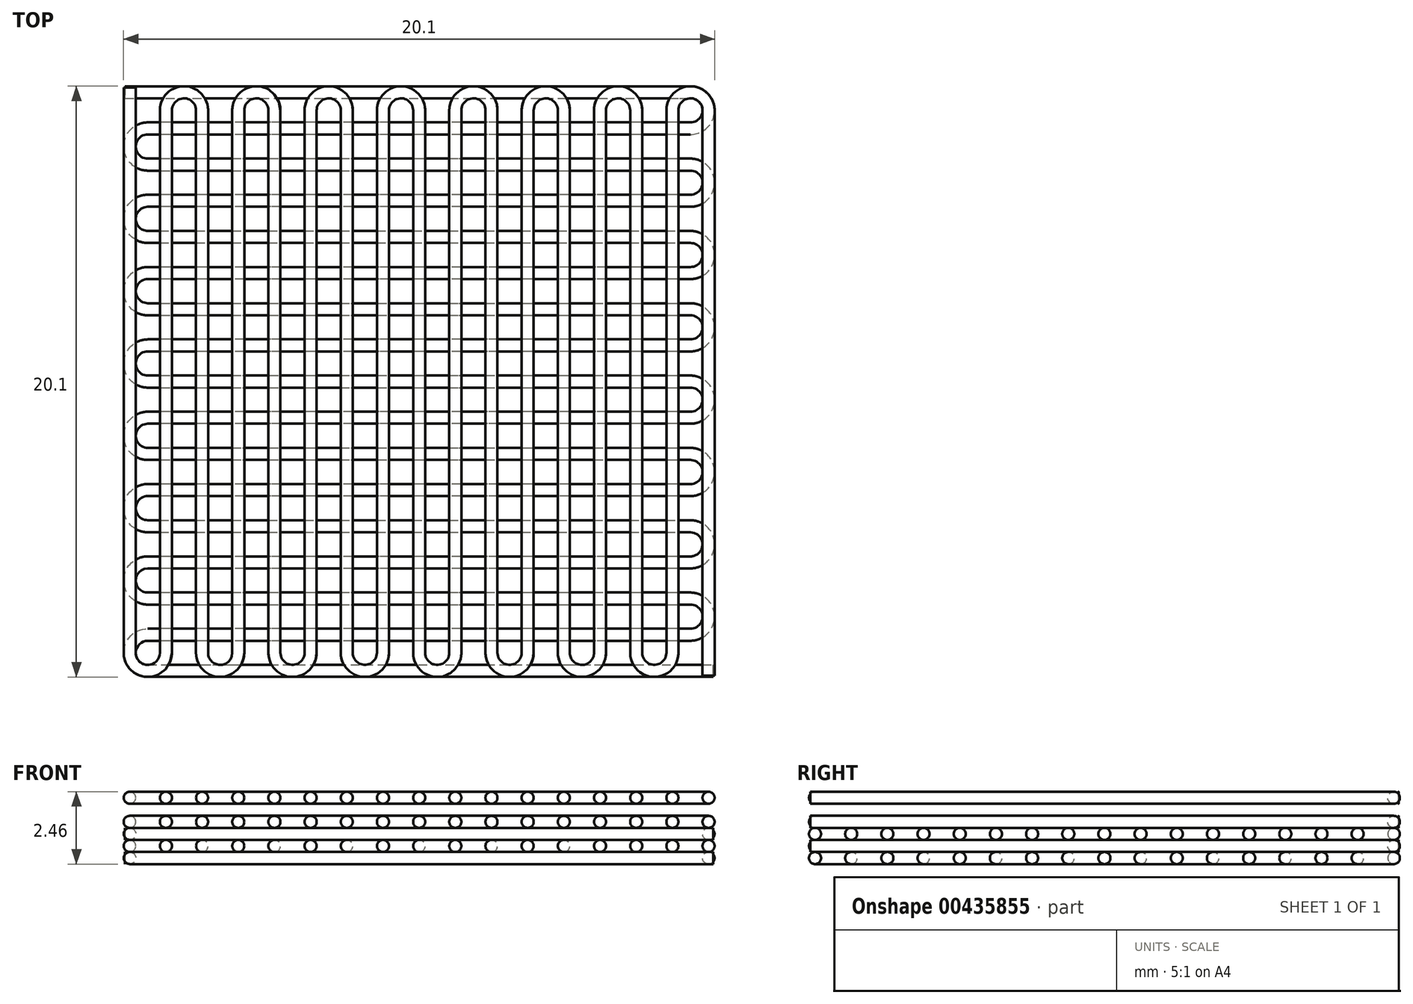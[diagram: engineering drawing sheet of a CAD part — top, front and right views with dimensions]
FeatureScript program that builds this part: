
annotation { "Feature Type Name" : "Feature", "Feature Type Description" : "" }
export const myFeature = defineFeature(function(context is Context, id is Id, definition is map)
    precondition{}
    {
        {
            assignVariable(context, id + "F0", {"name" : "d", "anyValue" : 0.4 * mm});
        }
        {
            var Q0;
            Q0=qCreatedBy(makeId("Top.planeOp"),FACE);
            cPlane(context, id + "F1", {"entities" : qUnion([Q0]), "cplaneType" : CPlaneType.OFFSET, "offset" : getVariable(context, 'd') / 2, "width" : 150 * mm, "height" : 150 * mm});
        }
        {
            var Q0;
            Q0=qCreatedBy(id+"F1.planeOp",FACE);
            var sketch = newSketch(context, id + "F2", { "sketchPlane" : qUnion([Q0])});
            skLineSegment(sketch, "E0.bottom", {"start": v(10, 10) * mm, "end": v(-10, 10) * mm});
            skLineSegment(sketch, "E0.top", {"start": v(10, -10) * mm, "end": v(-10, -10) * mm});
            skLineSegment(sketch, "E0.left", {"start": v(10, 10) * mm, "end": v(10, -10) * mm});
            skLineSegment(sketch, "E0.right", {"start": v(-10, 10) * mm, "end": v(-10, -10) * mm});
            skPoint(sketch, "E0.middle", {"position": v(0, 0) * mm});
            skLineSegment(sketch, "E1", {"start": v(-10, 10) * mm, "end": v(-9.84, 10) * mm});
            skLineSegment(sketch, "E2", {"start": v(-9.84, 10) * mm, "end": v(-8.61, 10) * mm});
            skLineSegment(sketch, "E3", {"start": v(-8.61, 10) * mm, "end": v(-7.38, 10) * mm});
            skLineSegment(sketch, "E4", {"start": v(-7.38, 10) * mm, "end": v(-6.15, 10) * mm});
            skLineSegment(sketch, "E5", {"start": v(-6.15, 10) * mm, "end": v(-4.92, 10) * mm});
            skLineSegment(sketch, "E6", {"start": v(-4.92, 10) * mm, "end": v(-3.7, 10) * mm});
            skLineSegment(sketch, "E7", {"start": v(-3.7, 10) * mm, "end": v(-2.46, 10) * mm});
            skLineSegment(sketch, "E8", {"start": v(-2.46, 10) * mm, "end": v(-1.23, 10) * mm});
            skLineSegment(sketch, "E9", {"start": v(-1.23, 10) * mm, "end": v(0, 10) * mm});
            skLineSegment(sketch, "E10", {"start": v(0, 10) * mm, "end": v(1.23, 10) * mm});
            skLineSegment(sketch, "E11", {"start": v(1.23, 10) * mm, "end": v(2.46, 10) * mm});
            skLineSegment(sketch, "E12", {"start": v(2.46, 10) * mm, "end": v(3.69, 10) * mm});
            skLineSegment(sketch, "E13", {"start": v(3.69, 10) * mm, "end": v(4.92, 10) * mm});
            skLineSegment(sketch, "E14", {"start": v(4.92, 10) * mm, "end": v(6.15, 10) * mm});
            skLineSegment(sketch, "E15", {"start": v(6.15, 10) * mm, "end": v(7.38, 10) * mm});
            skLineSegment(sketch, "E16", {"start": v(7.38, 10) * mm, "end": v(8.6, 10) * mm});
            skLineSegment(sketch, "E17", {"start": v(8.6, 10) * mm, "end": v(9.84, 10) * mm});
            skLineSegment(sketch, "E18", {"start": v(9.84, 10) * mm, "end": v(10, 10) * mm});
            skLineSegment(sketch, "E19", {"start": v(-9.84, 10) * mm, "end": v(-9.84, -10) * mm});
            skLineSegment(sketch, "E20", {"start": v(-9.84, -10) * mm, "end": v(-10, -10) * mm});
            skLineSegment(sketch, "E21", {"start": v(-8.61, 10) * mm, "end": v(-8.61, -10) * mm});
            skLineSegment(sketch, "E22", {"start": v(-8.61, -10) * mm, "end": v(-9.84, -10) * mm});
            skLineSegment(sketch, "E23", {"start": v(-7.38, 10) * mm, "end": v(-7.38, -10) * mm});
            skLineSegment(sketch, "E24", {"start": v(-7.38, -10) * mm, "end": v(-8.61, -10) * mm});
            skLineSegment(sketch, "E25", {"start": v(-6.15, 10) * mm, "end": v(-6.15, -10) * mm});
            skLineSegment(sketch, "E26", {"start": v(-6.15, -10) * mm, "end": v(-7.38, -10) * mm});
            skLineSegment(sketch, "E27", {"start": v(-4.92, 10) * mm, "end": v(-4.92, -10) * mm});
            skLineSegment(sketch, "E28", {"start": v(-4.92, -10) * mm, "end": v(-6.15, -10) * mm});
            skLineSegment(sketch, "E29", {"start": v(-3.7, 10) * mm, "end": v(-3.7, -10) * mm});
            skLineSegment(sketch, "E30", {"start": v(-3.7, -10) * mm, "end": v(-4.92, -10) * mm});
            skLineSegment(sketch, "E31", {"start": v(-2.46, 10) * mm, "end": v(-2.46, -10) * mm});
            skLineSegment(sketch, "E32", {"start": v(-2.46, -10) * mm, "end": v(-3.7, -10) * mm});
            skLineSegment(sketch, "E33", {"start": v(-1.23, 10) * mm, "end": v(-1.23, -10) * mm});
            skLineSegment(sketch, "E34", {"start": v(-1.23, -10) * mm, "end": v(-2.46, -10) * mm});
            skLineSegment(sketch, "E35", {"start": v(0, 10) * mm, "end": v(0, -10) * mm});
            skLineSegment(sketch, "E36", {"start": v(0, -10) * mm, "end": v(-1.23, -10) * mm});
            skLineSegment(sketch, "E37", {"start": v(1.23, 10) * mm, "end": v(1.23, -10) * mm});
            skLineSegment(sketch, "E38", {"start": v(1.23, -10) * mm, "end": v(0, -10) * mm});
            skLineSegment(sketch, "E39", {"start": v(2.46, 10) * mm, "end": v(2.46, -10) * mm});
            skLineSegment(sketch, "E40", {"start": v(2.46, -10) * mm, "end": v(1.23, -10) * mm});
            skLineSegment(sketch, "E41", {"start": v(3.69, 10) * mm, "end": v(3.69, -10) * mm});
            skLineSegment(sketch, "E42", {"start": v(3.69, -10) * mm, "end": v(2.46, -10) * mm});
            skLineSegment(sketch, "E43", {"start": v(4.92, 10) * mm, "end": v(4.92, -10) * mm});
            skLineSegment(sketch, "E44", {"start": v(4.92, -10) * mm, "end": v(3.69, -10) * mm});
            skLineSegment(sketch, "E45", {"start": v(6.15, 10) * mm, "end": v(6.15, -10) * mm});
            skLineSegment(sketch, "E46", {"start": v(6.15, -10) * mm, "end": v(4.92, -10) * mm});
            skLineSegment(sketch, "E47", {"start": v(7.38, 10) * mm, "end": v(7.38, -10) * mm});
            skLineSegment(sketch, "E48", {"start": v(7.38, -10) * mm, "end": v(6.15, -10) * mm});
            skLineSegment(sketch, "E49", {"start": v(8.6, 10) * mm, "end": v(8.6, -10) * mm});
            skLineSegment(sketch, "E50", {"start": v(8.6, -10) * mm, "end": v(7.38, -10) * mm});
            skLineSegment(sketch, "E51", {"start": v(9.84, 10) * mm, "end": v(9.84, -10) * mm});
            skLineSegment(sketch, "E52", {"start": v(9.84, -10) * mm, "end": v(8.6, -10) * mm});
            skLineSegment(sketch, "E53", {"start": v(10, -10) * mm, "end": v(9.84, -10) * mm});
            skLineSegment(sketch, "E54", {"start": v(-10, 9.84) * mm, "end": v(-9.84, 9.84) * mm});
            skLineSegment(sketch, "E55", {"start": v(-9.84, 9.84) * mm, "end": v(-8.61, 9.84) * mm});
            skLineSegment(sketch, "E56", {"start": v(-8.61, 9.84) * mm, "end": v(-7.38, 9.84) * mm});
            skLineSegment(sketch, "E57", {"start": v(-7.38, 9.84) * mm, "end": v(-6.15, 9.84) * mm});
            skLineSegment(sketch, "E58", {"start": v(-6.15, 9.84) * mm, "end": v(-4.92, 9.84) * mm});
            skLineSegment(sketch, "E59", {"start": v(-4.92, 9.84) * mm, "end": v(-3.7, 9.84) * mm});
            skLineSegment(sketch, "E60", {"start": v(-3.7, 9.84) * mm, "end": v(-2.46, 9.84) * mm});
            skLineSegment(sketch, "E61", {"start": v(-2.46, 9.84) * mm, "end": v(-1.23, 9.84) * mm});
            skLineSegment(sketch, "E62", {"start": v(-1.23, 9.84) * mm, "end": v(0, 9.84) * mm});
            skLineSegment(sketch, "E63", {"start": v(0, 9.84) * mm, "end": v(1.23, 9.84) * mm});
            skLineSegment(sketch, "E64", {"start": v(1.23, 9.84) * mm, "end": v(2.46, 9.84) * mm});
            skLineSegment(sketch, "E65", {"start": v(2.46, 9.84) * mm, "end": v(3.69, 9.84) * mm});
            skLineSegment(sketch, "E66", {"start": v(3.69, 9.84) * mm, "end": v(4.92, 9.84) * mm});
            skLineSegment(sketch, "E67", {"start": v(4.92, 9.84) * mm, "end": v(6.15, 9.84) * mm});
            skLineSegment(sketch, "E68", {"start": v(6.15, 9.84) * mm, "end": v(7.38, 9.84) * mm});
            skLineSegment(sketch, "E69", {"start": v(7.38, 9.84) * mm, "end": v(8.6, 9.84) * mm});
            skLineSegment(sketch, "E70", {"start": v(8.6, 9.84) * mm, "end": v(9.84, 9.84) * mm});
            skLineSegment(sketch, "E71", {"start": v(9.84, 9.84) * mm, "end": v(10, 9.84) * mm});
            skLineSegment(sketch, "E72", {"start": v(-10, -9.84) * mm, "end": v(-9.84, -9.84) * mm});
            skLineSegment(sketch, "E73", {"start": v(-9.84, -9.84) * mm, "end": v(-8.61, -9.84) * mm});
            skLineSegment(sketch, "E74", {"start": v(-8.61, -9.84) * mm, "end": v(-7.38, -9.84) * mm});
            skLineSegment(sketch, "E75", {"start": v(-7.38, -9.84) * mm, "end": v(-6.15, -9.84) * mm});
            skLineSegment(sketch, "E76", {"start": v(-6.15, -9.84) * mm, "end": v(-4.92, -9.84) * mm});
            skLineSegment(sketch, "E77", {"start": v(-4.92, -9.84) * mm, "end": v(-3.7, -9.84) * mm});
            skLineSegment(sketch, "E78", {"start": v(-3.7, -9.84) * mm, "end": v(-2.46, -9.84) * mm});
            skLineSegment(sketch, "E79", {"start": v(-2.46, -9.84) * mm, "end": v(-1.23, -9.84) * mm});
            skLineSegment(sketch, "E80", {"start": v(-1.23, -9.84) * mm, "end": v(0, -9.84) * mm});
            skLineSegment(sketch, "E81", {"start": v(0, -9.84) * mm, "end": v(1.23, -9.84) * mm});
            skLineSegment(sketch, "E82", {"start": v(1.23, -9.84) * mm, "end": v(2.46, -9.84) * mm});
            skLineSegment(sketch, "E83", {"start": v(2.46, -9.84) * mm, "end": v(3.69, -9.84) * mm});
            skLineSegment(sketch, "E84", {"start": v(3.69, -9.84) * mm, "end": v(4.92, -9.84) * mm});
            skLineSegment(sketch, "E85", {"start": v(4.92, -9.84) * mm, "end": v(6.15, -9.84) * mm});
            skLineSegment(sketch, "E86", {"start": v(6.15, -9.84) * mm, "end": v(7.38, -9.84) * mm});
            skLineSegment(sketch, "E87", {"start": v(7.38, -9.84) * mm, "end": v(8.6, -9.84) * mm});
            skLineSegment(sketch, "E88", {"start": v(8.6, -9.84) * mm, "end": v(9.84, -9.84) * mm});
            skLineSegment(sketch, "E89", {"start": v(9.84, -9.84) * mm, "end": v(10, -9.84) * mm});
            skLineSegment(sketch, "E90", {"start": v(-10, 10) * mm, "end": v(-10, 9.84) * mm});
            skLineSegment(sketch, "E91", {"start": v(-10, -9.84) * mm, "end": v(-10, -10) * mm});
            skLineSegment(sketch, "E92", {"start": v(10, -9.84) * mm, "end": v(10, -10) * mm});
            skLineSegment(sketch, "E93", {"start": v(10, 9.84) * mm, "end": v(10, 10) * mm});
            skLineSegment(sketch, "E94", {"start": v(-10, 9.84) * mm, "end": v(-10, 9.22) * mm});
            skLineSegment(sketch, "E95", {"start": v(-10, 9.22) * mm, "end": v(-9.84, 9.22) * mm});
            skLineSegment(sketch, "E96", {"start": v(-9.84, 9.22) * mm, "end": v(-8.61, 9.22) * mm});
            skLineSegment(sketch, "E97", {"start": v(-8.61, 9.22) * mm, "end": v(-7.38, 9.22) * mm});
            skLineSegment(sketch, "E98", {"start": v(-7.38, 9.22) * mm, "end": v(-6.15, 9.22) * mm});
            skLineSegment(sketch, "E99", {"start": v(-6.15, 9.22) * mm, "end": v(-4.92, 9.22) * mm});
            skLineSegment(sketch, "E100", {"start": v(-4.92, 9.22) * mm, "end": v(-3.7, 9.22) * mm});
            skLineSegment(sketch, "E101", {"start": v(-3.7, 9.22) * mm, "end": v(-2.46, 9.22) * mm});
            skLineSegment(sketch, "E102", {"start": v(-2.46, 9.22) * mm, "end": v(-1.23, 9.22) * mm});
            skLineSegment(sketch, "E103", {"start": v(-1.23, 9.22) * mm, "end": v(0, 9.22) * mm});
            skLineSegment(sketch, "E104", {"start": v(0, 9.22) * mm, "end": v(1.23, 9.22) * mm});
            skLineSegment(sketch, "E105", {"start": v(1.23, 9.22) * mm, "end": v(2.46, 9.22) * mm});
            skLineSegment(sketch, "E106", {"start": v(2.46, 9.22) * mm, "end": v(3.69, 9.22) * mm});
            skLineSegment(sketch, "E107", {"start": v(3.69, 9.22) * mm, "end": v(4.92, 9.22) * mm});
            skLineSegment(sketch, "E108", {"start": v(4.92, 9.22) * mm, "end": v(6.15, 9.22) * mm});
            skLineSegment(sketch, "E109", {"start": v(6.15, 9.22) * mm, "end": v(7.38, 9.22) * mm});
            skLineSegment(sketch, "E110", {"start": v(7.38, 9.22) * mm, "end": v(8.6, 9.22) * mm});
            skLineSegment(sketch, "E111", {"start": v(8.6, 9.22) * mm, "end": v(9.84, 9.22) * mm});
            skLineSegment(sketch, "E112", {"start": v(9.84, 9.22) * mm, "end": v(10, 9.22) * mm});
            skLineSegment(sketch, "E113", {"start": v(10, 9.22) * mm, "end": v(10, 9.84) * mm});
            skLineSegment(sketch, "E114", {"start": v(-10, -9.84) * mm, "end": v(-10, -9.22) * mm});
            skLineSegment(sketch, "E115", {"start": v(-10, -9.22) * mm, "end": v(-9.84, -9.22) * mm});
            skLineSegment(sketch, "E116", {"start": v(-9.84, -9.22) * mm, "end": v(-8.61, -9.22) * mm});
            skLineSegment(sketch, "E117", {"start": v(-8.61, -9.22) * mm, "end": v(-7.38, -9.22) * mm});
            skLineSegment(sketch, "E118", {"start": v(-7.38, -9.22) * mm, "end": v(-6.15, -9.22) * mm});
            skLineSegment(sketch, "E119", {"start": v(-6.15, -9.22) * mm, "end": v(-4.92, -9.22) * mm});
            skLineSegment(sketch, "E120", {"start": v(-4.92, -9.22) * mm, "end": v(-3.7, -9.22) * mm});
            skLineSegment(sketch, "E121", {"start": v(-3.7, -9.22) * mm, "end": v(-2.46, -9.22) * mm});
            skLineSegment(sketch, "E122", {"start": v(-2.46, -9.22) * mm, "end": v(-1.23, -9.22) * mm});
            skLineSegment(sketch, "E123", {"start": v(-1.23, -9.22) * mm, "end": v(0, -9.22) * mm});
            skLineSegment(sketch, "E124", {"start": v(0, -9.22) * mm, "end": v(1.23, -9.22) * mm});
            skLineSegment(sketch, "E125", {"start": v(1.23, -9.22) * mm, "end": v(2.46, -9.22) * mm});
            skLineSegment(sketch, "E126", {"start": v(2.46, -9.22) * mm, "end": v(3.69, -9.22) * mm});
            skLineSegment(sketch, "E127", {"start": v(3.69, -9.22) * mm, "end": v(4.92, -9.22) * mm});
            skLineSegment(sketch, "E128", {"start": v(4.92, -9.22) * mm, "end": v(6.15, -9.22) * mm});
            skLineSegment(sketch, "E129", {"start": v(6.15, -9.22) * mm, "end": v(7.38, -9.22) * mm});
            skLineSegment(sketch, "E130", {"start": v(7.38, -9.22) * mm, "end": v(8.6, -9.22) * mm});
            skLineSegment(sketch, "E131", {"start": v(8.6, -9.22) * mm, "end": v(9.84, -9.22) * mm});
            skLineSegment(sketch, "E132", {"start": v(9.84, -9.22) * mm, "end": v(10, -9.22) * mm});
            skLineSegment(sketch, "E133", {"start": v(9.84, -10) * mm, "end": v(9.84, 9.22) * mm});
            skLineSegment(sketch, "E134", {"start": v(10, -9.22) * mm, "end": v(10, -9.84) * mm});
            skLineSegment(sketch, "E135", {"start": v(8.6, 9.22) * mm, "end": v(8.6, -9.22) * mm});
            skLineSegment(sketch, "E136", {"start": v(7.38, -9.22) * mm, "end": v(7.38, 9.22) * mm});
            skLineSegment(sketch, "E137", {"start": v(6.15, 9.22) * mm, "end": v(6.15, -9.22) * mm});
            skLineSegment(sketch, "E138", {"start": v(4.92, -9.22) * mm, "end": v(4.92, 9.22) * mm});
            skLineSegment(sketch, "E139", {"start": v(3.69, 9.22) * mm, "end": v(3.69, -9.22) * mm});
            skLineSegment(sketch, "E140", {"start": v(2.46, -9.22) * mm, "end": v(2.46, 9.22) * mm});
            skLineSegment(sketch, "E141", {"start": v(1.23, 9.22) * mm, "end": v(1.23, -9.22) * mm});
            skLineSegment(sketch, "E142", {"start": v(0, -9.22) * mm, "end": v(0, 9.22) * mm});
            skLineSegment(sketch, "E143", {"start": v(-1.23, 9.22) * mm, "end": v(-1.23, -9.22) * mm});
            skLineSegment(sketch, "E144", {"start": v(-2.46, -9.22) * mm, "end": v(-2.46, 9.22) * mm});
            skLineSegment(sketch, "E145", {"start": v(-3.7, 9.22) * mm, "end": v(-3.7, -9.22) * mm});
            skLineSegment(sketch, "E146", {"start": v(-4.92, -9.22) * mm, "end": v(-4.92, 9.22) * mm});
            skLineSegment(sketch, "E147", {"start": v(-6.15, 9.22) * mm, "end": v(-6.15, -9.22) * mm});
            skLineSegment(sketch, "E148", {"start": v(-7.38, -9.22) * mm, "end": v(-7.38, 9.22) * mm});
            skLineSegment(sketch, "E149", {"start": v(-8.61, 9.22) * mm, "end": v(-8.61, -9.22) * mm});
            skArc(sketch, "E150", {"start": v(9.84, 9.22) * mm, "mid": v(9.22, 9.84) * mm, "end": v(8.6, 9.22) * mm});
            skArc(sketch, "E151", {"start": v(7.38, -9.22) * mm, "mid": v(8, -9.84) * mm, "end": v(8.6, -9.22) * mm});
            skArc(sketch, "E152", {"start": v(7.38, 9.22) * mm, "mid": v(6.76, 9.84) * mm, "end": v(6.15, 9.22) * mm});
            skArc(sketch, "E153", {"start": v(4.92, -9.22) * mm, "mid": v(5.53, -9.84) * mm, "end": v(6.15, -9.22) * mm});
            skArc(sketch, "E154", {"start": v(4.92, 9.22) * mm, "mid": v(4.3, 9.84) * mm, "end": v(3.69, 9.22) * mm});
            skArc(sketch, "E155", {"start": v(2.46, 9.22) * mm, "mid": v(1.84, 9.84) * mm, "end": v(1.23, 9.22) * mm});
            skArc(sketch, "E156", {"start": v(2.46, -9.22) * mm, "mid": v(3.07, -9.84) * mm, "end": v(3.69, -9.22) * mm});
            skArc(sketch, "E157", {"start": v(0, 9.22) * mm, "mid": v(-0.62, 9.84) * mm, "end": v(-1.23, 9.22) * mm});
            skArc(sketch, "E158", {"start": v(-2.46, 9.22) * mm, "mid": v(-3.08, 9.84) * mm, "end": v(-3.7, 9.22) * mm});
            skArc(sketch, "E159", {"start": v(-4.92, 9.22) * mm, "mid": v(-5.54, 9.84) * mm, "end": v(-6.15, 9.22) * mm});
            skArc(sketch, "E160", {"start": v(-2.46, -9.22) * mm, "mid": v(-1.85, -9.84) * mm, "end": v(-1.23, -9.22) * mm});
            skArc(sketch, "E161", {"start": v(-4.92, -9.22) * mm, "mid": v(-4.3, -9.84) * mm, "end": v(-3.7, -9.22) * mm});
            skArc(sketch, "E162", {"start": v(-9.84, -9.22) * mm, "mid": v(-9.23, -9.84) * mm, "end": v(-8.61, -9.22) * mm});
            skArc(sketch, "E163", {"start": v(0, -9.22) * mm, "mid": v(0.62, -9.84) * mm, "end": v(1.23, -9.22) * mm});
            skArc(sketch, "E164", {"start": v(-7.38, -9.22) * mm, "mid": v(-6.77, -9.84) * mm, "end": v(-6.15, -9.22) * mm});
            skLineSegment(sketch, "E165", {"start": v(-9.84, -9.22) * mm, "end": v(-9.84, 10) * mm});
            skArc(sketch, "E166", {"start": v(-7.38, 9.22) * mm, "mid": v(-8, 9.84) * mm, "end": v(-8.61, 9.22) * mm});
            skSolve(sketch);
        }
        {
            var Q0;
            Q0=sQuery(id+"F2.wireOp",VERTEX,"E53.end");
            var Q1;
            Q1=sQuery(id+"F2.wireOp",EDGE,"E133");
            cPlane(context, id + "F3", {"entities" : qUnion([Q0, Q1]), "cplaneType" : CPlaneType.LINE_POINT, "offset" : 25 * mm, "width" : 150 * mm, "height" : 150 * mm});
        }
        {
            var Q0;
            Q0=qCreatedBy(id+"F3.planeOp",FACE);
            var sketch = newSketch(context, id + "F4", { "sketchPlane" : qUnion([Q0])});
            skCircle(sketch, "E167", {"center": v(-9.84, 0.2) * mm, "radius": 0.2 * mm});
            skSolve(sketch);
        }
        {
            var Q0;
            Q0=qCreatedBy(id+"F1.planeOp",FACE);
            cPlane(context, id + "F5", {"entities" : qUnion([Q0]), "cplaneType" : CPlaneType.OFFSET, "offset" : getVariable(context, 'd'), "width" : 150 * mm, "height" : 150 * mm});
        }
        {
            var Q0;
            Q0=qCreatedBy(id+"F5.planeOp",FACE);
            var sketch = newSketch(context, id + "F6", { "sketchPlane" : qUnion([Q0])});
            skLineSegment(sketch, "E168.bottom", {"start": v(10, 10) * mm, "end": v(10, 30) * mm});
            skLineSegment(sketch, "E168.top", {"start": v(-10, 10) * mm, "end": v(-10, 30) * mm});
            skLineSegment(sketch, "E168.left", {"start": v(10, 10) * mm, "end": v(-10, 10) * mm});
            skLineSegment(sketch, "E168.right", {"start": v(10, 30) * mm, "end": v(-10, 30) * mm});
            skPoint(sketch, "E168.middle", {"position": v(0, 20) * mm});
            skLineSegment(sketch, "E169", {"start": v(10, 30) * mm, "end": v(10, 29.84) * mm});
            skLineSegment(sketch, "E170", {"start": v(10, 29.84) * mm, "end": v(10, 28.6) * mm});
            skLineSegment(sketch, "E171", {"start": v(10, 28.6) * mm, "end": v(10, 27.38) * mm});
            skLineSegment(sketch, "E172", {"start": v(10, 27.38) * mm, "end": v(10, 26.15) * mm});
            skLineSegment(sketch, "E173", {"start": v(10, 26.15) * mm, "end": v(10, 24.92) * mm});
            skLineSegment(sketch, "E174", {"start": v(10, 24.92) * mm, "end": v(10, 23.69) * mm});
            skLineSegment(sketch, "E175", {"start": v(10, 23.69) * mm, "end": v(10, 22.46) * mm});
            skLineSegment(sketch, "E176", {"start": v(10, 22.46) * mm, "end": v(10, 21.23) * mm});
            skLineSegment(sketch, "E177", {"start": v(10, 21.23) * mm, "end": v(10, 20) * mm});
            skLineSegment(sketch, "E178", {"start": v(10, 20) * mm, "end": v(10, 18.77) * mm});
            skLineSegment(sketch, "E179", {"start": v(10, 18.77) * mm, "end": v(10, 17.54) * mm});
            skLineSegment(sketch, "E180", {"start": v(10, 17.54) * mm, "end": v(10, 16.31) * mm});
            skLineSegment(sketch, "E181", {"start": v(10, 16.31) * mm, "end": v(10, 15.08) * mm});
            skLineSegment(sketch, "E182", {"start": v(10, 15.08) * mm, "end": v(10, 13.85) * mm});
            skLineSegment(sketch, "E183", {"start": v(10, 13.85) * mm, "end": v(10, 12.62) * mm});
            skLineSegment(sketch, "E184", {"start": v(10, 12.62) * mm, "end": v(10, 11.4) * mm});
            skLineSegment(sketch, "E185", {"start": v(10, 11.4) * mm, "end": v(10, 10.16) * mm});
            skLineSegment(sketch, "E186", {"start": v(10, 10.16) * mm, "end": v(10, 10) * mm});
            skLineSegment(sketch, "E187", {"start": v(10, 29.84) * mm, "end": v(-10, 29.84) * mm});
            skLineSegment(sketch, "E188", {"start": v(-10, 29.84) * mm, "end": v(-10, 30) * mm});
            skLineSegment(sketch, "E189", {"start": v(10, 28.6) * mm, "end": v(-10, 28.6) * mm});
            skLineSegment(sketch, "E190", {"start": v(-10, 28.6) * mm, "end": v(-10, 29.84) * mm});
            skLineSegment(sketch, "E191", {"start": v(10, 27.38) * mm, "end": v(-10, 27.38) * mm});
            skLineSegment(sketch, "E192", {"start": v(-10, 27.38) * mm, "end": v(-10, 28.6) * mm});
            skLineSegment(sketch, "E193", {"start": v(10, 26.15) * mm, "end": v(-10, 26.15) * mm});
            skLineSegment(sketch, "E194", {"start": v(-10, 26.15) * mm, "end": v(-10, 27.38) * mm});
            skLineSegment(sketch, "E195", {"start": v(10, 24.92) * mm, "end": v(-10, 24.92) * mm});
            skLineSegment(sketch, "E196", {"start": v(-10, 24.92) * mm, "end": v(-10, 26.15) * mm});
            skLineSegment(sketch, "E197", {"start": v(10, 23.69) * mm, "end": v(-10, 23.69) * mm});
            skLineSegment(sketch, "E198", {"start": v(-10, 23.69) * mm, "end": v(-10, 24.92) * mm});
            skLineSegment(sketch, "E199", {"start": v(10, 22.46) * mm, "end": v(-10, 22.46) * mm});
            skLineSegment(sketch, "E200", {"start": v(-10, 22.46) * mm, "end": v(-10, 23.69) * mm});
            skLineSegment(sketch, "E201", {"start": v(10, 21.23) * mm, "end": v(-10, 21.23) * mm});
            skLineSegment(sketch, "E202", {"start": v(-10, 21.23) * mm, "end": v(-10, 22.46) * mm});
            skLineSegment(sketch, "E203", {"start": v(10, 20) * mm, "end": v(-10, 20) * mm});
            skLineSegment(sketch, "E204", {"start": v(-10, 20) * mm, "end": v(-10, 21.23) * mm});
            skLineSegment(sketch, "E205", {"start": v(10, 18.77) * mm, "end": v(-10, 18.77) * mm});
            skLineSegment(sketch, "E206", {"start": v(-10, 18.77) * mm, "end": v(-10, 20) * mm});
            skLineSegment(sketch, "E207", {"start": v(10, 17.54) * mm, "end": v(-10, 17.54) * mm});
            skLineSegment(sketch, "E208", {"start": v(-10, 17.54) * mm, "end": v(-10, 18.77) * mm});
            skLineSegment(sketch, "E209", {"start": v(10, 16.31) * mm, "end": v(-10, 16.31) * mm});
            skLineSegment(sketch, "E210", {"start": v(-10, 16.31) * mm, "end": v(-10, 17.54) * mm});
            skLineSegment(sketch, "E211", {"start": v(10, 15.08) * mm, "end": v(-10, 15.08) * mm});
            skLineSegment(sketch, "E212", {"start": v(-10, 15.08) * mm, "end": v(-10, 16.31) * mm});
            skLineSegment(sketch, "E213", {"start": v(10, 13.85) * mm, "end": v(-10, 13.85) * mm});
            skLineSegment(sketch, "E214", {"start": v(-10, 13.85) * mm, "end": v(-10, 15.08) * mm});
            skLineSegment(sketch, "E215", {"start": v(10, 12.62) * mm, "end": v(-10, 12.62) * mm});
            skLineSegment(sketch, "E216", {"start": v(-10, 12.62) * mm, "end": v(-10, 13.85) * mm});
            skLineSegment(sketch, "E217", {"start": v(10, 11.39) * mm, "end": v(-10, 11.39) * mm});
            skLineSegment(sketch, "E218", {"start": v(-10, 11.39) * mm, "end": v(-10, 12.62) * mm});
            skLineSegment(sketch, "E219", {"start": v(10, 10.16) * mm, "end": v(-10, 10.16) * mm});
            skLineSegment(sketch, "E220", {"start": v(-10, 10.16) * mm, "end": v(-10, 11.39) * mm});
            skLineSegment(sketch, "E221", {"start": v(-10, 10) * mm, "end": v(-10, 10.16) * mm});
            skLineSegment(sketch, "E222", {"start": v(9.84, 30) * mm, "end": v(9.84, 29.84) * mm});
            skLineSegment(sketch, "E223", {"start": v(9.84, 29.84) * mm, "end": v(9.84, 28.6) * mm});
            skLineSegment(sketch, "E224", {"start": v(9.84, 28.6) * mm, "end": v(9.84, 27.38) * mm});
            skLineSegment(sketch, "E225", {"start": v(9.84, 27.38) * mm, "end": v(9.84, 26.15) * mm});
            skLineSegment(sketch, "E226", {"start": v(9.84, 26.15) * mm, "end": v(9.84, 24.92) * mm});
            skLineSegment(sketch, "E227", {"start": v(9.84, 24.92) * mm, "end": v(9.84, 23.69) * mm});
            skLineSegment(sketch, "E228", {"start": v(9.84, 23.69) * mm, "end": v(9.84, 22.46) * mm});
            skLineSegment(sketch, "E229", {"start": v(9.84, 22.46) * mm, "end": v(9.84, 21.23) * mm});
            skLineSegment(sketch, "E230", {"start": v(9.84, 21.23) * mm, "end": v(9.84, 20) * mm});
            skLineSegment(sketch, "E231", {"start": v(9.84, 20) * mm, "end": v(9.84, 18.77) * mm});
            skLineSegment(sketch, "E232", {"start": v(9.84, 18.77) * mm, "end": v(9.84, 17.54) * mm});
            skLineSegment(sketch, "E233", {"start": v(9.84, 17.54) * mm, "end": v(9.84, 16.31) * mm});
            skLineSegment(sketch, "E234", {"start": v(9.84, 16.31) * mm, "end": v(9.84, 15.08) * mm});
            skLineSegment(sketch, "E235", {"start": v(9.84, 15.08) * mm, "end": v(9.84, 13.85) * mm});
            skLineSegment(sketch, "E236", {"start": v(9.84, 13.85) * mm, "end": v(9.84, 12.62) * mm});
            skLineSegment(sketch, "E237", {"start": v(9.84, 12.62) * mm, "end": v(9.84, 11.39) * mm});
            skLineSegment(sketch, "E238", {"start": v(9.84, 11.39) * mm, "end": v(9.84, 10.16) * mm});
            skLineSegment(sketch, "E239", {"start": v(9.84, 10.16) * mm, "end": v(9.84, 10) * mm});
            skLineSegment(sketch, "E240", {"start": v(-9.84, 30) * mm, "end": v(-9.84, 29.84) * mm});
            skLineSegment(sketch, "E241", {"start": v(-9.84, 29.84) * mm, "end": v(-9.84, 28.6) * mm});
            skLineSegment(sketch, "E242", {"start": v(-9.84, 28.6) * mm, "end": v(-9.84, 27.38) * mm});
            skLineSegment(sketch, "E243", {"start": v(-9.84, 27.38) * mm, "end": v(-9.84, 26.15) * mm});
            skLineSegment(sketch, "E244", {"start": v(-9.84, 26.15) * mm, "end": v(-9.84, 24.92) * mm});
            skLineSegment(sketch, "E245", {"start": v(-9.84, 24.92) * mm, "end": v(-9.84, 23.69) * mm});
            skLineSegment(sketch, "E246", {"start": v(-9.84, 23.69) * mm, "end": v(-9.84, 22.46) * mm});
            skLineSegment(sketch, "E247", {"start": v(-9.84, 22.46) * mm, "end": v(-9.84, 21.23) * mm});
            skLineSegment(sketch, "E248", {"start": v(-9.84, 21.23) * mm, "end": v(-9.84, 20) * mm});
            skLineSegment(sketch, "E249", {"start": v(-9.84, 20) * mm, "end": v(-9.84, 18.77) * mm});
            skLineSegment(sketch, "E250", {"start": v(-9.84, 18.77) * mm, "end": v(-9.84, 17.54) * mm});
            skLineSegment(sketch, "E251", {"start": v(-9.84, 17.54) * mm, "end": v(-9.84, 16.31) * mm});
            skLineSegment(sketch, "E252", {"start": v(-9.84, 16.31) * mm, "end": v(-9.84, 15.08) * mm});
            skLineSegment(sketch, "E253", {"start": v(-9.84, 15.08) * mm, "end": v(-9.84, 13.85) * mm});
            skLineSegment(sketch, "E254", {"start": v(-9.84, 13.85) * mm, "end": v(-9.84, 12.62) * mm});
            skLineSegment(sketch, "E255", {"start": v(-9.84, 12.62) * mm, "end": v(-9.84, 11.39) * mm});
            skLineSegment(sketch, "E256", {"start": v(-9.84, 11.39) * mm, "end": v(-9.84, 10.16) * mm});
            skLineSegment(sketch, "E257", {"start": v(-9.84, 10.16) * mm, "end": v(-9.84, 10) * mm});
            skLineSegment(sketch, "E258", {"start": v(10, 30) * mm, "end": v(9.84, 30) * mm});
            skLineSegment(sketch, "E259", {"start": v(-9.84, 30) * mm, "end": v(-10, 30) * mm});
            skLineSegment(sketch, "E260", {"start": v(-9.84, 10) * mm, "end": v(-10, 10) * mm});
            skLineSegment(sketch, "E261", {"start": v(9.84, 10) * mm, "end": v(10, 10) * mm});
            skLineSegment(sketch, "E262", {"start": v(9.84, 30) * mm, "end": v(9.23, 30) * mm});
            skLineSegment(sketch, "E263", {"start": v(9.23, 30) * mm, "end": v(9.23, 29.84) * mm});
            skLineSegment(sketch, "E264", {"start": v(9.23, 29.84) * mm, "end": v(9.23, 28.6) * mm});
            skLineSegment(sketch, "E265", {"start": v(9.23, 28.6) * mm, "end": v(9.23, 27.38) * mm});
            skLineSegment(sketch, "E266", {"start": v(9.23, 27.38) * mm, "end": v(9.23, 26.15) * mm});
            skLineSegment(sketch, "E267", {"start": v(9.23, 26.15) * mm, "end": v(9.23, 24.92) * mm});
            skLineSegment(sketch, "E268", {"start": v(9.23, 24.92) * mm, "end": v(9.23, 23.69) * mm});
            skLineSegment(sketch, "E269", {"start": v(9.23, 23.69) * mm, "end": v(9.23, 22.46) * mm});
            skLineSegment(sketch, "E270", {"start": v(9.23, 22.46) * mm, "end": v(9.23, 21.23) * mm});
            skLineSegment(sketch, "E271", {"start": v(9.23, 21.23) * mm, "end": v(9.23, 20) * mm});
            skLineSegment(sketch, "E272", {"start": v(9.23, 20) * mm, "end": v(9.23, 18.77) * mm});
            skLineSegment(sketch, "E273", {"start": v(9.23, 18.77) * mm, "end": v(9.23, 17.54) * mm});
            skLineSegment(sketch, "E274", {"start": v(9.23, 17.54) * mm, "end": v(9.23, 16.31) * mm});
            skLineSegment(sketch, "E275", {"start": v(9.23, 16.31) * mm, "end": v(9.23, 15.08) * mm});
            skLineSegment(sketch, "E276", {"start": v(9.23, 15.08) * mm, "end": v(9.23, 13.85) * mm});
            skLineSegment(sketch, "E277", {"start": v(9.23, 13.85) * mm, "end": v(9.23, 12.62) * mm});
            skLineSegment(sketch, "E278", {"start": v(9.23, 12.62) * mm, "end": v(9.23, 11.39) * mm});
            skLineSegment(sketch, "E279", {"start": v(9.23, 11.39) * mm, "end": v(9.23, 10.16) * mm});
            skLineSegment(sketch, "E280", {"start": v(9.23, 10.16) * mm, "end": v(9.23, 10) * mm});
            skLineSegment(sketch, "E281", {"start": v(9.23, 10) * mm, "end": v(9.84, 10) * mm});
            skLineSegment(sketch, "E282", {"start": v(-9.84, 30) * mm, "end": v(-9.23, 30) * mm});
            skLineSegment(sketch, "E283", {"start": v(-9.23, 30) * mm, "end": v(-9.23, 29.84) * mm});
            skLineSegment(sketch, "E284", {"start": v(-9.23, 29.84) * mm, "end": v(-9.23, 28.6) * mm});
            skLineSegment(sketch, "E285", {"start": v(-9.23, 28.6) * mm, "end": v(-9.23, 27.38) * mm});
            skLineSegment(sketch, "E286", {"start": v(-9.23, 27.38) * mm, "end": v(-9.23, 26.15) * mm});
            skLineSegment(sketch, "E287", {"start": v(-9.23, 26.15) * mm, "end": v(-9.23, 24.92) * mm});
            skLineSegment(sketch, "E288", {"start": v(-9.23, 24.92) * mm, "end": v(-9.23, 23.69) * mm});
            skLineSegment(sketch, "E289", {"start": v(-9.22, 23.69) * mm, "end": v(-9.22, 22.46) * mm});
            skLineSegment(sketch, "E290", {"start": v(-9.22, 22.46) * mm, "end": v(-9.22, 21.23) * mm});
            skLineSegment(sketch, "E291", {"start": v(-9.22, 21.23) * mm, "end": v(-9.22, 20) * mm});
            skLineSegment(sketch, "E292", {"start": v(-9.22, 20) * mm, "end": v(-9.22, 18.77) * mm});
            skLineSegment(sketch, "E293", {"start": v(-9.22, 18.77) * mm, "end": v(-9.22, 17.54) * mm});
            skLineSegment(sketch, "E294", {"start": v(-9.22, 17.54) * mm, "end": v(-9.22, 16.31) * mm});
            skLineSegment(sketch, "E295", {"start": v(-9.22, 16.31) * mm, "end": v(-9.22, 15.08) * mm});
            skLineSegment(sketch, "E296", {"start": v(-9.22, 15.08) * mm, "end": v(-9.22, 13.85) * mm});
            skLineSegment(sketch, "E297", {"start": v(-9.22, 13.85) * mm, "end": v(-9.22, 12.62) * mm});
            skLineSegment(sketch, "E298", {"start": v(-9.22, 12.62) * mm, "end": v(-9.22, 11.39) * mm});
            skLineSegment(sketch, "E299", {"start": v(-9.22, 11.39) * mm, "end": v(-9.22, 10.16) * mm});
            skLineSegment(sketch, "E300", {"start": v(-9.22, 10.16) * mm, "end": v(-9.22, 10) * mm});
            skLineSegment(sketch, "E301", {"start": v(-10, 10.16) * mm, "end": v(9.23, 10.16) * mm});
            skLineSegment(sketch, "E302", {"start": v(-9.23, 10) * mm, "end": v(-9.84, 10) * mm});
            skLineSegment(sketch, "E303", {"start": v(9.23, 11.39) * mm, "end": v(-9.22, 11.39) * mm});
            skLineSegment(sketch, "E304", {"start": v(-9.23, 12.62) * mm, "end": v(9.23, 12.62) * mm});
            skLineSegment(sketch, "E305", {"start": v(9.23, 13.85) * mm, "end": v(-9.22, 13.85) * mm});
            skLineSegment(sketch, "E306", {"start": v(-9.22, 15.08) * mm, "end": v(9.23, 15.08) * mm});
            skLineSegment(sketch, "E307", {"start": v(9.23, 16.31) * mm, "end": v(-9.22, 16.31) * mm});
            skLineSegment(sketch, "E308", {"start": v(-9.22, 17.54) * mm, "end": v(9.23, 17.54) * mm});
            skLineSegment(sketch, "E309", {"start": v(9.23, 18.77) * mm, "end": v(-9.22, 18.77) * mm});
            skLineSegment(sketch, "E310", {"start": v(-9.22, 20) * mm, "end": v(9.23, 20) * mm});
            skLineSegment(sketch, "E311", {"start": v(9.23, 21.23) * mm, "end": v(-9.22, 21.23) * mm});
            skLineSegment(sketch, "E312", {"start": v(-9.23, 22.46) * mm, "end": v(9.23, 22.46) * mm});
            skLineSegment(sketch, "E313", {"start": v(9.23, 23.69) * mm, "end": v(-9.22, 23.69) * mm});
            skLineSegment(sketch, "E314", {"start": v(-9.22, 24.92) * mm, "end": v(9.23, 24.92) * mm});
            skLineSegment(sketch, "E315", {"start": v(9.23, 26.15) * mm, "end": v(-9.22, 26.15) * mm});
            skLineSegment(sketch, "E316", {"start": v(-9.23, 27.38) * mm, "end": v(9.23, 27.38) * mm});
            skLineSegment(sketch, "E317", {"start": v(9.23, 28.6) * mm, "end": v(-9.22, 28.6) * mm});
            skArc(sketch, "E318", {"start": v(9.23, 10.16) * mm, "mid": v(9.84, 10.77) * mm, "end": v(9.23, 11.39) * mm});
            skArc(sketch, "E319", {"start": v(-9.23, 12.62) * mm, "mid": v(-9.84, 12) * mm, "end": v(-9.22, 11.39) * mm});
            skArc(sketch, "E320", {"start": v(9.23, 12.62) * mm, "mid": v(9.84, 13.24) * mm, "end": v(9.23, 13.85) * mm});
            skArc(sketch, "E321", {"start": v(-9.22, 15.08) * mm, "mid": v(-9.84, 14.46) * mm, "end": v(-9.22, 13.85) * mm});
            skArc(sketch, "E322", {"start": v(9.23, 15.08) * mm, "mid": v(9.84, 15.7) * mm, "end": v(9.23, 16.31) * mm});
            skArc(sketch, "E323", {"start": v(9.23, 17.54) * mm, "mid": v(9.84, 18.16) * mm, "end": v(9.23, 18.77) * mm});
            skArc(sketch, "E324", {"start": v(-9.22, 17.54) * mm, "mid": v(-9.84, 16.93) * mm, "end": v(-9.22, 16.3) * mm});
            skArc(sketch, "E325", {"start": v(9.23, 20) * mm, "mid": v(9.84, 20.61) * mm, "end": v(9.23, 21.23) * mm});
            skArc(sketch, "E326", {"start": v(9.23, 22.46) * mm, "mid": v(9.84, 23.07) * mm, "end": v(9.23, 23.69) * mm});
            skArc(sketch, "E327", {"start": v(9.23, 24.92) * mm, "mid": v(9.84, 25.53) * mm, "end": v(9.23, 26.15) * mm});
            skArc(sketch, "E328", {"start": v(-9.22, 22.46) * mm, "mid": v(-9.84, 21.84) * mm, "end": v(-9.22, 21.23) * mm});
            skArc(sketch, "E329", {"start": v(-9.22, 24.92) * mm, "mid": v(-9.84, 24.3) * mm, "end": v(-9.22, 23.69) * mm});
            skArc(sketch, "E330", {"start": v(-9.22, 29.84) * mm, "mid": v(-9.84, 29.22) * mm, "end": v(-9.22, 28.6) * mm});
            skArc(sketch, "E331", {"start": v(-9.22, 20) * mm, "mid": v(-9.84, 19.38) * mm, "end": v(-9.22, 18.77) * mm});
            skArc(sketch, "E332", {"start": v(-9.23, 27.38) * mm, "mid": v(-9.84, 26.76) * mm, "end": v(-9.22, 26.15) * mm});
            skLineSegment(sketch, "E333", {"start": v(-9.22, 29.84) * mm, "end": v(10, 29.84) * mm});
            skArc(sketch, "E334", {"start": v(9.23, 27.38) * mm, "mid": v(9.84, 28) * mm, "end": v(9.23, 28.6) * mm});
            skLineSegment(sketch, "E335.MirrorCS", {"start": v(10, 9.84) * mm, "end": v(10, 10) * mm});
            skLineSegment(sketch, "E336.MirrorCS", {"start": v(-10, 10) * mm, "end": v(-10, 9.84) * mm});
            skLineSegment(sketch, "E337.MirrorCS", {"start": v(9.84, 9.84) * mm, "end": v(9.84, 10) * mm});
            skLineSegment(sketch, "E338.MirrorCS", {"start": v(-9.84, 9.84) * mm, "end": v(-9.84, 10) * mm});
            skLineSegment(sketch, "E339.MirrorCS", {"start": v(-9.84, -10) * mm, "end": v(-9.23, -10) * mm});
            skLineSegment(sketch, "E340.MirrorCS", {"start": v(-10, -9.84) * mm, "end": v(-10, -10) * mm});
            skLineSegment(sketch, "E341.MirrorCS", {"start": v(9.84, -10) * mm, "end": v(9.84, -9.84) * mm});
            skLineSegment(sketch, "E342.MirrorCS", {"start": v(-9.84, -10) * mm, "end": v(-9.84, -9.84) * mm});
            skLineSegment(sketch, "E343.MirrorCS", {"start": v(10, -10) * mm, "end": v(9.84, -10) * mm});
            skLineSegment(sketch, "E344.MirrorCS", {"start": v(-9.84, -10) * mm, "end": v(-10, -10) * mm});
            skLineSegment(sketch, "E345.MirrorCS", {"start": v(10, -10) * mm, "end": v(10, -9.84) * mm});
            skLineSegment(sketch, "E346.MirrorCS", {"start": v(-9.23, -10) * mm, "end": v(-9.23, -9.84) * mm});
            skLineSegment(sketch, "E347.MirrorCS", {"start": v(9.23, 9.84) * mm, "end": v(9.23, 10) * mm});
            skLineSegment(sketch, "E348.MirrorCS", {"start": v(9.84, -10) * mm, "end": v(9.23, -10) * mm});
            skLineSegment(sketch, "E349.MirrorCS", {"start": v(-9.22, 9.84) * mm, "end": v(-9.22, 10) * mm});
            skLineSegment(sketch, "E350.MirrorCS", {"start": v(9.23, -10) * mm, "end": v(9.23, -9.84) * mm});
            skLineSegment(sketch, "E351.MirrorCS", {"start": v(9.84, 3.69) * mm, "end": v(9.84, 4.92) * mm});
            skLineSegment(sketch, "E352.MirrorCS", {"start": v(-10, 8.61) * mm, "end": v(-10, 7.38) * mm});
            skLineSegment(sketch, "E353.MirrorCS", {"start": v(-10, -1.23) * mm, "end": v(-10, -2.46) * mm});
            skLineSegment(sketch, "E354.MirrorCS", {"start": v(-9.22, -4.92) * mm, "end": v(9.23, -4.92) * mm});
            skLineSegment(sketch, "E355.MirrorCS", {"start": v(-9.22, 7.38) * mm, "end": v(-9.22, 8.61) * mm});
            skLineSegment(sketch, "E356.MirrorCS", {"start": v(10, -9.84) * mm, "end": v(-10, -9.84) * mm});
            skLineSegment(sketch, "E357.MirrorCS", {"start": v(-9.84, 2.46) * mm, "end": v(-9.84, 3.69) * mm});
            skLineSegment(sketch, "E358.MirrorCS", {"start": v(10, 9.84) * mm, "end": v(-10, 9.84) * mm});
            skLineSegment(sketch, "E359.MirrorCS", {"start": v(10, 0) * mm, "end": v(-10, 0) * mm});
            skLineSegment(sketch, "E360.MirrorCS", {"start": v(9.23, -6.15) * mm, "end": v(-9.22, -6.15) * mm});
            skLineSegment(sketch, "E361.MirrorCS", {"start": v(9.23, -6.15) * mm, "end": v(9.23, -4.92) * mm});
            skLineSegment(sketch, "E362.MirrorCS", {"start": v(-10, 9.84) * mm, "end": v(-10, 8.61) * mm});
            skLineSegment(sketch, "E363.MirrorCS", {"start": v(-10, 0) * mm, "end": v(-10, -1.23) * mm});
            skLineSegment(sketch, "E364.MirrorCS", {"start": v(-9.23, -9.84) * mm, "end": v(-9.23, -8.6) * mm});
            skLineSegment(sketch, "E365.MirrorCS", {"start": v(9.84, 6.15) * mm, "end": v(9.84, 7.38) * mm});
            skLineSegment(sketch, "E366.MirrorCS", {"start": v(-9.23, -7.38) * mm, "end": v(9.23, -7.38) * mm});
            skLineSegment(sketch, "E367.MirrorCS", {"start": v(10, 1.23) * mm, "end": v(-10, 1.23) * mm});
            skLineSegment(sketch, "E368.MirrorCS", {"start": v(10, -8.6) * mm, "end": v(-10, -8.6) * mm});
            skLineSegment(sketch, "E369.MirrorCS", {"start": v(9.23, -3.69) * mm, "end": v(9.23, -2.46) * mm});
            skLineSegment(sketch, "E370.MirrorCS", {"start": v(-9.84, 4.92) * mm, "end": v(-9.84, 6.15) * mm});
            skLineSegment(sketch, "E371.MirrorCS", {"start": v(-10, 1.23) * mm, "end": v(-10, 0) * mm});
            skLineSegment(sketch, "E372.MirrorCS", {"start": v(-10, -8.6) * mm, "end": v(-10, -9.84) * mm});
            skLineSegment(sketch, "E373.MirrorCS", {"start": v(-9.23, -7.38) * mm, "end": v(-9.23, -6.15) * mm});
            skLineSegment(sketch, "E374.MirrorCS", {"start": v(9.84, 8.61) * mm, "end": v(9.84, 9.84) * mm});
            skLineSegment(sketch, "E375.MirrorCS", {"start": v(10, 2.46) * mm, "end": v(-10, 2.46) * mm});
            skLineSegment(sketch, "E376.MirrorCS", {"start": v(9.23, -1.23) * mm, "end": v(9.23, 0) * mm});
            skLineSegment(sketch, "E377.MirrorCS", {"start": v(-9.84, 7.38) * mm, "end": v(-9.84, 8.61) * mm});
            skLineSegment(sketch, "E378.MirrorCS", {"start": v(9.23, 8.61) * mm, "end": v(-9.22, 8.61) * mm});
            skLineSegment(sketch, "E379.MirrorCS", {"start": v(9.84, -8.6) * mm, "end": v(9.84, -7.38) * mm});
            skLineSegment(sketch, "E380.MirrorCS", {"start": v(-10, 2.46) * mm, "end": v(-10, 1.23) * mm});
            skLineSegment(sketch, "E381.MirrorCS", {"start": v(-10, -7.38) * mm, "end": v(-10, -8.6) * mm});
            skLineSegment(sketch, "E382.MirrorCS", {"start": v(-9.23, -4.92) * mm, "end": v(-9.23, -3.69) * mm});
            skLineSegment(sketch, "E383.MirrorCS", {"start": v(-9.23, 7.38) * mm, "end": v(9.23, 7.38) * mm});
            skLineSegment(sketch, "E384.MirrorCS", {"start": v(9.84, -6.15) * mm, "end": v(9.84, -4.92) * mm});
            skLineSegment(sketch, "E385.MirrorCS", {"start": v(-10, 3.69) * mm, "end": v(-10, 2.46) * mm});
            skLineSegment(sketch, "E386.MirrorCS", {"start": v(-10, -6.15) * mm, "end": v(-10, -7.38) * mm});
            skLineSegment(sketch, "E387.MirrorCS", {"start": v(-9.22, 4.92) * mm, "end": v(9.23, 4.92) * mm});
            skLineSegment(sketch, "E388.MirrorCS", {"start": v(-9.22, -2.46) * mm, "end": v(-9.22, -1.23) * mm});
            skLineSegment(sketch, "E389.MirrorCS", {"start": v(10, 3.69) * mm, "end": v(-10, 3.69) * mm});
            skLineSegment(sketch, "E390.MirrorCS", {"start": v(9.23, 1.23) * mm, "end": v(9.23, 2.46) * mm});
            skLineSegment(sketch, "E391.MirrorCS", {"start": v(-9.84, -9.84) * mm, "end": v(-9.84, -8.6) * mm});
            skLineSegment(sketch, "E392.MirrorCS", {"start": v(9.23, 6.15) * mm, "end": v(-9.22, 6.15) * mm});
            skLineSegment(sketch, "E393.MirrorCS", {"start": v(-9.84, -7.38) * mm, "end": v(-9.84, -6.15) * mm});
            skLineSegment(sketch, "E394.MirrorCS", {"start": v(9.23, 3.69) * mm, "end": v(9.23, 4.92) * mm});
            skLineSegment(sketch, "E395.MirrorCS", {"start": v(9.84, -3.69) * mm, "end": v(9.84, -2.46) * mm});
            skLineSegment(sketch, "E396.MirrorCS", {"start": v(-10, 4.92) * mm, "end": v(-10, 3.69) * mm});
            skLineSegment(sketch, "E397.MirrorCS", {"start": v(-10, -4.92) * mm, "end": v(-10, -6.15) * mm});
            skLineSegment(sketch, "E398.MirrorCS", {"start": v(-9.22, 0) * mm, "end": v(-9.22, 1.23) * mm});
            skLineSegment(sketch, "E399.MirrorCS", {"start": v(-9.84, -4.92) * mm, "end": v(-9.84, -3.69) * mm});
            skLineSegment(sketch, "E400.MirrorCS", {"start": v(10, -3.69) * mm, "end": v(-10, -3.69) * mm});
            skLineSegment(sketch, "E401.MirrorCS", {"start": v(9.23, 6.15) * mm, "end": v(9.23, 7.38) * mm});
            skLineSegment(sketch, "E402.MirrorCS", {"start": v(10, 3.69) * mm, "end": v(10, 4.92) * mm});
            skLineSegment(sketch, "E403.MirrorCS", {"start": v(-9.22, 2.46) * mm, "end": v(-9.22, 3.69) * mm});
            skLineSegment(sketch, "E404.MirrorCS", {"start": v(9.84, -1.23) * mm, "end": v(9.84, 0) * mm});
            skLineSegment(sketch, "E405.MirrorCS", {"start": v(9.23, 8.61) * mm, "end": v(9.23, 9.84) * mm});
            skLineSegment(sketch, "E406.MirrorCS", {"start": v(-9.84, -2.46) * mm, "end": v(-9.84, -1.23) * mm});
            skLineSegment(sketch, "E407.MirrorCS", {"start": v(10, 6.15) * mm, "end": v(10, 7.38) * mm});
            skLineSegment(sketch, "E408.MirrorCS", {"start": v(10, 0) * mm, "end": v(10, 1.23) * mm});
            skLineSegment(sketch, "E409.MirrorCS", {"start": v(-10, 6.15) * mm, "end": v(-10, 4.92) * mm});
            skLineSegment(sketch, "E410.MirrorCS", {"start": v(10, 1.23) * mm, "end": v(10, 2.46) * mm});
            skLineSegment(sketch, "E411.MirrorCS", {"start": v(10, -2.46) * mm, "end": v(-10, -2.46) * mm});
            skLineSegment(sketch, "E412.MirrorCS", {"start": v(10, 4.92) * mm, "end": v(10, 6.15) * mm});
            skLineSegment(sketch, "E413.MirrorCS", {"start": v(-10, -3.69) * mm, "end": v(-10, -4.92) * mm});
            skLineSegment(sketch, "E414.MirrorCS", {"start": v(9.23, -1.23) * mm, "end": v(-9.22, -1.23) * mm});
            skLineSegment(sketch, "E415.MirrorCS", {"start": v(-9.84, 0) * mm, "end": v(-9.84, 1.23) * mm});
            skLineSegment(sketch, "E416.MirrorCS", {"start": v(10, 2.46) * mm, "end": v(10, 3.69) * mm});
            skLineSegment(sketch, "E417.MirrorCS", {"start": v(-9.22, 4.92) * mm, "end": v(-9.22, 6.15) * mm});
            skLineSegment(sketch, "E418.MirrorCS", {"start": v(9.23, -8.6) * mm, "end": v(9.23, -7.38) * mm});
            skLineSegment(sketch, "E419.MirrorCS", {"start": v(-9.84, 1.23) * mm, "end": v(-9.84, 2.46) * mm});
            skLineSegment(sketch, "E420.MirrorCS", {"start": v(9.23, -7.38) * mm, "end": v(9.23, -6.15) * mm});
            skArc(sketch, "E421.MirrorCS", {"start": v(-9.22, -9.84) * mm, "mid": v(-9.84, -9.22) * mm, "end": v(-9.22, -8.6) * mm});
            skLineSegment(sketch, "E422.MirrorCS", {"start": v(9.84, 4.92) * mm, "end": v(9.84, 6.15) * mm});
            skLineSegment(sketch, "E423.MirrorCS", {"start": v(-9.22, 8.61) * mm, "end": v(-9.22, 9.84) * mm});
            skArc(sketch, "E424.MirrorCS", {"start": v(-9.22, 0) * mm, "mid": v(-9.84, 0.62) * mm, "end": v(-9.22, 1.23) * mm});
            skLineSegment(sketch, "E425.MirrorCS", {"start": v(9.23, -4.92) * mm, "end": v(9.23, -3.69) * mm});
            skLineSegment(sketch, "E426.MirrorCS", {"start": v(-9.84, 3.69) * mm, "end": v(-9.84, 4.92) * mm});
            skArc(sketch, "E427.MirrorCS", {"start": v(-9.23, -7.38) * mm, "mid": v(-9.84, -6.76) * mm, "end": v(-9.22, -6.15) * mm});
            skLineSegment(sketch, "E428.MirrorCS", {"start": v(-9.23, -8.6) * mm, "end": v(-9.23, -7.38) * mm});
            skLineSegment(sketch, "E429.MirrorCS", {"start": v(9.84, 7.38) * mm, "end": v(9.84, 8.61) * mm});
            skLineSegment(sketch, "E430.MirrorCS", {"start": v(-9.22, -9.84) * mm, "end": v(10, -9.84) * mm});
            skLineSegment(sketch, "E431.MirrorCS", {"start": v(9.23, -8.6) * mm, "end": v(-9.22, -8.6) * mm});
            skLineSegment(sketch, "E432.MirrorCS", {"start": v(-10, 9.84) * mm, "end": v(9.23, 9.84) * mm});
            skLineSegment(sketch, "E433.MirrorCS", {"start": v(9.23, -2.46) * mm, "end": v(9.23, -1.23) * mm});
            skLineSegment(sketch, "E434.MirrorCS", {"start": v(-9.84, 6.15) * mm, "end": v(-9.84, 7.38) * mm});
            skArc(sketch, "E435.MirrorCS", {"start": v(9.23, -7.38) * mm, "mid": v(9.84, -8) * mm, "end": v(9.23, -8.6) * mm});
            skArc(sketch, "E436.MirrorCS", {"start": v(9.23, 9.84) * mm, "mid": v(9.84, 9.23) * mm, "end": v(9.23, 8.61) * mm});
            skLineSegment(sketch, "E437.MirrorCS", {"start": v(9.84, -9.84) * mm, "end": v(9.84, -8.6) * mm});
            skLineSegment(sketch, "E438.MirrorCS", {"start": v(10, -7.38) * mm, "end": v(-10, -7.38) * mm});
            skLineSegment(sketch, "E439.MirrorCS", {"start": v(-9.23, -6.15) * mm, "end": v(-9.23, -4.92) * mm});
            skArc(sketch, "E440.MirrorCS", {"start": v(-9.23, 7.38) * mm, "mid": v(-9.84, 8) * mm, "end": v(-9.22, 8.61) * mm});
            skLineSegment(sketch, "E441.MirrorCS", {"start": v(9.23, 0) * mm, "end": v(9.23, 1.23) * mm});
            skLineSegment(sketch, "E442.MirrorCS", {"start": v(-9.84, 8.61) * mm, "end": v(-9.84, 9.84) * mm});
            skArc(sketch, "E443.MirrorCS", {"start": v(9.23, 7.38) * mm, "mid": v(9.84, 6.76) * mm, "end": v(9.23, 6.15) * mm});
            skLineSegment(sketch, "E444.MirrorCS", {"start": v(-9.84, -8.6) * mm, "end": v(-9.84, -7.38) * mm});
            skLineSegment(sketch, "E445.MirrorCS", {"start": v(9.23, 2.46) * mm, "end": v(9.23, 3.69) * mm});
            skArc(sketch, "E446.MirrorCS", {"start": v(9.23, 4.92) * mm, "mid": v(9.84, 4.3) * mm, "end": v(9.23, 3.69) * mm});
            skLineSegment(sketch, "E447.MirrorCS", {"start": v(9.84, -7.38) * mm, "end": v(9.84, -6.15) * mm});
            skLineSegment(sketch, "E448.MirrorCS", {"start": v(10, -6.15) * mm, "end": v(-10, -6.15) * mm});
            skLineSegment(sketch, "E449.MirrorCS", {"start": v(-9.22, -3.69) * mm, "end": v(-9.22, -2.46) * mm});
            skArc(sketch, "E450.MirrorCS", {"start": v(-9.22, 4.92) * mm, "mid": v(-9.84, 5.54) * mm, "end": v(-9.22, 6.15) * mm});
            skLineSegment(sketch, "E451.MirrorCS", {"start": v(9.84, -4.92) * mm, "end": v(9.84, -3.69) * mm});
            skLineSegment(sketch, "E452.MirrorCS", {"start": v(10, 4.92) * mm, "end": v(-10, 4.92) * mm});
            skLineSegment(sketch, "E453.MirrorCS", {"start": v(10, -4.92) * mm, "end": v(-10, -4.92) * mm});
            skLineSegment(sketch, "E454.MirrorCS", {"start": v(9.23, 3.69) * mm, "end": v(-9.22, 3.69) * mm});
            skLineSegment(sketch, "E455.MirrorCS", {"start": v(-9.22, -1.23) * mm, "end": v(-9.22, 0) * mm});
            skArc(sketch, "E456.MirrorCS", {"start": v(9.23, 2.46) * mm, "mid": v(9.84, 1.84) * mm, "end": v(9.23, 1.23) * mm});
            skLineSegment(sketch, "E457.MirrorCS", {"start": v(-9.84, -6.15) * mm, "end": v(-9.84, -4.92) * mm});
            skLineSegment(sketch, "E458.MirrorCS", {"start": v(-9.22, 2.46) * mm, "end": v(9.23, 2.46) * mm});
            skLineSegment(sketch, "E459.MirrorCS", {"start": v(9.23, 4.92) * mm, "end": v(9.23, 6.15) * mm});
            skArc(sketch, "E460.MirrorCS", {"start": v(-9.22, 2.46) * mm, "mid": v(-9.84, 3.08) * mm, "end": v(-9.22, 3.7) * mm});
            skLineSegment(sketch, "E461.MirrorCS", {"start": v(9.84, -2.46) * mm, "end": v(9.84, -1.23) * mm});
            skLineSegment(sketch, "E462.MirrorCS", {"start": v(10, 6.15) * mm, "end": v(-10, 6.15) * mm});
            skLineSegment(sketch, "E463.MirrorCS", {"start": v(9.23, 1.23) * mm, "end": v(-9.22, 1.23) * mm});
            skLineSegment(sketch, "E464.MirrorCS", {"start": v(-9.22, 1.23) * mm, "end": v(-9.22, 2.46) * mm});
            skArc(sketch, "E465.MirrorCS", {"start": v(9.23, 0) * mm, "mid": v(9.84, -0.61) * mm, "end": v(9.23, -1.23) * mm});
            skLineSegment(sketch, "E466.MirrorCS", {"start": v(-9.22, 0) * mm, "end": v(9.23, 0) * mm});
            skLineSegment(sketch, "E467.MirrorCS", {"start": v(9.23, 7.38) * mm, "end": v(9.23, 8.61) * mm});
            skArc(sketch, "E468.MirrorCS", {"start": v(9.23, -2.46) * mm, "mid": v(9.84, -3.07) * mm, "end": v(9.23, -3.69) * mm});
            skLineSegment(sketch, "E469.MirrorCS", {"start": v(-9.84, -1.23) * mm, "end": v(-9.84, 0) * mm});
            skLineSegment(sketch, "E470.MirrorCS", {"start": v(10, 7.38) * mm, "end": v(10, 8.6) * mm});
            skLineSegment(sketch, "E471.MirrorCS", {"start": v(10, 8.6) * mm, "end": v(10, 9.84) * mm});
            skLineSegment(sketch, "E472.MirrorCS", {"start": v(-9.23, -2.46) * mm, "end": v(9.23, -2.46) * mm});
            skLineSegment(sketch, "E473.MirrorCS", {"start": v(10, -2.46) * mm, "end": v(10, -1.23) * mm});
            skLineSegment(sketch, "E474.MirrorCS", {"start": v(-10, -2.46) * mm, "end": v(-10, -3.69) * mm});
            skLineSegment(sketch, "E475.MirrorCS", {"start": v(10, 8.61) * mm, "end": v(-10, 8.61) * mm});
            skLineSegment(sketch, "E476.MirrorCS", {"start": v(-9.22, 6.15) * mm, "end": v(-9.22, 7.38) * mm});
            skLineSegment(sketch, "E477.MirrorCS", {"start": v(10, -4.92) * mm, "end": v(10, -3.69) * mm});
            skLineSegment(sketch, "E478.MirrorCS", {"start": v(10, -3.69) * mm, "end": v(10, -2.46) * mm});
            skLineSegment(sketch, "E479.MirrorCS", {"start": v(10, -6.15) * mm, "end": v(10, -4.92) * mm});
            skLineSegment(sketch, "E480.MirrorCS", {"start": v(10, 10) * mm, "end": v(10, -10) * mm});
            skLineSegment(sketch, "E481.MirrorCS", {"start": v(10, -7.38) * mm, "end": v(10, -6.15) * mm});
            skArc(sketch, "E482.MirrorCS", {"start": v(-9.22, -2.46) * mm, "mid": v(-9.84, -1.84) * mm, "end": v(-9.22, -1.23) * mm});
            skLineSegment(sketch, "E483.MirrorCS", {"start": v(-9.22, 3.69) * mm, "end": v(-9.22, 4.92) * mm});
            skLineSegment(sketch, "E484.MirrorCS", {"start": v(10, -8.6) * mm, "end": v(10, -7.38) * mm});
            skLineSegment(sketch, "E485.MirrorCS", {"start": v(10, -9.84) * mm, "end": v(10, -8.6) * mm});
            skLineSegment(sketch, "E486.MirrorCS", {"start": v(-10, 10) * mm, "end": v(-10, -10) * mm});
            skPoint(sketch, "E487.MirrorP", {"position": v(0, 0) * mm});
            skLineSegment(sketch, "E488.MirrorCS", {"start": v(9.84, 2.46) * mm, "end": v(9.84, 3.69) * mm});
            skLineSegment(sketch, "E489.MirrorCS", {"start": v(10, -1.23) * mm, "end": v(10, 0) * mm});
            skArc(sketch, "E490.MirrorCS", {"start": v(9.23, -4.92) * mm, "mid": v(9.84, -5.53) * mm, "end": v(9.23, -6.15) * mm});
            skLineSegment(sketch, "E491.MirrorCS", {"start": v(10, 7.38) * mm, "end": v(-10, 7.38) * mm});
            skLineSegment(sketch, "E492.MirrorCS", {"start": v(-9.84, -3.69) * mm, "end": v(-9.84, -2.46) * mm});
            skLineSegment(sketch, "E493.MirrorCS", {"start": v(10, -1.23) * mm, "end": v(-10, -1.23) * mm});
            skLineSegment(sketch, "E494.MirrorCS", {"start": v(9.84, 0) * mm, "end": v(9.84, 1.23) * mm});
            skLineSegment(sketch, "E495.MirrorCS", {"start": v(10, -10) * mm, "end": v(-10, -10) * mm});
            skLineSegment(sketch, "E496.MirrorCS", {"start": v(-10, 7.38) * mm, "end": v(-10, 6.15) * mm});
            skArc(sketch, "E497.MirrorCS", {"start": v(-9.22, -4.92) * mm, "mid": v(-9.84, -4.3) * mm, "end": v(-9.22, -3.69) * mm});
            skLineSegment(sketch, "E498.MirrorCS", {"start": v(9.23, -9.84) * mm, "end": v(9.23, -8.6) * mm});
            skLineSegment(sketch, "E499.MirrorCS", {"start": v(9.84, 1.23) * mm, "end": v(9.84, 2.46) * mm});
            skLineSegment(sketch, "E500.MirrorCS", {"start": v(9.23, -3.69) * mm, "end": v(-9.22, -3.69) * mm});
            skSolve(sketch);
        }
        {
            var Q0;
            Q0=sQuery(id+"F6.wireOp",VERTEX,"E358.MirrorCS.end");
            var Q1;
            Q1=sQuery(id+"F6.wireOp",EDGE,"E358.MirrorCS");
            cPlane(context, id + "F7", {"entities" : qUnion([Q0, Q1]), "cplaneType" : CPlaneType.LINE_POINT, "offset" : 25 * mm, "width" : 150 * mm, "height" : 150 * mm});
        }
        {
            var Q0;
            Q0=qCreatedBy(id+"F7.planeOp",FACE);
            var sketch = newSketch(context, id + "F8", { "sketchPlane" : qUnion([Q0])});
            skCircle(sketch, "E501", {"center": v(-9.84, 0.62) * mm, "radius": 0.2 * mm});
            skSolve(sketch);
        }
        {
            var Q0;
            Q0=makeQuery(id+"F8.imprint","IMPRINT",FACE,{"disambiguationData":[TD([[makeQuery(id+"F8.imprint","IMPRINT",EDGE,{"derivedFrom":sQuery(id+"F8.wireOp",EDGE,"E501")}),1.0]])]});
            var Q1;
            Q1=sQuery(id+"F6.wireOp",EDGE,"E432.MirrorCS");
            var Q2;
            Q2=sQuery(id+"F6.wireOp",EDGE,"E436.MirrorCS");
            var Q3;
            Q3=sQuery(id+"F6.wireOp",EDGE,"E378.MirrorCS");
            var Q4;
            Q4=sQuery(id+"F6.wireOp",EDGE,"E440.MirrorCS");
            var Q5;
            Q5=sQuery(id+"F6.wireOp",EDGE,"E383.MirrorCS");
            var Q6;
            Q6=sQuery(id+"F6.wireOp",EDGE,"E443.MirrorCS");
            var Q7;
            Q7=sQuery(id+"F6.wireOp",EDGE,"E392.MirrorCS");
            var Q8;
            Q8=sQuery(id+"F6.wireOp",EDGE,"E450.MirrorCS");
            var Q9;
            Q9=sQuery(id+"F6.wireOp",EDGE,"E387.MirrorCS");
            var Q10;
            Q10=sQuery(id+"F6.wireOp",EDGE,"E446.MirrorCS");
            var Q11;
            Q11=sQuery(id+"F6.wireOp",EDGE,"E454.MirrorCS");
            var Q12;
            Q12=sQuery(id+"F6.wireOp",EDGE,"E460.MirrorCS");
            var Q13;
            Q13=sQuery(id+"F6.wireOp",EDGE,"E458.MirrorCS");
            var Q14;
            Q14=sQuery(id+"F6.wireOp",EDGE,"E456.MirrorCS");
            var Q15;
            Q15=sQuery(id+"F6.wireOp",EDGE,"E463.MirrorCS");
            var Q16;
            Q16=sQuery(id+"F6.wireOp",EDGE,"E424.MirrorCS");
            var Q17;
            Q17=sQuery(id+"F6.wireOp",EDGE,"E466.MirrorCS");
            var Q18;
            Q18=sQuery(id+"F6.wireOp",EDGE,"E465.MirrorCS");
            var Q19;
            Q19=sQuery(id+"F6.wireOp",EDGE,"E414.MirrorCS");
            var Q20;
            Q20=sQuery(id+"F6.wireOp",EDGE,"E482.MirrorCS");
            var Q21;
            Q21=sQuery(id+"F6.wireOp",EDGE,"E472.MirrorCS");
            var Q22;
            Q22=sQuery(id+"F6.wireOp",EDGE,"E468.MirrorCS");
            var Q23;
            Q23=sQuery(id+"F6.wireOp",EDGE,"E500.MirrorCS");
            var Q24;
            Q24=sQuery(id+"F6.wireOp",EDGE,"E497.MirrorCS");
            var Q25;
            Q25=sQuery(id+"F6.wireOp",EDGE,"E354.MirrorCS");
            var Q26;
            Q26=sQuery(id+"F6.wireOp",EDGE,"E490.MirrorCS");
            var Q27;
            Q27=sQuery(id+"F6.wireOp",EDGE,"E360.MirrorCS");
            var Q28;
            Q28=sQuery(id+"F6.wireOp",EDGE,"E427.MirrorCS");
            var Q29;
            Q29=sQuery(id+"F6.wireOp",EDGE,"E366.MirrorCS");
            var Q30;
            Q30=sQuery(id+"F6.wireOp",EDGE,"E435.MirrorCS");
            var Q31;
            Q31=sQuery(id+"F6.wireOp",EDGE,"E431.MirrorCS");
            var Q32;
            Q32=sQuery(id+"F6.wireOp",EDGE,"E421.MirrorCS");
            var Q33;
            Q33=sQuery(id+"F6.wireOp",EDGE,"E430.MirrorCS");
            sweep(context, id + "F9", {"profiles" : qUnion([Q0]), "path" : qUnion([Q1, Q2, Q3, Q4, Q5, Q6, Q7, Q8, Q9, Q10, Q11, Q12, Q13, Q14, Q15, Q16, Q17, Q18, Q19, Q20, Q21, Q22, Q23, Q24, Q25, Q26, Q27, Q28, Q29, Q30, Q31, Q32, Q33])});
        }
        {
            var Q0;
            Q0=qCreatedBy(id+"F5.planeOp",FACE);
            cPlane(context, id + "F10", {"entities" : qUnion([Q0]), "cplaneType" : CPlaneType.OFFSET, "offset" : getVariable(context, 'd'), "width" : 150 * mm, "height" : 150 * mm});
        }
        {
            var Q0;
            Q0=qCreatedBy(id+"F10.planeOp",FACE);
            var sketch = newSketch(context, id + "F11", { "sketchPlane" : qUnion([Q0])});
            skLineSegment(sketch, "E502.bottom", {"start": v(10, 10) * mm, "end": v(-10, 10) * mm});
            skLineSegment(sketch, "E502.top", {"start": v(10, -10) * mm, "end": v(-10, -10) * mm});
            skLineSegment(sketch, "E502.left", {"start": v(10, 10) * mm, "end": v(10, -10) * mm});
            skLineSegment(sketch, "E502.right", {"start": v(-10, 10) * mm, "end": v(-10, -10) * mm});
            skPoint(sketch, "E502.middle", {"position": v(0, 0) * mm});
            skLineSegment(sketch, "E503", {"start": v(-10, 10) * mm, "end": v(-9.84, 10) * mm});
            skLineSegment(sketch, "E504", {"start": v(-9.84, 10) * mm, "end": v(-8.61, 10) * mm});
            skLineSegment(sketch, "E505", {"start": v(-8.61, 10) * mm, "end": v(-7.38, 10) * mm});
            skLineSegment(sketch, "E506", {"start": v(-7.38, 10) * mm, "end": v(-6.15, 10) * mm});
            skLineSegment(sketch, "E507", {"start": v(-6.15, 10) * mm, "end": v(-4.92, 10) * mm});
            skLineSegment(sketch, "E508", {"start": v(-4.92, 10) * mm, "end": v(-3.7, 10) * mm});
            skLineSegment(sketch, "E509", {"start": v(-3.7, 10) * mm, "end": v(-2.46, 10) * mm});
            skLineSegment(sketch, "E510", {"start": v(-2.46, 10) * mm, "end": v(-1.23, 10) * mm});
            skLineSegment(sketch, "E511", {"start": v(-1.23, 10) * mm, "end": v(0, 10) * mm});
            skLineSegment(sketch, "E512", {"start": v(0, 10) * mm, "end": v(1.23, 10) * mm});
            skLineSegment(sketch, "E513", {"start": v(1.23, 10) * mm, "end": v(2.46, 10) * mm});
            skLineSegment(sketch, "E514", {"start": v(2.46, 10) * mm, "end": v(3.69, 10) * mm});
            skLineSegment(sketch, "E515", {"start": v(3.69, 10) * mm, "end": v(4.92, 10) * mm});
            skLineSegment(sketch, "E516", {"start": v(4.92, 10) * mm, "end": v(6.15, 10) * mm});
            skLineSegment(sketch, "E517", {"start": v(6.15, 10) * mm, "end": v(7.38, 10) * mm});
            skLineSegment(sketch, "E518", {"start": v(7.38, 10) * mm, "end": v(8.6, 10) * mm});
            skLineSegment(sketch, "E519", {"start": v(8.6, 10) * mm, "end": v(9.84, 10) * mm});
            skLineSegment(sketch, "E520", {"start": v(9.84, 10) * mm, "end": v(10, 10) * mm});
            skLineSegment(sketch, "E521", {"start": v(-9.84, 10) * mm, "end": v(-9.84, -10) * mm});
            skLineSegment(sketch, "E522", {"start": v(-9.84, -10) * mm, "end": v(-10, -10) * mm});
            skLineSegment(sketch, "E523", {"start": v(-8.61, 10) * mm, "end": v(-8.61, -10) * mm});
            skLineSegment(sketch, "E524", {"start": v(-8.61, -10) * mm, "end": v(-9.84, -10) * mm});
            skLineSegment(sketch, "E525", {"start": v(-7.38, 10) * mm, "end": v(-7.38, -10) * mm});
            skLineSegment(sketch, "E526", {"start": v(-7.38, -10) * mm, "end": v(-8.61, -10) * mm});
            skLineSegment(sketch, "E527", {"start": v(-6.15, 10) * mm, "end": v(-6.15, -10) * mm});
            skLineSegment(sketch, "E528", {"start": v(-6.15, -10) * mm, "end": v(-7.38, -10) * mm});
            skLineSegment(sketch, "E529", {"start": v(-4.92, 10) * mm, "end": v(-4.92, -10) * mm});
            skLineSegment(sketch, "E530", {"start": v(-4.92, -10) * mm, "end": v(-6.15, -10) * mm});
            skLineSegment(sketch, "E531", {"start": v(-3.7, 10) * mm, "end": v(-3.7, -10) * mm});
            skLineSegment(sketch, "E532", {"start": v(-3.7, -10) * mm, "end": v(-4.92, -10) * mm});
            skLineSegment(sketch, "E533", {"start": v(-2.46, 10) * mm, "end": v(-2.46, -10) * mm});
            skLineSegment(sketch, "E534", {"start": v(-2.46, -10) * mm, "end": v(-3.7, -10) * mm});
            skLineSegment(sketch, "E535", {"start": v(-1.23, 10) * mm, "end": v(-1.23, -10) * mm});
            skLineSegment(sketch, "E536", {"start": v(-1.23, -10) * mm, "end": v(-2.46, -10) * mm});
            skLineSegment(sketch, "E537", {"start": v(0, 10) * mm, "end": v(0, -10) * mm});
            skLineSegment(sketch, "E538", {"start": v(0, -10) * mm, "end": v(-1.23, -10) * mm});
            skLineSegment(sketch, "E539", {"start": v(1.23, 10) * mm, "end": v(1.23, -10) * mm});
            skLineSegment(sketch, "E540", {"start": v(1.23, -10) * mm, "end": v(0, -10) * mm});
            skLineSegment(sketch, "E541", {"start": v(2.46, 10) * mm, "end": v(2.46, -10) * mm});
            skLineSegment(sketch, "E542", {"start": v(2.46, -10) * mm, "end": v(1.23, -10) * mm});
            skLineSegment(sketch, "E543", {"start": v(3.69, 10) * mm, "end": v(3.69, -10) * mm});
            skLineSegment(sketch, "E544", {"start": v(3.69, -10) * mm, "end": v(2.46, -10) * mm});
            skLineSegment(sketch, "E545", {"start": v(4.92, 10) * mm, "end": v(4.92, -10) * mm});
            skLineSegment(sketch, "E546", {"start": v(4.92, -10) * mm, "end": v(3.69, -10) * mm});
            skLineSegment(sketch, "E547", {"start": v(6.15, 10) * mm, "end": v(6.15, -10) * mm});
            skLineSegment(sketch, "E548", {"start": v(6.15, -10) * mm, "end": v(4.92, -10) * mm});
            skLineSegment(sketch, "E549", {"start": v(7.38, 10) * mm, "end": v(7.38, -10) * mm});
            skLineSegment(sketch, "E550", {"start": v(7.38, -10) * mm, "end": v(6.15, -10) * mm});
            skLineSegment(sketch, "E551", {"start": v(8.6, 10) * mm, "end": v(8.6, -10) * mm});
            skLineSegment(sketch, "E552", {"start": v(8.6, -10) * mm, "end": v(7.38, -10) * mm});
            skLineSegment(sketch, "E553", {"start": v(9.84, 10) * mm, "end": v(9.84, -10) * mm});
            skLineSegment(sketch, "E554", {"start": v(9.84, -10) * mm, "end": v(8.6, -10) * mm});
            skLineSegment(sketch, "E555", {"start": v(10, -10) * mm, "end": v(9.84, -10) * mm});
            skLineSegment(sketch, "E556", {"start": v(-10, 9.84) * mm, "end": v(-9.84, 9.84) * mm});
            skLineSegment(sketch, "E557", {"start": v(-9.84, 9.84) * mm, "end": v(-8.61, 9.84) * mm});
            skLineSegment(sketch, "E558", {"start": v(-8.61, 9.84) * mm, "end": v(-7.38, 9.84) * mm});
            skLineSegment(sketch, "E559", {"start": v(-7.38, 9.84) * mm, "end": v(-6.15, 9.84) * mm});
            skLineSegment(sketch, "E560", {"start": v(-6.15, 9.84) * mm, "end": v(-4.92, 9.84) * mm});
            skLineSegment(sketch, "E561", {"start": v(-4.92, 9.84) * mm, "end": v(-3.7, 9.84) * mm});
            skLineSegment(sketch, "E562", {"start": v(-3.7, 9.84) * mm, "end": v(-2.46, 9.84) * mm});
            skLineSegment(sketch, "E563", {"start": v(-2.46, 9.84) * mm, "end": v(-1.23, 9.84) * mm});
            skLineSegment(sketch, "E564", {"start": v(-1.23, 9.84) * mm, "end": v(0, 9.84) * mm});
            skLineSegment(sketch, "E565", {"start": v(0, 9.84) * mm, "end": v(1.23, 9.84) * mm});
            skLineSegment(sketch, "E566", {"start": v(1.23, 9.84) * mm, "end": v(2.46, 9.84) * mm});
            skLineSegment(sketch, "E567", {"start": v(2.46, 9.84) * mm, "end": v(3.69, 9.84) * mm});
            skLineSegment(sketch, "E568", {"start": v(3.69, 9.84) * mm, "end": v(4.92, 9.84) * mm});
            skLineSegment(sketch, "E569", {"start": v(4.92, 9.84) * mm, "end": v(6.15, 9.84) * mm});
            skLineSegment(sketch, "E570", {"start": v(6.15, 9.84) * mm, "end": v(7.38, 9.84) * mm});
            skLineSegment(sketch, "E571", {"start": v(7.38, 9.84) * mm, "end": v(8.6, 9.84) * mm});
            skLineSegment(sketch, "E572", {"start": v(8.6, 9.84) * mm, "end": v(9.84, 9.84) * mm});
            skLineSegment(sketch, "E573", {"start": v(9.84, 9.84) * mm, "end": v(10, 9.84) * mm});
            skLineSegment(sketch, "E574", {"start": v(-10, -9.84) * mm, "end": v(-9.84, -9.84) * mm});
            skLineSegment(sketch, "E575", {"start": v(-9.84, -9.84) * mm, "end": v(-8.61, -9.84) * mm});
            skLineSegment(sketch, "E576", {"start": v(-8.61, -9.84) * mm, "end": v(-7.38, -9.84) * mm});
            skLineSegment(sketch, "E577", {"start": v(-7.38, -9.84) * mm, "end": v(-6.15, -9.84) * mm});
            skLineSegment(sketch, "E578", {"start": v(-6.15, -9.84) * mm, "end": v(-4.92, -9.84) * mm});
            skLineSegment(sketch, "E579", {"start": v(-4.92, -9.84) * mm, "end": v(-3.7, -9.84) * mm});
            skLineSegment(sketch, "E580", {"start": v(-3.7, -9.84) * mm, "end": v(-2.46, -9.84) * mm});
            skLineSegment(sketch, "E581", {"start": v(-2.46, -9.84) * mm, "end": v(-1.23, -9.84) * mm});
            skLineSegment(sketch, "E582", {"start": v(-1.23, -9.84) * mm, "end": v(0, -9.84) * mm});
            skLineSegment(sketch, "E583", {"start": v(0, -9.84) * mm, "end": v(1.23, -9.84) * mm});
            skLineSegment(sketch, "E584", {"start": v(1.23, -9.84) * mm, "end": v(2.46, -9.84) * mm});
            skLineSegment(sketch, "E585", {"start": v(2.46, -9.84) * mm, "end": v(3.69, -9.84) * mm});
            skLineSegment(sketch, "E586", {"start": v(3.69, -9.84) * mm, "end": v(4.92, -9.84) * mm});
            skLineSegment(sketch, "E587", {"start": v(4.92, -9.84) * mm, "end": v(6.15, -9.84) * mm});
            skLineSegment(sketch, "E588", {"start": v(6.15, -9.84) * mm, "end": v(7.38, -9.84) * mm});
            skLineSegment(sketch, "E589", {"start": v(7.38, -9.84) * mm, "end": v(8.6, -9.84) * mm});
            skLineSegment(sketch, "E590", {"start": v(8.6, -9.84) * mm, "end": v(9.84, -9.84) * mm});
            skLineSegment(sketch, "E591", {"start": v(9.84, -9.84) * mm, "end": v(10, -9.84) * mm});
            skLineSegment(sketch, "E592", {"start": v(-10, 10) * mm, "end": v(-10, 9.84) * mm});
            skLineSegment(sketch, "E593", {"start": v(-10, -9.84) * mm, "end": v(-10, -10) * mm});
            skLineSegment(sketch, "E594", {"start": v(10, -9.84) * mm, "end": v(10, -10) * mm});
            skLineSegment(sketch, "E595", {"start": v(10, 9.84) * mm, "end": v(10, 10) * mm});
            skLineSegment(sketch, "E596", {"start": v(-10, 9.84) * mm, "end": v(-10, 9.23) * mm});
            skLineSegment(sketch, "E597", {"start": v(-10, 9.23) * mm, "end": v(-9.84, 9.23) * mm});
            skLineSegment(sketch, "E598", {"start": v(-9.84, 9.23) * mm, "end": v(-8.61, 9.23) * mm});
            skLineSegment(sketch, "E599", {"start": v(-8.61, 9.23) * mm, "end": v(-7.38, 9.23) * mm});
            skLineSegment(sketch, "E600", {"start": v(-7.38, 9.23) * mm, "end": v(-6.15, 9.23) * mm});
            skLineSegment(sketch, "E601", {"start": v(-6.15, 9.23) * mm, "end": v(-4.92, 9.23) * mm});
            skLineSegment(sketch, "E602", {"start": v(-4.92, 9.23) * mm, "end": v(-3.7, 9.23) * mm});
            skLineSegment(sketch, "E603", {"start": v(-3.7, 9.23) * mm, "end": v(-2.46, 9.23) * mm});
            skLineSegment(sketch, "E604", {"start": v(-2.46, 9.23) * mm, "end": v(-1.23, 9.23) * mm});
            skLineSegment(sketch, "E605", {"start": v(-1.23, 9.23) * mm, "end": v(0, 9.23) * mm});
            skLineSegment(sketch, "E606", {"start": v(0, 9.23) * mm, "end": v(1.23, 9.23) * mm});
            skLineSegment(sketch, "E607", {"start": v(1.23, 9.23) * mm, "end": v(2.46, 9.23) * mm});
            skLineSegment(sketch, "E608", {"start": v(2.46, 9.23) * mm, "end": v(3.69, 9.23) * mm});
            skLineSegment(sketch, "E609", {"start": v(3.69, 9.23) * mm, "end": v(4.92, 9.23) * mm});
            skLineSegment(sketch, "E610", {"start": v(4.92, 9.23) * mm, "end": v(6.15, 9.23) * mm});
            skLineSegment(sketch, "E611", {"start": v(6.15, 9.23) * mm, "end": v(7.38, 9.23) * mm});
            skLineSegment(sketch, "E612", {"start": v(7.38, 9.23) * mm, "end": v(8.6, 9.23) * mm});
            skLineSegment(sketch, "E613", {"start": v(8.6, 9.23) * mm, "end": v(9.84, 9.23) * mm});
            skLineSegment(sketch, "E614", {"start": v(9.84, 9.23) * mm, "end": v(10, 9.23) * mm});
            skLineSegment(sketch, "E615", {"start": v(10, 9.23) * mm, "end": v(10, 9.84) * mm});
            skLineSegment(sketch, "E616", {"start": v(-10, -9.84) * mm, "end": v(-10, -9.23) * mm});
            skLineSegment(sketch, "E617", {"start": v(-10, -9.23) * mm, "end": v(-9.84, -9.23) * mm});
            skLineSegment(sketch, "E618", {"start": v(-9.84, -9.23) * mm, "end": v(-8.61, -9.23) * mm});
            skLineSegment(sketch, "E619", {"start": v(-8.61, -9.23) * mm, "end": v(-7.38, -9.23) * mm});
            skLineSegment(sketch, "E620", {"start": v(-7.38, -9.23) * mm, "end": v(-6.15, -9.23) * mm});
            skLineSegment(sketch, "E621", {"start": v(-6.15, -9.23) * mm, "end": v(-4.92, -9.23) * mm});
            skLineSegment(sketch, "E622", {"start": v(-4.92, -9.23) * mm, "end": v(-3.7, -9.23) * mm});
            skLineSegment(sketch, "E623", {"start": v(-3.7, -9.23) * mm, "end": v(-2.46, -9.23) * mm});
            skLineSegment(sketch, "E624", {"start": v(-2.46, -9.23) * mm, "end": v(-1.23, -9.23) * mm});
            skLineSegment(sketch, "E625", {"start": v(-1.23, -9.23) * mm, "end": v(0, -9.23) * mm});
            skLineSegment(sketch, "E626", {"start": v(0, -9.23) * mm, "end": v(1.23, -9.23) * mm});
            skLineSegment(sketch, "E627", {"start": v(1.23, -9.23) * mm, "end": v(2.46, -9.23) * mm});
            skLineSegment(sketch, "E628", {"start": v(2.46, -9.23) * mm, "end": v(3.69, -9.23) * mm});
            skLineSegment(sketch, "E629", {"start": v(3.69, -9.23) * mm, "end": v(4.92, -9.23) * mm});
            skLineSegment(sketch, "E630", {"start": v(4.92, -9.23) * mm, "end": v(6.15, -9.23) * mm});
            skLineSegment(sketch, "E631", {"start": v(6.15, -9.23) * mm, "end": v(7.38, -9.23) * mm});
            skLineSegment(sketch, "E632", {"start": v(7.38, -9.23) * mm, "end": v(8.6, -9.23) * mm});
            skLineSegment(sketch, "E633", {"start": v(8.6, -9.23) * mm, "end": v(9.84, -9.23) * mm});
            skLineSegment(sketch, "E634", {"start": v(9.84, -9.23) * mm, "end": v(10, -9.23) * mm});
            skLineSegment(sketch, "E635", {"start": v(9.84, -10) * mm, "end": v(9.84, 9.23) * mm});
            skLineSegment(sketch, "E636", {"start": v(10, -9.22) * mm, "end": v(10, -9.84) * mm});
            skLineSegment(sketch, "E637", {"start": v(8.6, 9.23) * mm, "end": v(8.6, -9.23) * mm});
            skLineSegment(sketch, "E638", {"start": v(7.38, -9.22) * mm, "end": v(7.38, 9.23) * mm});
            skLineSegment(sketch, "E639", {"start": v(6.15, 9.23) * mm, "end": v(6.15, -9.23) * mm});
            skLineSegment(sketch, "E640", {"start": v(4.92, -9.23) * mm, "end": v(4.92, 9.23) * mm});
            skLineSegment(sketch, "E641", {"start": v(3.69, 9.23) * mm, "end": v(3.69, -9.23) * mm});
            skLineSegment(sketch, "E642", {"start": v(2.46, -9.23) * mm, "end": v(2.46, 9.23) * mm});
            skLineSegment(sketch, "E643", {"start": v(1.23, 9.23) * mm, "end": v(1.23, -9.23) * mm});
            skLineSegment(sketch, "E644", {"start": v(0, -9.23) * mm, "end": v(0, 9.23) * mm});
            skLineSegment(sketch, "E645", {"start": v(-1.23, 9.23) * mm, "end": v(-1.23, -9.23) * mm});
            skLineSegment(sketch, "E646", {"start": v(-2.46, -9.23) * mm, "end": v(-2.46, 9.23) * mm});
            skLineSegment(sketch, "E647", {"start": v(-3.7, 9.23) * mm, "end": v(-3.7, -9.23) * mm});
            skLineSegment(sketch, "E648", {"start": v(-4.92, -9.23) * mm, "end": v(-4.92, 9.23) * mm});
            skLineSegment(sketch, "E649", {"start": v(-6.15, 9.23) * mm, "end": v(-6.15, -9.23) * mm});
            skLineSegment(sketch, "E650", {"start": v(-7.38, -9.23) * mm, "end": v(-7.38, 9.23) * mm});
            skLineSegment(sketch, "E651", {"start": v(-8.61, 9.23) * mm, "end": v(-8.61, -9.23) * mm});
            skArc(sketch, "E652", {"start": v(9.84, 9.23) * mm, "mid": v(9.22, 9.84) * mm, "end": v(8.6, 9.23) * mm});
            skArc(sketch, "E653", {"start": v(7.38, -9.22) * mm, "mid": v(8, -9.84) * mm, "end": v(8.61, -9.23) * mm});
            skArc(sketch, "E654", {"start": v(7.38, 9.23) * mm, "mid": v(6.77, 9.84) * mm, "end": v(6.15, 9.23) * mm});
            skArc(sketch, "E655", {"start": v(4.92, -9.23) * mm, "mid": v(5.53, -9.84) * mm, "end": v(6.15, -9.23) * mm});
            skArc(sketch, "E656", {"start": v(4.92, 9.23) * mm, "mid": v(4.3, 9.84) * mm, "end": v(3.69, 9.23) * mm});
            skArc(sketch, "E657", {"start": v(2.46, 9.23) * mm, "mid": v(1.84, 9.84) * mm, "end": v(1.23, 9.23) * mm});
            skArc(sketch, "E658", {"start": v(2.46, -9.23) * mm, "mid": v(3.07, -9.84) * mm, "end": v(3.69, -9.23) * mm});
            skArc(sketch, "E659", {"start": v(0, 9.23) * mm, "mid": v(-0.62, 9.84) * mm, "end": v(-1.23, 9.23) * mm});
            skArc(sketch, "E660", {"start": v(-2.46, 9.23) * mm, "mid": v(-3.08, 9.84) * mm, "end": v(-3.7, 9.23) * mm});
            skArc(sketch, "E661", {"start": v(-4.92, 9.23) * mm, "mid": v(-5.54, 9.84) * mm, "end": v(-6.15, 9.23) * mm});
            skArc(sketch, "E662", {"start": v(-2.46, -9.23) * mm, "mid": v(-1.85, -9.84) * mm, "end": v(-1.23, -9.23) * mm});
            skArc(sketch, "E663", {"start": v(-4.92, -9.23) * mm, "mid": v(-4.3, -9.84) * mm, "end": v(-3.7, -9.23) * mm});
            skArc(sketch, "E664", {"start": v(-9.84, -9.23) * mm, "mid": v(-9.23, -9.84) * mm, "end": v(-8.61, -9.23) * mm});
            skArc(sketch, "E665", {"start": v(0, -9.23) * mm, "mid": v(0.61, -9.84) * mm, "end": v(1.23, -9.23) * mm});
            skArc(sketch, "E666", {"start": v(-7.38, -9.23) * mm, "mid": v(-6.77, -9.84) * mm, "end": v(-6.15, -9.23) * mm});
            skLineSegment(sketch, "E667", {"start": v(-9.84, -9.23) * mm, "end": v(-9.84, 10) * mm});
            skArc(sketch, "E668", {"start": v(-7.38, 9.23) * mm, "mid": v(-8, 9.84) * mm, "end": v(-8.61, 9.23) * mm});
            skSolve(sketch);
        }
        {
            var Q0;
            Q0=qCreatedBy(id+"F3.planeOp",FACE);
            var sketch = newSketch(context, id + "F12", { "sketchPlane" : qUnion([Q0])});
            skCircle(sketch, "E669", {"center": v(-9.84, 1.03) * mm, "radius": 0.2 * mm});
            skSolve(sketch);
        }
        {
            var Q0;
            Q0=makeQuery(id+"F12.imprint","IMPRINT",FACE,{"disambiguationData":[TD([[makeQuery(id+"F12.imprint","IMPRINT",EDGE,{"derivedFrom":sQuery(id+"F12.wireOp",EDGE,"E669")}),1.0]])]});
            var Q1;
            Q1=sQuery(id+"F11.wireOp",EDGE,"E635");
            var Q2;
            Q2=sQuery(id+"F11.wireOp",EDGE,"E652");
            var Q3;
            Q3=sQuery(id+"F11.wireOp",EDGE,"E637");
            var Q4;
            Q4=sQuery(id+"F11.wireOp",EDGE,"E653");
            var Q5;
            Q5=sQuery(id+"F11.wireOp",EDGE,"E638");
            var Q6;
            Q6=sQuery(id+"F11.wireOp",EDGE,"E654");
            var Q7;
            Q7=sQuery(id+"F11.wireOp",EDGE,"E639");
            var Q8;
            Q8=sQuery(id+"F11.wireOp",EDGE,"E655");
            var Q9;
            Q9=sQuery(id+"F11.wireOp",EDGE,"E640");
            var Q10;
            Q10=sQuery(id+"F11.wireOp",EDGE,"E656");
            var Q11;
            Q11=sQuery(id+"F11.wireOp",EDGE,"E641");
            var Q12;
            Q12=sQuery(id+"F11.wireOp",EDGE,"E658");
            var Q13;
            Q13=sQuery(id+"F11.wireOp",EDGE,"E642");
            var Q14;
            Q14=sQuery(id+"F11.wireOp",EDGE,"E657");
            var Q15;
            Q15=sQuery(id+"F11.wireOp",EDGE,"E643");
            var Q16;
            Q16=sQuery(id+"F11.wireOp",EDGE,"E665");
            var Q17;
            Q17=sQuery(id+"F11.wireOp",EDGE,"E644");
            var Q18;
            Q18=sQuery(id+"F11.wireOp",EDGE,"E659");
            var Q19;
            Q19=sQuery(id+"F11.wireOp",EDGE,"E645");
            var Q20;
            Q20=sQuery(id+"F11.wireOp",EDGE,"E662");
            var Q21;
            Q21=sQuery(id+"F11.wireOp",EDGE,"E646");
            var Q22;
            Q22=sQuery(id+"F11.wireOp",EDGE,"E660");
            var Q23;
            Q23=sQuery(id+"F11.wireOp",EDGE,"E647");
            var Q24;
            Q24=sQuery(id+"F11.wireOp",EDGE,"E663");
            var Q25;
            Q25=sQuery(id+"F11.wireOp",EDGE,"E648");
            var Q26;
            Q26=sQuery(id+"F11.wireOp",EDGE,"E661");
            var Q27;
            Q27=sQuery(id+"F11.wireOp",EDGE,"E649");
            var Q28;
            Q28=sQuery(id+"F11.wireOp",EDGE,"E666");
            var Q29;
            Q29=sQuery(id+"F11.wireOp",EDGE,"E650");
            var Q30;
            Q30=sQuery(id+"F11.wireOp",EDGE,"E668");
            var Q31;
            Q31=sQuery(id+"F11.wireOp",EDGE,"E651");
            var Q32;
            Q32=sQuery(id+"F11.wireOp",EDGE,"E664");
            var Q33;
            Q33=sQuery(id+"F11.wireOp",EDGE,"E667");
            sweep(context, id + "F13", {"operationType" : NewBodyOperationType.ADD, "profiles" : qUnion([Q0]), "path" : qUnion([Q1, Q2, Q3, Q4, Q5, Q6, Q7, Q8, Q9, Q10, Q11, Q12, Q13, Q14, Q15, Q16, Q17, Q18, Q19, Q20, Q21, Q22, Q23, Q24, Q25, Q26, Q27, Q28, Q29, Q30, Q31, Q32, Q33])});
        }
        {
            var Q0;
            Q0=qCreatedBy(id+"F10.planeOp",FACE);
            cPlane(context, id + "F14", {"entities" : qUnion([Q0]), "cplaneType" : CPlaneType.OFFSET, "offset" : getVariable(context, 'd'), "width" : 150 * mm, "height" : 150 * mm});
        }
        {
            var Q0;
            Q0=qCreatedBy(id+"F14.planeOp",FACE);
            var sketch = newSketch(context, id + "F15", { "sketchPlane" : qUnion([Q0])});
            skLineSegment(sketch, "E670.bottom", {"start": v(10, 10) * mm, "end": v(10, 30) * mm});
            skLineSegment(sketch, "E670.top", {"start": v(-10, 10) * mm, "end": v(-10, 30) * mm});
            skLineSegment(sketch, "E670.left", {"start": v(10, 10) * mm, "end": v(-10, 10) * mm});
            skLineSegment(sketch, "E670.right", {"start": v(10, 30) * mm, "end": v(-10, 30) * mm});
            skPoint(sketch, "E670.middle", {"position": v(0, 20) * mm});
            skLineSegment(sketch, "E671", {"start": v(10, 30) * mm, "end": v(10, 29.84) * mm});
            skLineSegment(sketch, "E672", {"start": v(10, 29.84) * mm, "end": v(10, 28.6) * mm});
            skLineSegment(sketch, "E673", {"start": v(10, 28.6) * mm, "end": v(10, 27.38) * mm});
            skLineSegment(sketch, "E674", {"start": v(10, 27.38) * mm, "end": v(10, 26.15) * mm});
            skLineSegment(sketch, "E675", {"start": v(10, 26.15) * mm, "end": v(10, 24.92) * mm});
            skLineSegment(sketch, "E676", {"start": v(10, 24.92) * mm, "end": v(10, 23.69) * mm});
            skLineSegment(sketch, "E677", {"start": v(10, 23.69) * mm, "end": v(10, 22.46) * mm});
            skLineSegment(sketch, "E678", {"start": v(10, 22.46) * mm, "end": v(10, 21.23) * mm});
            skLineSegment(sketch, "E679", {"start": v(10, 21.23) * mm, "end": v(10, 20) * mm});
            skLineSegment(sketch, "E680", {"start": v(10, 20) * mm, "end": v(10, 18.77) * mm});
            skLineSegment(sketch, "E681", {"start": v(10, 18.77) * mm, "end": v(10, 17.54) * mm});
            skLineSegment(sketch, "E682", {"start": v(10, 17.54) * mm, "end": v(10, 16.31) * mm});
            skLineSegment(sketch, "E683", {"start": v(10, 16.31) * mm, "end": v(10, 15.08) * mm});
            skLineSegment(sketch, "E684", {"start": v(10, 15.08) * mm, "end": v(10, 13.85) * mm});
            skLineSegment(sketch, "E685", {"start": v(10, 13.85) * mm, "end": v(10, 12.62) * mm});
            skLineSegment(sketch, "E686", {"start": v(10, 12.62) * mm, "end": v(10, 11.4) * mm});
            skLineSegment(sketch, "E687", {"start": v(10, 11.4) * mm, "end": v(10, 10.16) * mm});
            skLineSegment(sketch, "E688", {"start": v(10, 10.16) * mm, "end": v(10, 10) * mm});
            skLineSegment(sketch, "E689", {"start": v(10, 29.84) * mm, "end": v(-10, 29.84) * mm});
            skLineSegment(sketch, "E690", {"start": v(-10, 29.84) * mm, "end": v(-10, 30) * mm});
            skLineSegment(sketch, "E691", {"start": v(10, 28.6) * mm, "end": v(-10, 28.6) * mm});
            skLineSegment(sketch, "E692", {"start": v(-10, 28.61) * mm, "end": v(-10, 29.84) * mm});
            skLineSegment(sketch, "E693", {"start": v(10, 27.38) * mm, "end": v(-10, 27.38) * mm});
            skLineSegment(sketch, "E694", {"start": v(-10, 27.38) * mm, "end": v(-10, 28.61) * mm});
            skLineSegment(sketch, "E695", {"start": v(10, 26.15) * mm, "end": v(-10, 26.15) * mm});
            skLineSegment(sketch, "E696", {"start": v(-10, 26.15) * mm, "end": v(-10, 27.38) * mm});
            skLineSegment(sketch, "E697", {"start": v(10, 24.92) * mm, "end": v(-10, 24.92) * mm});
            skLineSegment(sketch, "E698", {"start": v(-10, 24.92) * mm, "end": v(-10, 26.15) * mm});
            skLineSegment(sketch, "E699", {"start": v(10, 23.69) * mm, "end": v(-10, 23.69) * mm});
            skLineSegment(sketch, "E700", {"start": v(-10, 23.69) * mm, "end": v(-10, 24.92) * mm});
            skLineSegment(sketch, "E701", {"start": v(10, 22.46) * mm, "end": v(-10, 22.46) * mm});
            skLineSegment(sketch, "E702", {"start": v(-10, 22.46) * mm, "end": v(-10, 23.69) * mm});
            skLineSegment(sketch, "E703", {"start": v(10, 21.23) * mm, "end": v(-10, 21.23) * mm});
            skLineSegment(sketch, "E704", {"start": v(-10, 21.23) * mm, "end": v(-10, 22.46) * mm});
            skLineSegment(sketch, "E705", {"start": v(10, 20) * mm, "end": v(-10, 20) * mm});
            skLineSegment(sketch, "E706", {"start": v(-10, 20) * mm, "end": v(-10, 21.23) * mm});
            skLineSegment(sketch, "E707", {"start": v(10, 18.77) * mm, "end": v(-10, 18.77) * mm});
            skLineSegment(sketch, "E708", {"start": v(-10, 18.77) * mm, "end": v(-10, 20) * mm});
            skLineSegment(sketch, "E709", {"start": v(10, 17.54) * mm, "end": v(-10, 17.54) * mm});
            skLineSegment(sketch, "E710", {"start": v(-10, 17.54) * mm, "end": v(-10, 18.77) * mm});
            skLineSegment(sketch, "E711", {"start": v(10, 16.31) * mm, "end": v(-10, 16.31) * mm});
            skLineSegment(sketch, "E712", {"start": v(-10, 16.31) * mm, "end": v(-10, 17.54) * mm});
            skLineSegment(sketch, "E713", {"start": v(10, 15.08) * mm, "end": v(-10, 15.08) * mm});
            skLineSegment(sketch, "E714", {"start": v(-10, 15.08) * mm, "end": v(-10, 16.31) * mm});
            skLineSegment(sketch, "E715", {"start": v(10, 13.85) * mm, "end": v(-10, 13.85) * mm});
            skLineSegment(sketch, "E716", {"start": v(-10, 13.85) * mm, "end": v(-10, 15.08) * mm});
            skLineSegment(sketch, "E717", {"start": v(10, 12.62) * mm, "end": v(-10, 12.62) * mm});
            skLineSegment(sketch, "E718", {"start": v(-10, 12.62) * mm, "end": v(-10, 13.85) * mm});
            skLineSegment(sketch, "E719", {"start": v(10, 11.4) * mm, "end": v(-10, 11.39) * mm});
            skLineSegment(sketch, "E720", {"start": v(-10, 11.39) * mm, "end": v(-10, 12.62) * mm});
            skLineSegment(sketch, "E721", {"start": v(10, 10.16) * mm, "end": v(-10, 10.16) * mm});
            skLineSegment(sketch, "E722", {"start": v(-10, 10.16) * mm, "end": v(-10, 11.39) * mm});
            skLineSegment(sketch, "E723", {"start": v(-10, 10) * mm, "end": v(-10, 10.16) * mm});
            skLineSegment(sketch, "E724", {"start": v(9.84, 30) * mm, "end": v(9.84, 29.84) * mm});
            skLineSegment(sketch, "E725", {"start": v(9.84, 29.84) * mm, "end": v(9.84, 28.6) * mm});
            skLineSegment(sketch, "E726", {"start": v(9.84, 28.6) * mm, "end": v(9.84, 27.38) * mm});
            skLineSegment(sketch, "E727", {"start": v(9.84, 27.38) * mm, "end": v(9.84, 26.15) * mm});
            skLineSegment(sketch, "E728", {"start": v(9.84, 26.15) * mm, "end": v(9.84, 24.92) * mm});
            skLineSegment(sketch, "E729", {"start": v(9.84, 24.92) * mm, "end": v(9.84, 23.69) * mm});
            skLineSegment(sketch, "E730", {"start": v(9.84, 23.69) * mm, "end": v(9.84, 22.46) * mm});
            skLineSegment(sketch, "E731", {"start": v(9.84, 22.46) * mm, "end": v(9.84, 21.23) * mm});
            skLineSegment(sketch, "E732", {"start": v(9.84, 21.23) * mm, "end": v(9.84, 10.5) * mm});
            skLineSegment(sketch, "E733", {"start": v(9.84, 18.77) * mm, "end": v(9.84, 10.5) * mm});
            skLineSegment(sketch, "E734", {"start": v(9.84, 18.77) * mm, "end": v(9.84, 17.54) * mm});
            skLineSegment(sketch, "E735", {"start": v(9.84, 17.54) * mm, "end": v(9.84, 16.31) * mm});
            skLineSegment(sketch, "E736", {"start": v(9.84, 16.31) * mm, "end": v(9.84, 15.08) * mm});
            skLineSegment(sketch, "E737", {"start": v(9.84, 15.08) * mm, "end": v(9.84, 13.85) * mm});
            skLineSegment(sketch, "E738", {"start": v(9.84, 13.85) * mm, "end": v(9.84, 12.62) * mm});
            skLineSegment(sketch, "E739", {"start": v(9.84, 12.62) * mm, "end": v(9.84, 11.4) * mm});
            skLineSegment(sketch, "E740", {"start": v(9.84, 11.4) * mm, "end": v(9.84, 10.16) * mm});
            skLineSegment(sketch, "E741", {"start": v(9.84, 10.16) * mm, "end": v(9.84, 10) * mm});
            skLineSegment(sketch, "E742", {"start": v(-9.84, 30) * mm, "end": v(-9.84, 29.84) * mm});
            skLineSegment(sketch, "E743", {"start": v(-9.84, 29.84) * mm, "end": v(-9.84, 28.61) * mm});
            skLineSegment(sketch, "E744", {"start": v(-9.84, 28.61) * mm, "end": v(-9.84, 27.38) * mm});
            skLineSegment(sketch, "E745", {"start": v(-9.84, 27.38) * mm, "end": v(-9.84, 26.15) * mm});
            skLineSegment(sketch, "E746", {"start": v(-9.84, 26.15) * mm, "end": v(-9.84, 24.92) * mm});
            skLineSegment(sketch, "E747", {"start": v(-9.84, 24.92) * mm, "end": v(-9.84, 23.69) * mm});
            skLineSegment(sketch, "E748", {"start": v(-9.84, 23.69) * mm, "end": v(-9.84, 22.46) * mm});
            skLineSegment(sketch, "E749", {"start": v(-9.84, 22.46) * mm, "end": v(-9.84, 21.23) * mm});
            skLineSegment(sketch, "E750", {"start": v(-9.84, 29.5) * mm, "end": v(-9.84, 21.23) * mm});
            skLineSegment(sketch, "E751", {"start": v(-9.84, 29.5) * mm, "end": v(-9.84, 18.77) * mm});
            skLineSegment(sketch, "E752", {"start": v(-9.84, 18.77) * mm, "end": v(-9.84, 17.54) * mm});
            skLineSegment(sketch, "E753", {"start": v(-9.84, 17.54) * mm, "end": v(-9.84, 16.31) * mm});
            skLineSegment(sketch, "E754", {"start": v(-9.84, 16.31) * mm, "end": v(-9.84, 15.08) * mm});
            skLineSegment(sketch, "E755", {"start": v(-9.84, 15.08) * mm, "end": v(-9.84, 13.85) * mm});
            skLineSegment(sketch, "E756", {"start": v(-9.84, 13.85) * mm, "end": v(-9.84, 12.62) * mm});
            skLineSegment(sketch, "E757", {"start": v(-9.84, 12.62) * mm, "end": v(-9.84, 11.39) * mm});
            skLineSegment(sketch, "E758", {"start": v(-9.84, 11.39) * mm, "end": v(-9.84, 10.16) * mm});
            skLineSegment(sketch, "E759", {"start": v(-9.84, 10.16) * mm, "end": v(-9.84, 10) * mm});
            skLineSegment(sketch, "E760", {"start": v(10, 30) * mm, "end": v(9.84, 30) * mm});
            skLineSegment(sketch, "E761", {"start": v(-9.84, 30) * mm, "end": v(-10, 30) * mm});
            skLineSegment(sketch, "E762", {"start": v(-9.84, 10) * mm, "end": v(-10, 10) * mm});
            skLineSegment(sketch, "E763", {"start": v(9.84, 10) * mm, "end": v(10, 10) * mm});
            skLineSegment(sketch, "E764", {"start": v(9.84, 30) * mm, "end": v(9.22, 30) * mm});
            skLineSegment(sketch, "E765", {"start": v(9.22, 30) * mm, "end": v(9.22, 29.84) * mm});
            skLineSegment(sketch, "E766", {"start": v(9.22, 29.84) * mm, "end": v(9.22, 28.61) * mm});
            skLineSegment(sketch, "E767", {"start": v(9.22, 28.61) * mm, "end": v(9.22, 27.38) * mm});
            skLineSegment(sketch, "E768", {"start": v(9.22, 27.38) * mm, "end": v(9.22, 26.15) * mm});
            skLineSegment(sketch, "E769", {"start": v(9.22, 26.15) * mm, "end": v(9.22, 24.92) * mm});
            skLineSegment(sketch, "E770", {"start": v(9.22, 24.92) * mm, "end": v(9.22, 23.69) * mm});
            skLineSegment(sketch, "E771", {"start": v(9.22, 23.69) * mm, "end": v(9.22, 22.46) * mm});
            skLineSegment(sketch, "E772", {"start": v(9.22, 22.46) * mm, "end": v(9.22, 21.23) * mm});
            skLineSegment(sketch, "E773", {"start": v(9.22, 21.23) * mm, "end": v(9.22, 20) * mm});
            skLineSegment(sketch, "E774", {"start": v(9.22, 20) * mm, "end": v(9.22, 18.77) * mm});
            skLineSegment(sketch, "E775", {"start": v(9.22, 18.77) * mm, "end": v(9.22, 17.54) * mm});
            skLineSegment(sketch, "E776", {"start": v(9.22, 17.54) * mm, "end": v(9.22, 16.31) * mm});
            skLineSegment(sketch, "E777", {"start": v(9.22, 16.31) * mm, "end": v(9.22, 15.08) * mm});
            skLineSegment(sketch, "E778", {"start": v(9.22, 15.08) * mm, "end": v(9.22, 13.85) * mm});
            skLineSegment(sketch, "E779", {"start": v(9.22, 13.85) * mm, "end": v(9.22, 12.62) * mm});
            skLineSegment(sketch, "E780", {"start": v(9.22, 12.62) * mm, "end": v(9.22, 11.4) * mm});
            skLineSegment(sketch, "E781", {"start": v(9.22, 11.4) * mm, "end": v(9.22, 10.16) * mm});
            skLineSegment(sketch, "E782", {"start": v(9.22, 10.16) * mm, "end": v(9.22, 10) * mm});
            skLineSegment(sketch, "E783", {"start": v(9.22, 10) * mm, "end": v(9.84, 10) * mm});
            skLineSegment(sketch, "E784", {"start": v(-9.84, 30) * mm, "end": v(-9.23, 30) * mm});
            skLineSegment(sketch, "E785", {"start": v(-9.23, 30) * mm, "end": v(-9.23, 29.84) * mm});
            skLineSegment(sketch, "E786", {"start": v(-9.23, 29.84) * mm, "end": v(-9.23, 28.61) * mm});
            skLineSegment(sketch, "E787", {"start": v(-9.23, 28.61) * mm, "end": v(-9.23, 27.38) * mm});
            skLineSegment(sketch, "E788", {"start": v(-9.23, 27.38) * mm, "end": v(-9.23, 26.15) * mm});
            skLineSegment(sketch, "E789", {"start": v(-9.23, 26.15) * mm, "end": v(-9.23, 24.92) * mm});
            skLineSegment(sketch, "E790", {"start": v(-9.23, 24.92) * mm, "end": v(-9.23, 23.69) * mm});
            skLineSegment(sketch, "E791", {"start": v(-9.23, 23.69) * mm, "end": v(-9.23, 22.46) * mm});
            skLineSegment(sketch, "E792", {"start": v(-9.23, 22.46) * mm, "end": v(-9.23, 21.23) * mm});
            skLineSegment(sketch, "E793", {"start": v(-9.23, 21.23) * mm, "end": v(-9.23, 20) * mm});
            skLineSegment(sketch, "E794", {"start": v(-9.23, 20) * mm, "end": v(-9.23, 18.77) * mm});
            skLineSegment(sketch, "E795", {"start": v(-9.23, 18.77) * mm, "end": v(-9.23, 17.54) * mm});
            skLineSegment(sketch, "E796", {"start": v(-9.23, 17.54) * mm, "end": v(-9.23, 16.31) * mm});
            skLineSegment(sketch, "E797", {"start": v(-9.23, 16.31) * mm, "end": v(-9.23, 15.08) * mm});
            skLineSegment(sketch, "E798", {"start": v(-9.23, 15.08) * mm, "end": v(-9.23, 13.85) * mm});
            skLineSegment(sketch, "E799", {"start": v(-9.23, 13.85) * mm, "end": v(-9.23, 12.62) * mm});
            skLineSegment(sketch, "E800", {"start": v(-9.23, 12.62) * mm, "end": v(-9.23, 11.39) * mm});
            skLineSegment(sketch, "E801", {"start": v(-9.23, 11.39) * mm, "end": v(-9.23, 10.16) * mm});
            skLineSegment(sketch, "E802", {"start": v(-9.23, 10.16) * mm, "end": v(-9.23, 10) * mm});
            skLineSegment(sketch, "E803", {"start": v(-10, 10.16) * mm, "end": v(9.22, 10.16) * mm});
            skLineSegment(sketch, "E804", {"start": v(-9.23, 10) * mm, "end": v(-9.84, 10) * mm});
            skLineSegment(sketch, "E805", {"start": v(9.22, 11.4) * mm, "end": v(-9.23, 11.4) * mm});
            skLineSegment(sketch, "E806", {"start": v(-9.23, 12.62) * mm, "end": v(9.22, 12.62) * mm});
            skLineSegment(sketch, "E807", {"start": v(9.22, 13.85) * mm, "end": v(-9.23, 13.85) * mm});
            skLineSegment(sketch, "E808", {"start": v(-9.23, 15.08) * mm, "end": v(9.22, 15.08) * mm});
            skLineSegment(sketch, "E809", {"start": v(9.22, 16.31) * mm, "end": v(-9.23, 16.31) * mm});
            skLineSegment(sketch, "E810", {"start": v(-9.23, 17.54) * mm, "end": v(9.22, 17.54) * mm});
            skLineSegment(sketch, "E811", {"start": v(9.22, 18.77) * mm, "end": v(-9.23, 18.77) * mm});
            skLineSegment(sketch, "E812", {"start": v(-9.23, 20) * mm, "end": v(9.22, 20) * mm});
            skLineSegment(sketch, "E813", {"start": v(9.22, 21.23) * mm, "end": v(-9.23, 21.23) * mm});
            skLineSegment(sketch, "E814", {"start": v(-9.23, 22.46) * mm, "end": v(9.22, 22.46) * mm});
            skLineSegment(sketch, "E815", {"start": v(9.22, 23.69) * mm, "end": v(-9.23, 23.69) * mm});
            skLineSegment(sketch, "E816", {"start": v(-9.23, 24.92) * mm, "end": v(9.22, 24.92) * mm});
            skLineSegment(sketch, "E817", {"start": v(9.22, 26.15) * mm, "end": v(-9.23, 26.15) * mm});
            skLineSegment(sketch, "E818", {"start": v(-9.23, 27.38) * mm, "end": v(9.22, 27.38) * mm});
            skLineSegment(sketch, "E819", {"start": v(9.22, 28.6) * mm, "end": v(-9.23, 28.6) * mm});
            skArc(sketch, "E820", {"start": v(9.22, 10.16) * mm, "mid": v(9.84, 10.78) * mm, "end": v(9.22, 11.4) * mm});
            skArc(sketch, "E821", {"start": v(-9.23, 12.62) * mm, "mid": v(-9.84, 12) * mm, "end": v(-9.23, 11.4) * mm});
            skArc(sketch, "E822", {"start": v(9.22, 12.62) * mm, "mid": v(9.84, 13.24) * mm, "end": v(9.22, 13.85) * mm});
            skArc(sketch, "E823", {"start": v(-9.23, 15.08) * mm, "mid": v(-9.84, 14.47) * mm, "end": v(-9.23, 13.85) * mm});
            skArc(sketch, "E824", {"start": v(9.22, 15.08) * mm, "mid": v(9.84, 15.7) * mm, "end": v(9.22, 16.31) * mm});
            skArc(sketch, "E825", {"start": v(9.22, 17.54) * mm, "mid": v(9.84, 18.16) * mm, "end": v(9.22, 18.77) * mm});
            skArc(sketch, "E826", {"start": v(-9.23, 17.54) * mm, "mid": v(-9.84, 16.93) * mm, "end": v(-9.23, 16.31) * mm});
            skArc(sketch, "E827", {"start": v(9.22, 20) * mm, "mid": v(9.84, 20.61) * mm, "end": v(9.22, 21.23) * mm});
            skArc(sketch, "E828", {"start": v(9.22, 22.46) * mm, "mid": v(9.84, 23.07) * mm, "end": v(9.22, 23.69) * mm});
            skArc(sketch, "E829", {"start": v(9.22, 24.92) * mm, "mid": v(9.84, 25.54) * mm, "end": v(9.22, 26.15) * mm});
            skArc(sketch, "E830", {"start": v(-9.23, 22.46) * mm, "mid": v(-9.84, 21.84) * mm, "end": v(-9.23, 21.23) * mm});
            skArc(sketch, "E831", {"start": v(-9.23, 24.92) * mm, "mid": v(-9.84, 24.3) * mm, "end": v(-9.23, 23.69) * mm});
            skArc(sketch, "E832", {"start": v(-9.23, 29.84) * mm, "mid": v(-9.84, 29.23) * mm, "end": v(-9.23, 28.6) * mm});
            skArc(sketch, "E833", {"start": v(-9.23, 20) * mm, "mid": v(-9.84, 19.39) * mm, "end": v(-9.23, 18.77) * mm});
            skArc(sketch, "E834", {"start": v(-9.23, 27.38) * mm, "mid": v(-9.84, 26.76) * mm, "end": v(-9.23, 26.15) * mm});
            skLineSegment(sketch, "E835", {"start": v(-9.23, 29.84) * mm, "end": v(10, 29.84) * mm});
            skArc(sketch, "E836", {"start": v(9.22, 27.38) * mm, "mid": v(9.84, 28) * mm, "end": v(9.22, 28.6) * mm});
            skLineSegment(sketch, "E837.MirrorCS", {"start": v(10, 9.84) * mm, "end": v(10, 10) * mm});
            skLineSegment(sketch, "E838.MirrorCS", {"start": v(-10, 10) * mm, "end": v(-10, 9.84) * mm});
            skLineSegment(sketch, "E839.MirrorCS", {"start": v(9.84, 9.84) * mm, "end": v(9.84, 10) * mm});
            skLineSegment(sketch, "E840.MirrorCS", {"start": v(-9.84, 9.84) * mm, "end": v(-9.84, 10) * mm});
            skLineSegment(sketch, "E841.MirrorCS", {"start": v(-9.84, -10) * mm, "end": v(-9.23, -10) * mm});
            skLineSegment(sketch, "E842.MirrorCS", {"start": v(-10, -9.84) * mm, "end": v(-10, -10) * mm});
            skLineSegment(sketch, "E843.MirrorCS", {"start": v(9.84, -10) * mm, "end": v(9.84, -9.84) * mm});
            skLineSegment(sketch, "E844.MirrorCS", {"start": v(-9.84, -10) * mm, "end": v(-9.84, -9.84) * mm});
            skLineSegment(sketch, "E845.MirrorCS", {"start": v(10, -10) * mm, "end": v(9.84, -10) * mm});
            skLineSegment(sketch, "E846.MirrorCS", {"start": v(-9.84, -10) * mm, "end": v(-10, -10) * mm});
            skLineSegment(sketch, "E847.MirrorCS", {"start": v(10, -10) * mm, "end": v(10, -9.84) * mm});
            skLineSegment(sketch, "E848.MirrorCS", {"start": v(-9.23, -10) * mm, "end": v(-9.23, -9.84) * mm});
            skLineSegment(sketch, "E849.MirrorCS", {"start": v(9.22, 9.84) * mm, "end": v(9.22, 10) * mm});
            skLineSegment(sketch, "E850.MirrorCS", {"start": v(9.84, -10) * mm, "end": v(9.22, -10) * mm});
            skLineSegment(sketch, "E851.MirrorCS", {"start": v(-9.23, 9.84) * mm, "end": v(-9.23, 10) * mm});
            skLineSegment(sketch, "E852.MirrorCS", {"start": v(9.22, -10) * mm, "end": v(9.22, -9.84) * mm});
            skLineSegment(sketch, "E853.MirrorCS", {"start": v(9.84, 3.7) * mm, "end": v(9.84, 4.92) * mm});
            skLineSegment(sketch, "E854.MirrorCS", {"start": v(-10, 8.61) * mm, "end": v(-10, 7.38) * mm});
            skLineSegment(sketch, "E855.MirrorCS", {"start": v(-10, -1.23) * mm, "end": v(-10, -2.46) * mm});
            skLineSegment(sketch, "E856.MirrorCS", {"start": v(-9.23, -4.92) * mm, "end": v(9.22, -4.92) * mm});
            skLineSegment(sketch, "E857.MirrorCS", {"start": v(-9.23, 7.38) * mm, "end": v(-9.23, 8.61) * mm});
            skLineSegment(sketch, "E858.MirrorCS", {"start": v(10, -9.84) * mm, "end": v(-10, -9.84) * mm});
            skLineSegment(sketch, "E859.MirrorCS", {"start": v(-9.84, 2.46) * mm, "end": v(-9.84, 3.69) * mm});
            skLineSegment(sketch, "E860.MirrorCS", {"start": v(10, 9.84) * mm, "end": v(-10, 9.84) * mm});
            skLineSegment(sketch, "E861.MirrorCS", {"start": v(10, 0) * mm, "end": v(-10, 0) * mm});
            skLineSegment(sketch, "E862.MirrorCS", {"start": v(9.22, -6.15) * mm, "end": v(-9.23, -6.15) * mm});
            skLineSegment(sketch, "E863.MirrorCS", {"start": v(9.22, -6.15) * mm, "end": v(9.22, -4.92) * mm});
            skLineSegment(sketch, "E864.MirrorCS", {"start": v(-10, 9.84) * mm, "end": v(-10, 8.61) * mm});
            skLineSegment(sketch, "E865.MirrorCS", {"start": v(-10, 0) * mm, "end": v(-10, -1.23) * mm});
            skLineSegment(sketch, "E866.MirrorCS", {"start": v(-9.23, -9.84) * mm, "end": v(-9.23, -8.6) * mm});
            skLineSegment(sketch, "E867.MirrorCS", {"start": v(9.84, 6.15) * mm, "end": v(9.84, 7.38) * mm});
            skLineSegment(sketch, "E868.MirrorCS", {"start": v(-9.23, -7.38) * mm, "end": v(9.22, -7.38) * mm});
            skLineSegment(sketch, "E869.MirrorCS", {"start": v(10, 1.23) * mm, "end": v(-10, 1.23) * mm});
            skLineSegment(sketch, "E870.MirrorCS", {"start": v(10, -8.6) * mm, "end": v(-10, -8.6) * mm});
            skLineSegment(sketch, "E871.MirrorCS", {"start": v(9.22, -3.69) * mm, "end": v(9.22, -2.46) * mm});
            skLineSegment(sketch, "E872.MirrorCS", {"start": v(-9.84, 4.92) * mm, "end": v(-9.84, 6.15) * mm});
            skLineSegment(sketch, "E873.MirrorCS", {"start": v(-10, 1.23) * mm, "end": v(-10, 0) * mm});
            skLineSegment(sketch, "E874.MirrorCS", {"start": v(-10, -8.6) * mm, "end": v(-10, -9.84) * mm});
            skLineSegment(sketch, "E875.MirrorCS", {"start": v(-9.23, -7.38) * mm, "end": v(-9.23, -6.15) * mm});
            skLineSegment(sketch, "E876.MirrorCS", {"start": v(9.84, 8.61) * mm, "end": v(9.84, 9.84) * mm});
            skLineSegment(sketch, "E877.MirrorCS", {"start": v(10, 2.46) * mm, "end": v(-10, 2.46) * mm});
            skLineSegment(sketch, "E878.MirrorCS", {"start": v(9.22, -1.23) * mm, "end": v(9.22, 0) * mm});
            skLineSegment(sketch, "E879.MirrorCS", {"start": v(-9.84, 7.38) * mm, "end": v(-9.84, 8.61) * mm});
            skLineSegment(sketch, "E880.MirrorCS", {"start": v(9.22, 8.61) * mm, "end": v(-9.23, 8.61) * mm});
            skLineSegment(sketch, "E881.MirrorCS", {"start": v(9.84, -8.6) * mm, "end": v(9.84, -7.38) * mm});
            skLineSegment(sketch, "E882.MirrorCS", {"start": v(-10, 2.46) * mm, "end": v(-10, 1.23) * mm});
            skLineSegment(sketch, "E883.MirrorCS", {"start": v(-10, -7.38) * mm, "end": v(-10, -8.6) * mm});
            skLineSegment(sketch, "E884.MirrorCS", {"start": v(-9.23, -4.92) * mm, "end": v(-9.23, -3.69) * mm});
            skLineSegment(sketch, "E885.MirrorCS", {"start": v(-9.23, 7.38) * mm, "end": v(9.22, 7.38) * mm});
            skLineSegment(sketch, "E886.MirrorCS", {"start": v(9.84, -6.15) * mm, "end": v(9.84, -4.92) * mm});
            skLineSegment(sketch, "E887.MirrorCS", {"start": v(-10, 3.69) * mm, "end": v(-10, 2.46) * mm});
            skLineSegment(sketch, "E888.MirrorCS", {"start": v(-10, -6.15) * mm, "end": v(-10, -7.38) * mm});
            skLineSegment(sketch, "E889.MirrorCS", {"start": v(-9.23, 4.92) * mm, "end": v(9.22, 4.92) * mm});
            skLineSegment(sketch, "E890.MirrorCS", {"start": v(-9.23, -2.46) * mm, "end": v(-9.23, -1.23) * mm});
            skLineSegment(sketch, "E891.MirrorCS", {"start": v(10, 3.69) * mm, "end": v(-10, 3.69) * mm});
            skLineSegment(sketch, "E892.MirrorCS", {"start": v(9.22, 1.23) * mm, "end": v(9.22, 2.46) * mm});
            skLineSegment(sketch, "E893.MirrorCS", {"start": v(-9.84, -9.84) * mm, "end": v(-9.84, -8.6) * mm});
            skLineSegment(sketch, "E894.MirrorCS", {"start": v(9.22, 6.15) * mm, "end": v(-9.23, 6.15) * mm});
            skLineSegment(sketch, "E895.MirrorCS", {"start": v(-9.84, -7.38) * mm, "end": v(-9.84, -6.15) * mm});
            skLineSegment(sketch, "E896.MirrorCS", {"start": v(9.22, 3.7) * mm, "end": v(9.22, 4.92) * mm});
            skLineSegment(sketch, "E897.MirrorCS", {"start": v(9.84, -3.69) * mm, "end": v(9.84, -2.46) * mm});
            skLineSegment(sketch, "E898.MirrorCS", {"start": v(-10, 4.92) * mm, "end": v(-10, 3.69) * mm});
            skLineSegment(sketch, "E899.MirrorCS", {"start": v(-10, -4.92) * mm, "end": v(-10, -6.15) * mm});
            skLineSegment(sketch, "E900.MirrorCS", {"start": v(-9.23, 0) * mm, "end": v(-9.23, 1.23) * mm});
            skLineSegment(sketch, "E901.MirrorCS", {"start": v(-9.84, -4.92) * mm, "end": v(-9.84, -3.69) * mm});
            skLineSegment(sketch, "E902.MirrorCS", {"start": v(10, -3.69) * mm, "end": v(-10, -3.69) * mm});
            skLineSegment(sketch, "E903.MirrorCS", {"start": v(9.22, 6.15) * mm, "end": v(9.22, 7.38) * mm});
            skLineSegment(sketch, "E904.MirrorCS", {"start": v(10, 3.7) * mm, "end": v(10, 4.92) * mm});
            skLineSegment(sketch, "E905.MirrorCS", {"start": v(-9.23, 2.46) * mm, "end": v(-9.23, 3.7) * mm});
            skLineSegment(sketch, "E906.MirrorCS", {"start": v(9.84, -1.23) * mm, "end": v(9.84, 9.5) * mm});
            skLineSegment(sketch, "E907.MirrorCS", {"start": v(9.22, 8.61) * mm, "end": v(9.22, 9.84) * mm});
            skLineSegment(sketch, "E908.MirrorCS", {"start": v(-9.84, -2.46) * mm, "end": v(-9.84, -1.23) * mm});
            skLineSegment(sketch, "E909.MirrorCS", {"start": v(10, 6.15) * mm, "end": v(10, 7.38) * mm});
            skLineSegment(sketch, "E910.MirrorCS", {"start": v(10, 0) * mm, "end": v(10, 1.23) * mm});
            skLineSegment(sketch, "E911.MirrorCS", {"start": v(-10, 6.15) * mm, "end": v(-10, 4.92) * mm});
            skLineSegment(sketch, "E912.MirrorCS", {"start": v(10, 1.23) * mm, "end": v(10, 2.46) * mm});
            skLineSegment(sketch, "E913.MirrorCS", {"start": v(10, -2.46) * mm, "end": v(-10, -2.46) * mm});
            skLineSegment(sketch, "E914.MirrorCS", {"start": v(10, 4.92) * mm, "end": v(10, 6.15) * mm});
            skLineSegment(sketch, "E915.MirrorCS", {"start": v(-10, -3.69) * mm, "end": v(-10, -4.92) * mm});
            skLineSegment(sketch, "E916.MirrorCS", {"start": v(9.22, -1.23) * mm, "end": v(-9.23, -1.23) * mm});
            skLineSegment(sketch, "E917.MirrorCS", {"start": v(-9.84, -9.5) * mm, "end": v(-9.84, 1.23) * mm});
            skLineSegment(sketch, "E918.MirrorCS", {"start": v(10, 2.46) * mm, "end": v(10, 3.7) * mm});
            skLineSegment(sketch, "E919.MirrorCS", {"start": v(-9.23, 4.92) * mm, "end": v(-9.23, 6.15) * mm});
            skLineSegment(sketch, "E920.MirrorCS", {"start": v(9.22, -8.6) * mm, "end": v(9.22, -7.38) * mm});
            skLineSegment(sketch, "E921.MirrorCS", {"start": v(-9.84, 1.23) * mm, "end": v(-9.84, 2.46) * mm});
            skLineSegment(sketch, "E922.MirrorCS", {"start": v(9.22, -7.38) * mm, "end": v(9.22, -6.15) * mm});
            skArc(sketch, "E923.MirrorCS", {"start": v(-9.23, -9.84) * mm, "mid": v(-9.84, -9.22) * mm, "end": v(-9.23, -8.6) * mm});
            skLineSegment(sketch, "E924.MirrorCS", {"start": v(9.84, 4.92) * mm, "end": v(9.84, 6.15) * mm});
            skLineSegment(sketch, "E925.MirrorCS", {"start": v(-9.23, 8.61) * mm, "end": v(-9.23, 9.84) * mm});
            skArc(sketch, "E926.MirrorCS", {"start": v(-9.23, 0) * mm, "mid": v(-9.84, 0.62) * mm, "end": v(-9.23, 1.23) * mm});
            skLineSegment(sketch, "E927.MirrorCS", {"start": v(9.22, -4.92) * mm, "end": v(9.22, -3.69) * mm});
            skLineSegment(sketch, "E928.MirrorCS", {"start": v(-9.84, 3.69) * mm, "end": v(-9.84, 4.92) * mm});
            skArc(sketch, "E929.MirrorCS", {"start": v(-9.23, -7.38) * mm, "mid": v(-9.84, -6.76) * mm, "end": v(-9.23, -6.15) * mm});
            skLineSegment(sketch, "E930.MirrorCS", {"start": v(-9.23, -8.6) * mm, "end": v(-9.23, -7.38) * mm});
            skLineSegment(sketch, "E931.MirrorCS", {"start": v(9.84, 7.38) * mm, "end": v(9.84, 8.61) * mm});
            skLineSegment(sketch, "E932.MirrorCS", {"start": v(-9.23, -9.84) * mm, "end": v(10, -9.84) * mm});
            skLineSegment(sketch, "E933.MirrorCS", {"start": v(9.22, -8.6) * mm, "end": v(-9.23, -8.6) * mm});
            skLineSegment(sketch, "E934.MirrorCS", {"start": v(-10, 9.84) * mm, "end": v(9.22, 9.84) * mm});
            skLineSegment(sketch, "E935.MirrorCS", {"start": v(9.22, -2.46) * mm, "end": v(9.22, -1.23) * mm});
            skLineSegment(sketch, "E936.MirrorCS", {"start": v(-9.84, 6.15) * mm, "end": v(-9.84, 7.38) * mm});
            skArc(sketch, "E937.MirrorCS", {"start": v(9.22, -7.38) * mm, "mid": v(9.84, -8) * mm, "end": v(9.22, -8.6) * mm});
            skArc(sketch, "E938.MirrorCS", {"start": v(9.22, 9.84) * mm, "mid": v(9.84, 9.23) * mm, "end": v(9.22, 8.61) * mm});
            skLineSegment(sketch, "E939.MirrorCS", {"start": v(9.84, -9.84) * mm, "end": v(9.84, -8.6) * mm});
            skLineSegment(sketch, "E940.MirrorCS", {"start": v(10, -7.38) * mm, "end": v(-10, -7.38) * mm});
            skLineSegment(sketch, "E941.MirrorCS", {"start": v(-9.23, -6.15) * mm, "end": v(-9.23, -4.92) * mm});
            skArc(sketch, "E942.MirrorCS", {"start": v(-9.23, 7.38) * mm, "mid": v(-9.84, 8) * mm, "end": v(-9.23, 8.61) * mm});
            skLineSegment(sketch, "E943.MirrorCS", {"start": v(9.22, 0) * mm, "end": v(9.22, 1.23) * mm});
            skLineSegment(sketch, "E944.MirrorCS", {"start": v(-9.84, 8.61) * mm, "end": v(-9.84, 9.84) * mm});
            skArc(sketch, "E945.MirrorCS", {"start": v(9.22, 7.38) * mm, "mid": v(9.84, 6.77) * mm, "end": v(9.22, 6.15) * mm});
            skLineSegment(sketch, "E946.MirrorCS", {"start": v(-9.84, -8.6) * mm, "end": v(-9.84, -7.38) * mm});
            skLineSegment(sketch, "E947.MirrorCS", {"start": v(9.22, 2.46) * mm, "end": v(9.22, 3.7) * mm});
            skArc(sketch, "E948.MirrorCS", {"start": v(9.22, 4.92) * mm, "mid": v(9.84, 4.3) * mm, "end": v(9.22, 3.7) * mm});
            skLineSegment(sketch, "E949.MirrorCS", {"start": v(9.84, -7.38) * mm, "end": v(9.84, -6.15) * mm});
            skLineSegment(sketch, "E950.MirrorCS", {"start": v(10, -6.15) * mm, "end": v(-10, -6.15) * mm});
            skLineSegment(sketch, "E951.MirrorCS", {"start": v(-9.23, -3.69) * mm, "end": v(-9.23, -2.46) * mm});
            skArc(sketch, "E952.MirrorCS", {"start": v(-9.23, 4.92) * mm, "mid": v(-9.84, 5.54) * mm, "end": v(-9.23, 6.15) * mm});
            skLineSegment(sketch, "E953.MirrorCS", {"start": v(9.84, -4.92) * mm, "end": v(9.84, -3.69) * mm});
            skLineSegment(sketch, "E954.MirrorCS", {"start": v(10, 4.92) * mm, "end": v(-10, 4.92) * mm});
            skLineSegment(sketch, "E955.MirrorCS", {"start": v(10, -4.92) * mm, "end": v(-10, -4.92) * mm});
            skLineSegment(sketch, "E956.MirrorCS", {"start": v(9.22, 3.69) * mm, "end": v(-9.23, 3.69) * mm});
            skLineSegment(sketch, "E957.MirrorCS", {"start": v(-9.23, -1.23) * mm, "end": v(-9.23, 0) * mm});
            skArc(sketch, "E958.MirrorCS", {"start": v(9.22, 2.46) * mm, "mid": v(9.84, 1.85) * mm, "end": v(9.22, 1.23) * mm});
            skLineSegment(sketch, "E959.MirrorCS", {"start": v(-9.84, -6.15) * mm, "end": v(-9.84, -4.92) * mm});
            skLineSegment(sketch, "E960.MirrorCS", {"start": v(-9.23, 2.46) * mm, "end": v(9.22, 2.46) * mm});
            skLineSegment(sketch, "E961.MirrorCS", {"start": v(9.22, 4.92) * mm, "end": v(9.22, 6.15) * mm});
            skArc(sketch, "E962.MirrorCS", {"start": v(-9.23, 2.46) * mm, "mid": v(-9.84, 3.08) * mm, "end": v(-9.23, 3.7) * mm});
            skLineSegment(sketch, "E963.MirrorCS", {"start": v(9.84, -2.46) * mm, "end": v(9.84, -1.23) * mm});
            skLineSegment(sketch, "E964.MirrorCS", {"start": v(10, 6.15) * mm, "end": v(-10, 6.15) * mm});
            skLineSegment(sketch, "E965.MirrorCS", {"start": v(9.22, 1.23) * mm, "end": v(-9.23, 1.23) * mm});
            skLineSegment(sketch, "E966.MirrorCS", {"start": v(-9.23, 1.23) * mm, "end": v(-9.23, 2.46) * mm});
            skArc(sketch, "E967.MirrorCS", {"start": v(9.22, 0) * mm, "mid": v(9.84, -0.61) * mm, "end": v(9.22, -1.23) * mm});
            skLineSegment(sketch, "E968.MirrorCS", {"start": v(-9.23, 0) * mm, "end": v(9.22, 0) * mm});
            skLineSegment(sketch, "E969.MirrorCS", {"start": v(9.22, 7.38) * mm, "end": v(9.22, 8.61) * mm});
            skArc(sketch, "E970.MirrorCS", {"start": v(9.22, -2.46) * mm, "mid": v(9.84, -3.07) * mm, "end": v(9.22, -3.69) * mm});
            skLineSegment(sketch, "E971.MirrorCS", {"start": v(-9.84, -9.5) * mm, "end": v(-9.84, -1.23) * mm});
            skLineSegment(sketch, "E972.MirrorCS", {"start": v(10, 7.38) * mm, "end": v(10, 8.61) * mm});
            skLineSegment(sketch, "E973.MirrorCS", {"start": v(10, 8.61) * mm, "end": v(10, 9.84) * mm});
            skLineSegment(sketch, "E974.MirrorCS", {"start": v(-9.23, -2.46) * mm, "end": v(9.22, -2.46) * mm});
            skLineSegment(sketch, "E975.MirrorCS", {"start": v(10, -2.46) * mm, "end": v(10, -1.23) * mm});
            skLineSegment(sketch, "E976.MirrorCS", {"start": v(-10, -2.46) * mm, "end": v(-10, -3.69) * mm});
            skLineSegment(sketch, "E977.MirrorCS", {"start": v(10, 8.61) * mm, "end": v(-10, 8.61) * mm});
            skLineSegment(sketch, "E978.MirrorCS", {"start": v(-9.23, 6.15) * mm, "end": v(-9.23, 7.38) * mm});
            skLineSegment(sketch, "E979.MirrorCS", {"start": v(10, -4.92) * mm, "end": v(10, -3.69) * mm});
            skLineSegment(sketch, "E980.MirrorCS", {"start": v(10, -3.69) * mm, "end": v(10, -2.46) * mm});
            skLineSegment(sketch, "E981.MirrorCS", {"start": v(10, -6.15) * mm, "end": v(10, -4.92) * mm});
            skLineSegment(sketch, "E982.MirrorCS", {"start": v(10, 10) * mm, "end": v(10, -10) * mm});
            skLineSegment(sketch, "E983.MirrorCS", {"start": v(10, -7.38) * mm, "end": v(10, -6.15) * mm});
            skArc(sketch, "E984.MirrorCS", {"start": v(-9.23, -2.46) * mm, "mid": v(-9.84, -1.84) * mm, "end": v(-9.23, -1.23) * mm});
            skLineSegment(sketch, "E985.MirrorCS", {"start": v(-9.23, 3.7) * mm, "end": v(-9.23, 4.92) * mm});
            skLineSegment(sketch, "E986.MirrorCS", {"start": v(10, -8.6) * mm, "end": v(10, -7.38) * mm});
            skLineSegment(sketch, "E987.MirrorCS", {"start": v(10, -9.84) * mm, "end": v(10, -8.6) * mm});
            skLineSegment(sketch, "E988.MirrorCS", {"start": v(-10, 10) * mm, "end": v(-10, -10) * mm});
            skPoint(sketch, "E989.MirrorP", {"position": v(0, 0) * mm});
            skLineSegment(sketch, "E990.MirrorCS", {"start": v(9.84, 2.46) * mm, "end": v(9.84, 3.7) * mm});
            skLineSegment(sketch, "E991.MirrorCS", {"start": v(10, -1.23) * mm, "end": v(10, 0) * mm});
            skArc(sketch, "E992.MirrorCS", {"start": v(9.22, -4.92) * mm, "mid": v(9.84, -5.53) * mm, "end": v(9.22, -6.15) * mm});
            skLineSegment(sketch, "E993.MirrorCS", {"start": v(10, 7.38) * mm, "end": v(-10, 7.38) * mm});
            skLineSegment(sketch, "E994.MirrorCS", {"start": v(-9.84, -3.69) * mm, "end": v(-9.84, -2.46) * mm});
            skLineSegment(sketch, "E995.MirrorCS", {"start": v(10, -1.23) * mm, "end": v(-10, -1.23) * mm});
            skLineSegment(sketch, "E996.MirrorCS", {"start": v(9.84, 1.23) * mm, "end": v(9.84, 9.5) * mm});
            skLineSegment(sketch, "E997.MirrorCS", {"start": v(10, -10) * mm, "end": v(-10, -10) * mm});
            skLineSegment(sketch, "E998.MirrorCS", {"start": v(-10, 7.38) * mm, "end": v(-10, 6.15) * mm});
            skArc(sketch, "E999.MirrorCS", {"start": v(-9.23, -4.92) * mm, "mid": v(-9.84, -4.3) * mm, "end": v(-9.23, -3.69) * mm});
            skLineSegment(sketch, "E1000.MirrorCS", {"start": v(9.22, -9.84) * mm, "end": v(9.22, -8.6) * mm});
            skLineSegment(sketch, "E1001.MirrorCS", {"start": v(9.84, 1.23) * mm, "end": v(9.84, 2.46) * mm});
            skLineSegment(sketch, "E1002.MirrorCS", {"start": v(9.22, -3.69) * mm, "end": v(-9.23, -3.69) * mm});
            skSolve(sketch);
        }
        {
            var Q0;
            Q0=qCreatedBy(id+"F7.planeOp",FACE);
            var sketch = newSketch(context, id + "F16", { "sketchPlane" : qUnion([Q0])});
            skCircle(sketch, "E1003", {"center": v(-9.84, 1.43) * mm, "radius": 0.2 * mm});
            skSolve(sketch);
        }
        {
            var Q0;
            Q0=makeQuery(id+"F16.imprint","IMPRINT",FACE,{"disambiguationData":[TD([[makeQuery(id+"F16.imprint","IMPRINT",EDGE,{"derivedFrom":sQuery(id+"F16.wireOp",EDGE,"E1003")}),1.0]])]});
            var Q1;
            Q1=sQuery(id+"F15.wireOp",EDGE,"E934.MirrorCS");
            var Q2;
            Q2=sQuery(id+"F15.wireOp",EDGE,"E938.MirrorCS");
            var Q3;
            Q3=sQuery(id+"F15.wireOp",EDGE,"E880.MirrorCS");
            var Q4;
            Q4=sQuery(id+"F15.wireOp",EDGE,"E942.MirrorCS");
            var Q5;
            Q5=sQuery(id+"F15.wireOp",EDGE,"E885.MirrorCS");
            var Q6;
            Q6=sQuery(id+"F15.wireOp",EDGE,"E945.MirrorCS");
            var Q7;
            Q7=sQuery(id+"F15.wireOp",EDGE,"E894.MirrorCS");
            var Q8;
            Q8=sQuery(id+"F15.wireOp",EDGE,"E952.MirrorCS");
            var Q9;
            Q9=sQuery(id+"F15.wireOp",EDGE,"E889.MirrorCS");
            var Q10;
            Q10=sQuery(id+"F15.wireOp",EDGE,"E948.MirrorCS");
            var Q11;
            Q11=sQuery(id+"F15.wireOp",EDGE,"E956.MirrorCS");
            var Q12;
            Q12=sQuery(id+"F15.wireOp",EDGE,"E962.MirrorCS");
            var Q13;
            Q13=sQuery(id+"F15.wireOp",EDGE,"E960.MirrorCS");
            var Q14;
            Q14=sQuery(id+"F15.wireOp",EDGE,"E958.MirrorCS");
            var Q15;
            Q15=sQuery(id+"F15.wireOp",EDGE,"E965.MirrorCS");
            var Q16;
            Q16=sQuery(id+"F15.wireOp",EDGE,"E926.MirrorCS");
            var Q17;
            Q17=sQuery(id+"F15.wireOp",EDGE,"E968.MirrorCS");
            var Q18;
            Q18=sQuery(id+"F15.wireOp",EDGE,"E967.MirrorCS");
            var Q19;
            Q19=sQuery(id+"F15.wireOp",EDGE,"E916.MirrorCS");
            var Q20;
            Q20=sQuery(id+"F15.wireOp",EDGE,"E984.MirrorCS");
            var Q21;
            Q21=sQuery(id+"F15.wireOp",EDGE,"E974.MirrorCS");
            var Q22;
            Q22=sQuery(id+"F15.wireOp",EDGE,"E970.MirrorCS");
            var Q23;
            Q23=sQuery(id+"F15.wireOp",EDGE,"E1002.MirrorCS");
            var Q24;
            Q24=sQuery(id+"F15.wireOp",EDGE,"E999.MirrorCS");
            var Q25;
            Q25=sQuery(id+"F15.wireOp",EDGE,"E856.MirrorCS");
            var Q26;
            Q26=sQuery(id+"F15.wireOp",EDGE,"E992.MirrorCS");
            var Q27;
            Q27=sQuery(id+"F15.wireOp",EDGE,"E862.MirrorCS");
            var Q28;
            Q28=sQuery(id+"F15.wireOp",EDGE,"E929.MirrorCS");
            var Q29;
            Q29=sQuery(id+"F15.wireOp",EDGE,"E868.MirrorCS");
            var Q30;
            Q30=sQuery(id+"F15.wireOp",EDGE,"E937.MirrorCS");
            var Q31;
            Q31=sQuery(id+"F15.wireOp",EDGE,"E933.MirrorCS");
            var Q32;
            Q32=sQuery(id+"F15.wireOp",EDGE,"E923.MirrorCS");
            var Q33;
            Q33=sQuery(id+"F15.wireOp",EDGE,"E932.MirrorCS");
            sweep(context, id + "F17", {"operationType" : NewBodyOperationType.ADD, "profiles" : qUnion([Q0]), "path" : qUnion([Q1, Q2, Q3, Q4, Q5, Q6, Q7, Q8, Q9, Q10, Q11, Q12, Q13, Q14, Q15, Q16, Q17, Q18, Q19, Q20, Q21, Q22, Q23, Q24, Q25, Q26, Q27, Q28, Q29, Q30, Q31, Q32, Q33])});
        }
        {
            var Q0;
            Q0=qCreatedBy(id+"F14.planeOp",FACE);
            cPlane(context, id + "F18", {"entities" : qUnion([Q0]), "cplaneType" : CPlaneType.OFFSET, "offset" : getVariable(context, 'd'), "width" : 150 * mm, "height" : 150 * mm});
        }
        {
            var Q0;
            Q0=qCreatedBy(id+"F18.planeOp",FACE);
            var sketch = newSketch(context, id + "F19", { "sketchPlane" : qUnion([Q0])});
            skLineSegment(sketch, "E1004.bottom", {"start": v(10, 10) * mm, "end": v(-10, 10) * mm});
            skLineSegment(sketch, "E1004.top", {"start": v(10, -10) * mm, "end": v(-10, -10) * mm});
            skLineSegment(sketch, "E1004.left", {"start": v(10, 10) * mm, "end": v(10, -10) * mm});
            skLineSegment(sketch, "E1004.right", {"start": v(-10, 10) * mm, "end": v(-10, -10) * mm});
            skPoint(sketch, "E1004.middle", {"position": v(0, 0) * mm});
            skLineSegment(sketch, "E1005", {"start": v(-10, 10) * mm, "end": v(-9.84, 10) * mm});
            skLineSegment(sketch, "E1006", {"start": v(-9.84, 10) * mm, "end": v(-8.61, 10) * mm});
            skLineSegment(sketch, "E1007", {"start": v(-8.61, 10) * mm, "end": v(-7.38, 10) * mm});
            skLineSegment(sketch, "E1008", {"start": v(-7.38, 10) * mm, "end": v(-6.15, 10) * mm});
            skLineSegment(sketch, "E1009", {"start": v(-6.15, 10) * mm, "end": v(-4.92, 10) * mm});
            skLineSegment(sketch, "E1010", {"start": v(-4.92, 10) * mm, "end": v(-3.7, 10) * mm});
            skLineSegment(sketch, "E1011", {"start": v(-3.7, 10) * mm, "end": v(-2.46, 10) * mm});
            skLineSegment(sketch, "E1012", {"start": v(-2.46, 10) * mm, "end": v(-1.23, 10) * mm});
            skLineSegment(sketch, "E1013", {"start": v(-1.23, 10) * mm, "end": v(0, 10) * mm});
            skLineSegment(sketch, "E1014", {"start": v(0, 10) * mm, "end": v(1.23, 10) * mm});
            skLineSegment(sketch, "E1015", {"start": v(1.23, 10) * mm, "end": v(2.46, 10) * mm});
            skLineSegment(sketch, "E1016", {"start": v(2.46, 10) * mm, "end": v(3.69, 10) * mm});
            skLineSegment(sketch, "E1017", {"start": v(3.69, 10) * mm, "end": v(4.92, 10) * mm});
            skLineSegment(sketch, "E1018", {"start": v(4.92, 10) * mm, "end": v(6.15, 10) * mm});
            skLineSegment(sketch, "E1019", {"start": v(6.15, 10) * mm, "end": v(7.38, 10) * mm});
            skLineSegment(sketch, "E1020", {"start": v(7.38, 10) * mm, "end": v(8.6, 10) * mm});
            skLineSegment(sketch, "E1021", {"start": v(8.6, 10) * mm, "end": v(9.84, 10) * mm});
            skLineSegment(sketch, "E1022", {"start": v(9.84, 10) * mm, "end": v(10, 10) * mm});
            skLineSegment(sketch, "E1023", {"start": v(-9.84, 10) * mm, "end": v(-9.84, -10) * mm});
            skLineSegment(sketch, "E1024", {"start": v(-9.84, -10) * mm, "end": v(-10, -10) * mm});
            skLineSegment(sketch, "E1025", {"start": v(-8.61, 10) * mm, "end": v(-8.61, -10) * mm});
            skLineSegment(sketch, "E1026", {"start": v(-8.61, -10) * mm, "end": v(-9.84, -10) * mm});
            skLineSegment(sketch, "E1027", {"start": v(-7.38, 10) * mm, "end": v(-7.38, -10) * mm});
            skLineSegment(sketch, "E1028", {"start": v(-7.38, -10) * mm, "end": v(-8.61, -10) * mm});
            skLineSegment(sketch, "E1029", {"start": v(-6.15, 10) * mm, "end": v(-6.15, -10) * mm});
            skLineSegment(sketch, "E1030", {"start": v(-6.15, -10) * mm, "end": v(-7.38, -10) * mm});
            skLineSegment(sketch, "E1031", {"start": v(-4.92, 10) * mm, "end": v(-4.92, -10) * mm});
            skLineSegment(sketch, "E1032", {"start": v(-4.92, -10) * mm, "end": v(-6.15, -10) * mm});
            skLineSegment(sketch, "E1033", {"start": v(-3.7, 10) * mm, "end": v(-3.7, -10) * mm});
            skLineSegment(sketch, "E1034", {"start": v(-3.7, -10) * mm, "end": v(-4.92, -10) * mm});
            skLineSegment(sketch, "E1035", {"start": v(-2.46, 10) * mm, "end": v(-2.46, -10) * mm});
            skLineSegment(sketch, "E1036", {"start": v(-2.46, -10) * mm, "end": v(-3.7, -10) * mm});
            skLineSegment(sketch, "E1037", {"start": v(-1.23, 10) * mm, "end": v(-1.23, -10) * mm});
            skLineSegment(sketch, "E1038", {"start": v(-1.23, -10) * mm, "end": v(-2.46, -10) * mm});
            skLineSegment(sketch, "E1039", {"start": v(0, 10) * mm, "end": v(0, -10) * mm});
            skLineSegment(sketch, "E1040", {"start": v(0, -10) * mm, "end": v(-1.23, -10) * mm});
            skLineSegment(sketch, "E1041", {"start": v(1.23, 10) * mm, "end": v(1.23, -10) * mm});
            skLineSegment(sketch, "E1042", {"start": v(1.23, -10) * mm, "end": v(0, -10) * mm});
            skLineSegment(sketch, "E1043", {"start": v(2.46, 10) * mm, "end": v(2.46, -10) * mm});
            skLineSegment(sketch, "E1044", {"start": v(2.46, -10) * mm, "end": v(1.23, -10) * mm});
            skLineSegment(sketch, "E1045", {"start": v(3.69, 10) * mm, "end": v(3.69, -10) * mm});
            skLineSegment(sketch, "E1046", {"start": v(3.69, -10) * mm, "end": v(2.46, -10) * mm});
            skLineSegment(sketch, "E1047", {"start": v(4.92, 10) * mm, "end": v(4.92, -10) * mm});
            skLineSegment(sketch, "E1048", {"start": v(4.92, -10) * mm, "end": v(3.69, -10) * mm});
            skLineSegment(sketch, "E1049", {"start": v(6.15, 10) * mm, "end": v(6.15, -10) * mm});
            skLineSegment(sketch, "E1050", {"start": v(6.15, -10) * mm, "end": v(4.92, -10) * mm});
            skLineSegment(sketch, "E1051", {"start": v(7.38, 10) * mm, "end": v(7.38, -10) * mm});
            skLineSegment(sketch, "E1052", {"start": v(7.38, -10) * mm, "end": v(6.15, -10) * mm});
            skLineSegment(sketch, "E1053", {"start": v(8.6, 10) * mm, "end": v(8.6, -10) * mm});
            skLineSegment(sketch, "E1054", {"start": v(8.6, -10) * mm, "end": v(7.38, -10) * mm});
            skLineSegment(sketch, "E1055", {"start": v(9.84, 10) * mm, "end": v(9.84, -10) * mm});
            skLineSegment(sketch, "E1056", {"start": v(9.84, -10) * mm, "end": v(8.6, -10) * mm});
            skLineSegment(sketch, "E1057", {"start": v(10, -10) * mm, "end": v(9.84, -10) * mm});
            skLineSegment(sketch, "E1058", {"start": v(-10, 9.84) * mm, "end": v(-9.84, 9.84) * mm});
            skLineSegment(sketch, "E1059", {"start": v(-9.84, 9.84) * mm, "end": v(-8.61, 9.84) * mm});
            skLineSegment(sketch, "E1060", {"start": v(-8.61, 9.84) * mm, "end": v(-7.38, 9.84) * mm});
            skLineSegment(sketch, "E1061", {"start": v(-7.38, 9.84) * mm, "end": v(-6.15, 9.84) * mm});
            skLineSegment(sketch, "E1062", {"start": v(-6.15, 9.84) * mm, "end": v(-4.92, 9.84) * mm});
            skLineSegment(sketch, "E1063", {"start": v(-4.92, 9.84) * mm, "end": v(-3.7, 9.84) * mm});
            skLineSegment(sketch, "E1064", {"start": v(-3.7, 9.84) * mm, "end": v(-2.46, 9.84) * mm});
            skLineSegment(sketch, "E1065", {"start": v(-2.46, 9.84) * mm, "end": v(-1.23, 9.84) * mm});
            skLineSegment(sketch, "E1066", {"start": v(-1.23, 9.84) * mm, "end": v(0, 9.84) * mm});
            skLineSegment(sketch, "E1067", {"start": v(0, 9.84) * mm, "end": v(1.23, 9.84) * mm});
            skLineSegment(sketch, "E1068", {"start": v(1.23, 9.84) * mm, "end": v(2.46, 9.84) * mm});
            skLineSegment(sketch, "E1069", {"start": v(2.46, 9.84) * mm, "end": v(3.69, 9.84) * mm});
            skLineSegment(sketch, "E1070", {"start": v(3.69, 9.84) * mm, "end": v(4.92, 9.84) * mm});
            skLineSegment(sketch, "E1071", {"start": v(4.92, 9.84) * mm, "end": v(6.15, 9.84) * mm});
            skLineSegment(sketch, "E1072", {"start": v(6.15, 9.84) * mm, "end": v(7.38, 9.84) * mm});
            skLineSegment(sketch, "E1073", {"start": v(7.38, 9.84) * mm, "end": v(8.6, 9.84) * mm});
            skLineSegment(sketch, "E1074", {"start": v(8.6, 9.84) * mm, "end": v(9.84, 9.84) * mm});
            skLineSegment(sketch, "E1075", {"start": v(9.84, 9.84) * mm, "end": v(10, 9.84) * mm});
            skLineSegment(sketch, "E1076", {"start": v(-10, -9.84) * mm, "end": v(-9.84, -9.84) * mm});
            skLineSegment(sketch, "E1077", {"start": v(-9.84, -9.84) * mm, "end": v(-8.61, -9.84) * mm});
            skLineSegment(sketch, "E1078", {"start": v(-8.61, -9.84) * mm, "end": v(-7.38, -9.84) * mm});
            skLineSegment(sketch, "E1079", {"start": v(-7.38, -9.84) * mm, "end": v(-6.15, -9.84) * mm});
            skLineSegment(sketch, "E1080", {"start": v(-6.15, -9.84) * mm, "end": v(-4.92, -9.84) * mm});
            skLineSegment(sketch, "E1081", {"start": v(-4.92, -9.84) * mm, "end": v(-3.7, -9.84) * mm});
            skLineSegment(sketch, "E1082", {"start": v(-3.7, -9.84) * mm, "end": v(-2.46, -9.84) * mm});
            skLineSegment(sketch, "E1083", {"start": v(-2.46, -9.84) * mm, "end": v(-1.23, -9.84) * mm});
            skLineSegment(sketch, "E1084", {"start": v(-1.23, -9.84) * mm, "end": v(0, -9.84) * mm});
            skLineSegment(sketch, "E1085", {"start": v(0, -9.84) * mm, "end": v(1.23, -9.84) * mm});
            skLineSegment(sketch, "E1086", {"start": v(1.23, -9.84) * mm, "end": v(2.46, -9.84) * mm});
            skLineSegment(sketch, "E1087", {"start": v(2.46, -9.84) * mm, "end": v(3.69, -9.84) * mm});
            skLineSegment(sketch, "E1088", {"start": v(3.69, -9.84) * mm, "end": v(4.92, -9.84) * mm});
            skLineSegment(sketch, "E1089", {"start": v(4.92, -9.84) * mm, "end": v(6.15, -9.84) * mm});
            skLineSegment(sketch, "E1090", {"start": v(6.15, -9.84) * mm, "end": v(7.38, -9.84) * mm});
            skLineSegment(sketch, "E1091", {"start": v(7.38, -9.84) * mm, "end": v(8.6, -9.84) * mm});
            skLineSegment(sketch, "E1092", {"start": v(8.6, -9.84) * mm, "end": v(9.84, -9.84) * mm});
            skLineSegment(sketch, "E1093", {"start": v(9.84, -9.84) * mm, "end": v(10, -9.84) * mm});
            skLineSegment(sketch, "E1094", {"start": v(-10, 10) * mm, "end": v(-10, 9.84) * mm});
            skLineSegment(sketch, "E1095", {"start": v(-10, -9.84) * mm, "end": v(-10, -10) * mm});
            skLineSegment(sketch, "E1096", {"start": v(10, -9.84) * mm, "end": v(10, -10) * mm});
            skLineSegment(sketch, "E1097", {"start": v(10, 9.84) * mm, "end": v(10, 10) * mm});
            skLineSegment(sketch, "E1098", {"start": v(-10, 9.84) * mm, "end": v(-10, 9.23) * mm});
            skLineSegment(sketch, "E1099", {"start": v(-10, 9.23) * mm, "end": v(-9.84, 9.23) * mm});
            skLineSegment(sketch, "E1100", {"start": v(-9.84, 9.23) * mm, "end": v(-8.61, 9.23) * mm});
            skLineSegment(sketch, "E1101", {"start": v(-8.61, 9.23) * mm, "end": v(-7.38, 9.23) * mm});
            skLineSegment(sketch, "E1102", {"start": v(-7.38, 9.23) * mm, "end": v(-6.15, 9.23) * mm});
            skLineSegment(sketch, "E1103", {"start": v(-6.15, 9.23) * mm, "end": v(-4.92, 9.23) * mm});
            skLineSegment(sketch, "E1104", {"start": v(-4.92, 9.23) * mm, "end": v(-3.7, 9.23) * mm});
            skLineSegment(sketch, "E1105", {"start": v(-3.7, 9.23) * mm, "end": v(-2.46, 9.23) * mm});
            skLineSegment(sketch, "E1106", {"start": v(-2.46, 9.23) * mm, "end": v(-1.23, 9.23) * mm});
            skLineSegment(sketch, "E1107", {"start": v(-1.23, 9.23) * mm, "end": v(0, 9.23) * mm});
            skLineSegment(sketch, "E1108", {"start": v(0, 9.23) * mm, "end": v(1.23, 9.23) * mm});
            skLineSegment(sketch, "E1109", {"start": v(1.23, 9.23) * mm, "end": v(2.46, 9.23) * mm});
            skLineSegment(sketch, "E1110", {"start": v(2.46, 9.23) * mm, "end": v(3.69, 9.23) * mm});
            skLineSegment(sketch, "E1111", {"start": v(3.69, 9.23) * mm, "end": v(4.92, 9.23) * mm});
            skLineSegment(sketch, "E1112", {"start": v(4.92, 9.23) * mm, "end": v(6.15, 9.23) * mm});
            skLineSegment(sketch, "E1113", {"start": v(6.15, 9.23) * mm, "end": v(7.38, 9.23) * mm});
            skLineSegment(sketch, "E1114", {"start": v(7.38, 9.23) * mm, "end": v(8.6, 9.23) * mm});
            skLineSegment(sketch, "E1115", {"start": v(8.6, 9.23) * mm, "end": v(9.84, 9.23) * mm});
            skLineSegment(sketch, "E1116", {"start": v(9.84, 9.23) * mm, "end": v(10, 9.23) * mm});
            skLineSegment(sketch, "E1117", {"start": v(10, 9.23) * mm, "end": v(10, 9.84) * mm});
            skLineSegment(sketch, "E1118", {"start": v(-10, -9.84) * mm, "end": v(-10, -9.23) * mm});
            skLineSegment(sketch, "E1119", {"start": v(-10, -9.23) * mm, "end": v(-9.84, -9.23) * mm});
            skLineSegment(sketch, "E1120", {"start": v(-9.84, -9.23) * mm, "end": v(-8.61, -9.23) * mm});
            skLineSegment(sketch, "E1121", {"start": v(-8.61, -9.23) * mm, "end": v(-7.38, -9.23) * mm});
            skLineSegment(sketch, "E1122", {"start": v(-7.38, -9.23) * mm, "end": v(-6.15, -9.23) * mm});
            skLineSegment(sketch, "E1123", {"start": v(-6.15, -9.23) * mm, "end": v(-4.92, -9.23) * mm});
            skLineSegment(sketch, "E1124", {"start": v(-4.92, -9.23) * mm, "end": v(-3.7, -9.23) * mm});
            skLineSegment(sketch, "E1125", {"start": v(-3.7, -9.23) * mm, "end": v(-2.46, -9.23) * mm});
            skLineSegment(sketch, "E1126", {"start": v(-2.46, -9.23) * mm, "end": v(-1.23, -9.23) * mm});
            skLineSegment(sketch, "E1127", {"start": v(-1.23, -9.23) * mm, "end": v(0, -9.23) * mm});
            skLineSegment(sketch, "E1128", {"start": v(0, -9.23) * mm, "end": v(1.23, -9.23) * mm});
            skLineSegment(sketch, "E1129", {"start": v(1.23, -9.23) * mm, "end": v(2.46, -9.23) * mm});
            skLineSegment(sketch, "E1130", {"start": v(2.46, -9.23) * mm, "end": v(3.69, -9.23) * mm});
            skLineSegment(sketch, "E1131", {"start": v(3.69, -9.23) * mm, "end": v(4.92, -9.23) * mm});
            skLineSegment(sketch, "E1132", {"start": v(4.92, -9.23) * mm, "end": v(6.15, -9.23) * mm});
            skLineSegment(sketch, "E1133", {"start": v(6.15, -9.23) * mm, "end": v(7.38, -9.23) * mm});
            skLineSegment(sketch, "E1134", {"start": v(7.38, -9.23) * mm, "end": v(8.61, -9.23) * mm});
            skLineSegment(sketch, "E1135", {"start": v(8.6, -9.23) * mm, "end": v(9.84, -9.23) * mm});
            skLineSegment(sketch, "E1136", {"start": v(9.84, -9.23) * mm, "end": v(10, -9.23) * mm});
            skLineSegment(sketch, "E1137", {"start": v(9.84, -10) * mm, "end": v(9.84, 9.23) * mm});
            skLineSegment(sketch, "E1138", {"start": v(10, -9.22) * mm, "end": v(10, -9.84) * mm});
            skLineSegment(sketch, "E1139", {"start": v(8.6, 9.23) * mm, "end": v(8.6, -9.23) * mm});
            skLineSegment(sketch, "E1140", {"start": v(7.38, -9.22) * mm, "end": v(7.38, 9.23) * mm});
            skLineSegment(sketch, "E1141", {"start": v(6.15, 9.23) * mm, "end": v(6.15, -9.23) * mm});
            skLineSegment(sketch, "E1142", {"start": v(4.92, -9.23) * mm, "end": v(4.92, 9.23) * mm});
            skLineSegment(sketch, "E1143", {"start": v(3.69, 9.23) * mm, "end": v(3.69, -9.23) * mm});
            skLineSegment(sketch, "E1144", {"start": v(2.46, -9.23) * mm, "end": v(2.46, 9.23) * mm});
            skLineSegment(sketch, "E1145", {"start": v(1.23, 9.23) * mm, "end": v(1.23, -9.23) * mm});
            skLineSegment(sketch, "E1146", {"start": v(0, -9.23) * mm, "end": v(0, 9.23) * mm});
            skLineSegment(sketch, "E1147", {"start": v(-1.23, 9.23) * mm, "end": v(-1.23, -9.23) * mm});
            skLineSegment(sketch, "E1148", {"start": v(-2.46, -9.23) * mm, "end": v(-2.46, 9.23) * mm});
            skLineSegment(sketch, "E1149", {"start": v(-3.7, 9.23) * mm, "end": v(-3.7, -9.23) * mm});
            skLineSegment(sketch, "E1150", {"start": v(-4.92, -9.23) * mm, "end": v(-4.92, 9.23) * mm});
            skLineSegment(sketch, "E1151", {"start": v(-6.15, 9.23) * mm, "end": v(-6.15, -9.23) * mm});
            skLineSegment(sketch, "E1152", {"start": v(-7.38, -9.23) * mm, "end": v(-7.38, 9.23) * mm});
            skLineSegment(sketch, "E1153", {"start": v(-8.61, 9.23) * mm, "end": v(-8.61, -9.23) * mm});
            skArc(sketch, "E1154", {"start": v(9.84, 9.23) * mm, "mid": v(9.22, 9.84) * mm, "end": v(8.6, 9.23) * mm});
            skArc(sketch, "E1155", {"start": v(7.38, -9.22) * mm, "mid": v(8, -9.84) * mm, "end": v(8.6, -9.23) * mm});
            skArc(sketch, "E1156", {"start": v(7.38, 9.23) * mm, "mid": v(6.76, 9.84) * mm, "end": v(6.15, 9.23) * mm});
            skArc(sketch, "E1157", {"start": v(4.92, -9.23) * mm, "mid": v(5.53, -9.84) * mm, "end": v(6.15, -9.23) * mm});
            skArc(sketch, "E1158", {"start": v(4.92, 9.23) * mm, "mid": v(4.3, 9.84) * mm, "end": v(3.69, 9.23) * mm});
            skArc(sketch, "E1159", {"start": v(2.46, 9.23) * mm, "mid": v(1.84, 9.84) * mm, "end": v(1.23, 9.23) * mm});
            skArc(sketch, "E1160", {"start": v(2.46, -9.23) * mm, "mid": v(3.07, -9.84) * mm, "end": v(3.69, -9.23) * mm});
            skArc(sketch, "E1161", {"start": v(0, 9.23) * mm, "mid": v(-0.62, 9.84) * mm, "end": v(-1.23, 9.23) * mm});
            skArc(sketch, "E1162", {"start": v(-2.46, 9.23) * mm, "mid": v(-3.08, 9.84) * mm, "end": v(-3.7, 9.23) * mm});
            skArc(sketch, "E1163", {"start": v(-4.92, 9.23) * mm, "mid": v(-5.54, 9.84) * mm, "end": v(-6.15, 9.23) * mm});
            skArc(sketch, "E1164", {"start": v(-2.46, -9.23) * mm, "mid": v(-1.85, -9.84) * mm, "end": v(-1.23, -9.23) * mm});
            skArc(sketch, "E1165", {"start": v(-4.92, -9.23) * mm, "mid": v(-4.3, -9.84) * mm, "end": v(-3.69, -9.23) * mm});
            skArc(sketch, "E1166", {"start": v(-9.84, -9.23) * mm, "mid": v(-9.23, -9.84) * mm, "end": v(-8.61, -9.23) * mm});
            skArc(sketch, "E1167", {"start": v(0, -9.23) * mm, "mid": v(0.61, -9.84) * mm, "end": v(1.23, -9.23) * mm});
            skArc(sketch, "E1168", {"start": v(-7.38, -9.23) * mm, "mid": v(-6.77, -9.84) * mm, "end": v(-6.15, -9.23) * mm});
            skLineSegment(sketch, "E1169", {"start": v(-9.84, -9.23) * mm, "end": v(-9.84, 10) * mm});
            skArc(sketch, "E1170", {"start": v(-7.38, 9.23) * mm, "mid": v(-8, 9.84) * mm, "end": v(-8.61, 9.23) * mm});
            skSolve(sketch);
        }
        {
            var Q0;
            Q0=qCreatedBy(id+"F3.planeOp",FACE);
            var sketch = newSketch(context, id + "F20", { "sketchPlane" : qUnion([Q0])});
            skCircle(sketch, "E1171", {"center": v(-9.84, 1.84) * mm, "radius": 0.2 * mm});
            skSolve(sketch);
        }
        {
            var Q0;
            Q0=makeQuery(id+"F20.imprint","IMPRINT",FACE,{"disambiguationData":[TD([[makeQuery(id+"F20.imprint","IMPRINT",EDGE,{"derivedFrom":sQuery(id+"F20.wireOp",EDGE,"E1171")}),1.0]])]});
            var Q1;
            Q1=sQuery(id+"F19.wireOp",EDGE,"E1137");
            var Q2;
            Q2=sQuery(id+"F19.wireOp",EDGE,"E1154");
            var Q3;
            Q3=sQuery(id+"F19.wireOp",EDGE,"E1139");
            var Q4;
            Q4=sQuery(id+"F19.wireOp",EDGE,"E1155");
            var Q5;
            Q5=sQuery(id+"F19.wireOp",EDGE,"E1140");
            var Q6;
            Q6=sQuery(id+"F19.wireOp",EDGE,"E1156");
            var Q7;
            Q7=sQuery(id+"F19.wireOp",EDGE,"E1141");
            var Q8;
            Q8=sQuery(id+"F19.wireOp",EDGE,"E1157");
            var Q9;
            Q9=sQuery(id+"F19.wireOp",EDGE,"E1142");
            var Q10;
            Q10=sQuery(id+"F19.wireOp",EDGE,"E1158");
            var Q11;
            Q11=sQuery(id+"F19.wireOp",EDGE,"E1143");
            var Q12;
            Q12=sQuery(id+"F19.wireOp",EDGE,"E1160");
            var Q13;
            Q13=sQuery(id+"F19.wireOp",EDGE,"E1144");
            var Q14;
            Q14=sQuery(id+"F19.wireOp",EDGE,"E1159");
            var Q15;
            Q15=sQuery(id+"F19.wireOp",EDGE,"E1145");
            var Q16;
            Q16=sQuery(id+"F19.wireOp",EDGE,"E1167");
            var Q17;
            Q17=sQuery(id+"F19.wireOp",EDGE,"E1146");
            var Q18;
            Q18=sQuery(id+"F19.wireOp",EDGE,"E1161");
            var Q19;
            Q19=sQuery(id+"F19.wireOp",EDGE,"E1147");
            var Q20;
            Q20=sQuery(id+"F19.wireOp",EDGE,"E1164");
            var Q21;
            Q21=sQuery(id+"F19.wireOp",EDGE,"E1148");
            var Q22;
            Q22=sQuery(id+"F19.wireOp",EDGE,"E1162");
            var Q23;
            Q23=sQuery(id+"F19.wireOp",EDGE,"E1149");
            var Q24;
            Q24=sQuery(id+"F19.wireOp",EDGE,"E1165");
            var Q25;
            Q25=sQuery(id+"F19.wireOp",EDGE,"E1150");
            var Q26;
            Q26=sQuery(id+"F19.wireOp",EDGE,"E1163");
            var Q27;
            Q27=sQuery(id+"F19.wireOp",EDGE,"E1151");
            var Q28;
            Q28=sQuery(id+"F19.wireOp",EDGE,"E1168");
            var Q29;
            Q29=sQuery(id+"F19.wireOp",EDGE,"E1152");
            var Q30;
            Q30=sQuery(id+"F19.wireOp",EDGE,"E1170");
            var Q31;
            Q31=sQuery(id+"F19.wireOp",EDGE,"E1153");
            var Q32;
            Q32=sQuery(id+"F19.wireOp",EDGE,"E1166");
            var Q33;
            Q33=sQuery(id+"F19.wireOp",EDGE,"E1169");
            sweep(context, id + "F21", {"operationType" : NewBodyOperationType.ADD, "profiles" : qUnion([Q0]), "path" : qUnion([Q1, Q2, Q3, Q4, Q5, Q6, Q7, Q8, Q9, Q10, Q11, Q12, Q13, Q14, Q15, Q16, Q17, Q18, Q19, Q20, Q21, Q22, Q23, Q24, Q25, Q26, Q27, Q28, Q29, Q30, Q31, Q32, Q33])});
        }
        {
            var Q0;
            Q0=qCreatedBy(id+"F18.planeOp",FACE);
            cPlane(context, id + "F22", {"entities" : qUnion([Q0]), "cplaneType" : CPlaneType.OFFSET, "offset" : getVariable(context, 'd'), "width" : 150 * mm, "height" : 150 * mm});
        }
        {
            var Q0;
            Q0=qCreatedBy(id+"F22.planeOp",FACE);
            var sketch = newSketch(context, id + "F23", { "sketchPlane" : qUnion([Q0])});
            skLineSegment(sketch, "E1172.bottom", {"start": v(10, 10) * mm, "end": v(10, 30) * mm});
            skLineSegment(sketch, "E1172.top", {"start": v(-10, 10) * mm, "end": v(-10, 30) * mm});
            skLineSegment(sketch, "E1172.left", {"start": v(10, 10) * mm, "end": v(-10, 10) * mm});
            skLineSegment(sketch, "E1172.right", {"start": v(10, 30) * mm, "end": v(-10, 30) * mm});
            skPoint(sketch, "E1172.middle", {"position": v(0, 20) * mm});
            skLineSegment(sketch, "E1173", {"start": v(10, 30) * mm, "end": v(10, 29.84) * mm});
            skLineSegment(sketch, "E1174", {"start": v(10, 29.84) * mm, "end": v(10, 28.6) * mm});
            skLineSegment(sketch, "E1175", {"start": v(10, 28.6) * mm, "end": v(10, 27.38) * mm});
            skLineSegment(sketch, "E1176", {"start": v(10, 27.38) * mm, "end": v(10, 26.15) * mm});
            skLineSegment(sketch, "E1177", {"start": v(10, 26.15) * mm, "end": v(10, 24.92) * mm});
            skLineSegment(sketch, "E1178", {"start": v(10, 24.92) * mm, "end": v(10, 23.69) * mm});
            skLineSegment(sketch, "E1179", {"start": v(10, 23.69) * mm, "end": v(10, 22.46) * mm});
            skLineSegment(sketch, "E1180", {"start": v(10, 22.46) * mm, "end": v(10, 21.23) * mm});
            skLineSegment(sketch, "E1181", {"start": v(10, 21.23) * mm, "end": v(10, 20) * mm});
            skLineSegment(sketch, "E1182", {"start": v(10, 20) * mm, "end": v(10, 18.77) * mm});
            skLineSegment(sketch, "E1183", {"start": v(10, 18.77) * mm, "end": v(10, 17.54) * mm});
            skLineSegment(sketch, "E1184", {"start": v(10, 17.54) * mm, "end": v(10, 16.31) * mm});
            skLineSegment(sketch, "E1185", {"start": v(10, 16.31) * mm, "end": v(10, 15.08) * mm});
            skLineSegment(sketch, "E1186", {"start": v(10, 15.08) * mm, "end": v(10, 13.85) * mm});
            skLineSegment(sketch, "E1187", {"start": v(10, 13.85) * mm, "end": v(10, 12.62) * mm});
            skLineSegment(sketch, "E1188", {"start": v(10, 12.62) * mm, "end": v(10, 11.4) * mm});
            skLineSegment(sketch, "E1189", {"start": v(10, 11.4) * mm, "end": v(10, 10.16) * mm});
            skLineSegment(sketch, "E1190", {"start": v(10, 10.16) * mm, "end": v(10, 10) * mm});
            skLineSegment(sketch, "E1191", {"start": v(10, 29.84) * mm, "end": v(-10, 29.84) * mm});
            skLineSegment(sketch, "E1192", {"start": v(-10, 29.84) * mm, "end": v(-10, 30) * mm});
            skLineSegment(sketch, "E1193", {"start": v(10, 28.6) * mm, "end": v(-10, 28.6) * mm});
            skLineSegment(sketch, "E1194", {"start": v(-10, 28.61) * mm, "end": v(-10, 29.84) * mm});
            skLineSegment(sketch, "E1195", {"start": v(10, 27.38) * mm, "end": v(-10, 27.38) * mm});
            skLineSegment(sketch, "E1196", {"start": v(-10, 27.38) * mm, "end": v(-10, 28.61) * mm});
            skLineSegment(sketch, "E1197", {"start": v(10, 26.15) * mm, "end": v(-10, 26.15) * mm});
            skLineSegment(sketch, "E1198", {"start": v(-10, 26.15) * mm, "end": v(-10, 27.38) * mm});
            skLineSegment(sketch, "E1199", {"start": v(10, 24.92) * mm, "end": v(-10, 24.92) * mm});
            skLineSegment(sketch, "E1200", {"start": v(-10, 24.92) * mm, "end": v(-10, 26.15) * mm});
            skLineSegment(sketch, "E1201", {"start": v(10, 23.69) * mm, "end": v(-10, 23.69) * mm});
            skLineSegment(sketch, "E1202", {"start": v(-10, 23.69) * mm, "end": v(-10, 24.92) * mm});
            skLineSegment(sketch, "E1203", {"start": v(10, 22.46) * mm, "end": v(-10, 22.46) * mm});
            skLineSegment(sketch, "E1204", {"start": v(-10, 22.46) * mm, "end": v(-10, 23.69) * mm});
            skLineSegment(sketch, "E1205", {"start": v(10, 21.23) * mm, "end": v(-10, 21.23) * mm});
            skLineSegment(sketch, "E1206", {"start": v(-10, 21.23) * mm, "end": v(-10, 22.46) * mm});
            skLineSegment(sketch, "E1207", {"start": v(10, 20) * mm, "end": v(-10, 20) * mm});
            skLineSegment(sketch, "E1208", {"start": v(-10, 20) * mm, "end": v(-10, 21.23) * mm});
            skLineSegment(sketch, "E1209", {"start": v(10, 18.77) * mm, "end": v(-10, 18.77) * mm});
            skLineSegment(sketch, "E1210", {"start": v(-10, 18.77) * mm, "end": v(-10, 20) * mm});
            skLineSegment(sketch, "E1211", {"start": v(10, 17.54) * mm, "end": v(-10, 17.54) * mm});
            skLineSegment(sketch, "E1212", {"start": v(-10, 17.54) * mm, "end": v(-10, 18.77) * mm});
            skLineSegment(sketch, "E1213", {"start": v(10, 16.31) * mm, "end": v(-10, 16.31) * mm});
            skLineSegment(sketch, "E1214", {"start": v(-10, 16.31) * mm, "end": v(-10, 17.54) * mm});
            skLineSegment(sketch, "E1215", {"start": v(10, 15.08) * mm, "end": v(-10, 15.08) * mm});
            skLineSegment(sketch, "E1216", {"start": v(-10, 15.08) * mm, "end": v(-10, 16.31) * mm});
            skLineSegment(sketch, "E1217", {"start": v(10, 13.85) * mm, "end": v(-10, 13.85) * mm});
            skLineSegment(sketch, "E1218", {"start": v(-10, 13.85) * mm, "end": v(-10, 15.08) * mm});
            skLineSegment(sketch, "E1219", {"start": v(10, 12.62) * mm, "end": v(-10, 12.62) * mm});
            skLineSegment(sketch, "E1220", {"start": v(-10, 12.62) * mm, "end": v(-10, 13.85) * mm});
            skLineSegment(sketch, "E1221", {"start": v(10, 11.4) * mm, "end": v(-10, 11.39) * mm});
            skLineSegment(sketch, "E1222", {"start": v(-10, 11.39) * mm, "end": v(-10, 12.62) * mm});
            skLineSegment(sketch, "E1223", {"start": v(10, 10.16) * mm, "end": v(-10, 10.16) * mm});
            skLineSegment(sketch, "E1224", {"start": v(-10, 10.16) * mm, "end": v(-10, 11.39) * mm});
            skLineSegment(sketch, "E1225", {"start": v(-10, 10) * mm, "end": v(-10, 10.16) * mm});
            skLineSegment(sketch, "E1226", {"start": v(9.84, 30) * mm, "end": v(9.84, 29.84) * mm});
            skLineSegment(sketch, "E1227", {"start": v(9.84, 29.84) * mm, "end": v(9.84, 28.6) * mm});
            skLineSegment(sketch, "E1228", {"start": v(9.84, 28.6) * mm, "end": v(9.84, 27.38) * mm});
            skLineSegment(sketch, "E1229", {"start": v(9.84, 27.38) * mm, "end": v(9.84, 26.15) * mm});
            skLineSegment(sketch, "E1230", {"start": v(9.84, 26.15) * mm, "end": v(9.84, 24.92) * mm});
            skLineSegment(sketch, "E1231", {"start": v(9.84, 24.92) * mm, "end": v(9.84, 23.69) * mm});
            skLineSegment(sketch, "E1232", {"start": v(9.84, 23.69) * mm, "end": v(9.84, 22.46) * mm});
            skLineSegment(sketch, "E1233", {"start": v(9.84, 22.46) * mm, "end": v(9.84, 21.23) * mm});
            skLineSegment(sketch, "E1234", {"start": v(9.84, 21.23) * mm, "end": v(9.84, 5.5) * mm});
            skLineSegment(sketch, "E1235", {"start": v(9.84, 18.77) * mm, "end": v(9.84, 5.5) * mm});
            skLineSegment(sketch, "E1236", {"start": v(9.84, 18.77) * mm, "end": v(9.84, 17.54) * mm});
            skLineSegment(sketch, "E1237", {"start": v(9.84, 17.54) * mm, "end": v(9.84, 16.31) * mm});
            skLineSegment(sketch, "E1238", {"start": v(9.84, 16.31) * mm, "end": v(9.84, 15.08) * mm});
            skLineSegment(sketch, "E1239", {"start": v(9.84, 15.08) * mm, "end": v(9.84, 13.85) * mm});
            skLineSegment(sketch, "E1240", {"start": v(9.84, 13.85) * mm, "end": v(9.84, 12.62) * mm});
            skLineSegment(sketch, "E1241", {"start": v(9.84, 12.62) * mm, "end": v(9.84, 11.4) * mm});
            skLineSegment(sketch, "E1242", {"start": v(9.84, 11.4) * mm, "end": v(9.84, 10.16) * mm});
            skLineSegment(sketch, "E1243", {"start": v(9.84, 10.16) * mm, "end": v(9.84, 10) * mm});
            skLineSegment(sketch, "E1244", {"start": v(-9.84, 30) * mm, "end": v(-9.84, 29.84) * mm});
            skLineSegment(sketch, "E1245", {"start": v(-9.84, 29.84) * mm, "end": v(-9.84, 28.61) * mm});
            skLineSegment(sketch, "E1246", {"start": v(-9.84, 28.61) * mm, "end": v(-9.84, 27.38) * mm});
            skLineSegment(sketch, "E1247", {"start": v(-9.84, 27.38) * mm, "end": v(-9.84, 26.15) * mm});
            skLineSegment(sketch, "E1248", {"start": v(-9.84, 26.15) * mm, "end": v(-9.84, 24.92) * mm});
            skLineSegment(sketch, "E1249", {"start": v(-9.84, 24.92) * mm, "end": v(-9.84, 23.69) * mm});
            skLineSegment(sketch, "E1250", {"start": v(-9.84, 23.69) * mm, "end": v(-9.84, 22.46) * mm});
            skLineSegment(sketch, "E1251", {"start": v(-9.84, 22.46) * mm, "end": v(-9.84, 21.23) * mm});
            skLineSegment(sketch, "E1252", {"start": v(-9.84, 18.77) * mm, "end": v(-9.84, 17.54) * mm});
            skLineSegment(sketch, "E1253", {"start": v(-9.84, 17.54) * mm, "end": v(-9.84, 16.31) * mm});
            skLineSegment(sketch, "E1254", {"start": v(-9.84, 16.31) * mm, "end": v(-9.84, 15.08) * mm});
            skLineSegment(sketch, "E1255", {"start": v(-9.84, 15.08) * mm, "end": v(-9.84, 13.85) * mm});
            skLineSegment(sketch, "E1256", {"start": v(-9.84, 13.85) * mm, "end": v(-9.84, 12.62) * mm});
            skLineSegment(sketch, "E1257", {"start": v(-9.84, 12.62) * mm, "end": v(-9.84, 11.39) * mm});
            skLineSegment(sketch, "E1258", {"start": v(-9.84, 11.39) * mm, "end": v(-9.84, 10.16) * mm});
            skLineSegment(sketch, "E1259", {"start": v(-9.84, 10.16) * mm, "end": v(-9.84, 10) * mm});
            skLineSegment(sketch, "E1260", {"start": v(10, 30) * mm, "end": v(9.84, 30) * mm});
            skLineSegment(sketch, "E1261", {"start": v(-9.84, 30) * mm, "end": v(-10, 30) * mm});
            skLineSegment(sketch, "E1262", {"start": v(-9.84, 10) * mm, "end": v(-10, 10) * mm});
            skLineSegment(sketch, "E1263", {"start": v(9.84, 10) * mm, "end": v(10, 10) * mm});
            skLineSegment(sketch, "E1264", {"start": v(9.84, 30) * mm, "end": v(9.22, 30) * mm});
            skLineSegment(sketch, "E1265", {"start": v(9.22, 30) * mm, "end": v(9.22, 29.84) * mm});
            skLineSegment(sketch, "E1266", {"start": v(9.22, 29.84) * mm, "end": v(9.22, 28.61) * mm});
            skLineSegment(sketch, "E1267", {"start": v(9.22, 28.61) * mm, "end": v(9.22, 27.38) * mm});
            skLineSegment(sketch, "E1268", {"start": v(9.22, 27.38) * mm, "end": v(9.22, 26.15) * mm});
            skLineSegment(sketch, "E1269", {"start": v(9.22, 26.15) * mm, "end": v(9.22, 24.92) * mm});
            skLineSegment(sketch, "E1270", {"start": v(9.22, 24.92) * mm, "end": v(9.22, 23.69) * mm});
            skLineSegment(sketch, "E1271", {"start": v(9.22, 23.69) * mm, "end": v(9.22, 22.46) * mm});
            skLineSegment(sketch, "E1272", {"start": v(9.22, 22.46) * mm, "end": v(9.22, 21.23) * mm});
            skLineSegment(sketch, "E1273", {"start": v(9.22, 21.23) * mm, "end": v(9.22, 20) * mm});
            skLineSegment(sketch, "E1274", {"start": v(9.22, 20) * mm, "end": v(9.22, 18.77) * mm});
            skLineSegment(sketch, "E1275", {"start": v(9.22, 18.77) * mm, "end": v(9.22, 17.54) * mm});
            skLineSegment(sketch, "E1276", {"start": v(9.22, 17.54) * mm, "end": v(9.22, 16.31) * mm});
            skLineSegment(sketch, "E1277", {"start": v(9.22, 16.31) * mm, "end": v(9.22, 15.08) * mm});
            skLineSegment(sketch, "E1278", {"start": v(9.22, 15.08) * mm, "end": v(9.22, 13.85) * mm});
            skLineSegment(sketch, "E1279", {"start": v(9.22, 13.85) * mm, "end": v(9.22, 12.62) * mm});
            skLineSegment(sketch, "E1280", {"start": v(9.22, 12.62) * mm, "end": v(9.22, 11.4) * mm});
            skLineSegment(sketch, "E1281", {"start": v(9.22, 11.4) * mm, "end": v(9.22, 10.16) * mm});
            skLineSegment(sketch, "E1282", {"start": v(9.22, 10.16) * mm, "end": v(9.22, 10) * mm});
            skLineSegment(sketch, "E1283", {"start": v(9.22, 10) * mm, "end": v(9.84, 10) * mm});
            skLineSegment(sketch, "E1284", {"start": v(-9.84, 30) * mm, "end": v(-9.23, 30) * mm});
            skLineSegment(sketch, "E1285", {"start": v(-9.23, 30) * mm, "end": v(-9.23, 29.84) * mm});
            skLineSegment(sketch, "E1286", {"start": v(-9.23, 29.84) * mm, "end": v(-9.23, 28.61) * mm});
            skLineSegment(sketch, "E1287", {"start": v(-9.23, 28.61) * mm, "end": v(-9.23, 27.38) * mm});
            skLineSegment(sketch, "E1288", {"start": v(-9.23, 27.38) * mm, "end": v(-9.23, 26.15) * mm});
            skLineSegment(sketch, "E1289", {"start": v(-9.23, 26.15) * mm, "end": v(-9.23, 24.92) * mm});
            skLineSegment(sketch, "E1290", {"start": v(-9.23, 24.92) * mm, "end": v(-9.23, 23.69) * mm});
            skLineSegment(sketch, "E1291", {"start": v(-9.23, 23.69) * mm, "end": v(-9.23, 22.46) * mm});
            skLineSegment(sketch, "E1292", {"start": v(-9.23, 22.46) * mm, "end": v(-9.23, 21.23) * mm});
            skLineSegment(sketch, "E1293", {"start": v(-9.23, 21.23) * mm, "end": v(-9.23, 20) * mm});
            skLineSegment(sketch, "E1294", {"start": v(-9.23, 20) * mm, "end": v(-9.23, 18.77) * mm});
            skLineSegment(sketch, "E1295", {"start": v(-9.23, 18.77) * mm, "end": v(-9.23, 17.54) * mm});
            skLineSegment(sketch, "E1296", {"start": v(-9.23, 17.54) * mm, "end": v(-9.23, 16.31) * mm});
            skLineSegment(sketch, "E1297", {"start": v(-9.23, 16.31) * mm, "end": v(-9.23, 15.08) * mm});
            skLineSegment(sketch, "E1298", {"start": v(-9.23, 15.08) * mm, "end": v(-9.23, 13.85) * mm});
            skLineSegment(sketch, "E1299", {"start": v(-9.23, 13.85) * mm, "end": v(-9.23, 12.62) * mm});
            skLineSegment(sketch, "E1300", {"start": v(-9.23, 12.62) * mm, "end": v(-9.23, 11.39) * mm});
            skLineSegment(sketch, "E1301", {"start": v(-9.23, 11.39) * mm, "end": v(-9.23, 10.16) * mm});
            skLineSegment(sketch, "E1302", {"start": v(-9.23, 10.16) * mm, "end": v(-9.23, 10) * mm});
            skLineSegment(sketch, "E1303", {"start": v(-10, 10.16) * mm, "end": v(9.22, 10.16) * mm});
            skLineSegment(sketch, "E1304", {"start": v(-9.23, 10) * mm, "end": v(-9.84, 10) * mm});
            skLineSegment(sketch, "E1305", {"start": v(9.22, 11.4) * mm, "end": v(-9.23, 11.4) * mm});
            skLineSegment(sketch, "E1306", {"start": v(-9.23, 12.62) * mm, "end": v(9.22, 12.62) * mm});
            skLineSegment(sketch, "E1307", {"start": v(9.22, 13.85) * mm, "end": v(-9.23, 13.85) * mm});
            skLineSegment(sketch, "E1308", {"start": v(-9.23, 15.08) * mm, "end": v(9.22, 15.08) * mm});
            skLineSegment(sketch, "E1309", {"start": v(9.22, 16.31) * mm, "end": v(-9.23, 16.31) * mm});
            skLineSegment(sketch, "E1310", {"start": v(-9.23, 17.54) * mm, "end": v(9.22, 17.54) * mm});
            skLineSegment(sketch, "E1311", {"start": v(9.22, 18.77) * mm, "end": v(-9.23, 18.77) * mm});
            skLineSegment(sketch, "E1312", {"start": v(-9.23, 20) * mm, "end": v(9.22, 20) * mm});
            skLineSegment(sketch, "E1313", {"start": v(9.22, 21.23) * mm, "end": v(-9.23, 21.23) * mm});
            skLineSegment(sketch, "E1314", {"start": v(-9.23, 22.46) * mm, "end": v(9.22, 22.46) * mm});
            skLineSegment(sketch, "E1315", {"start": v(9.22, 23.69) * mm, "end": v(-9.23, 23.69) * mm});
            skLineSegment(sketch, "E1316", {"start": v(-9.23, 24.92) * mm, "end": v(9.22, 24.92) * mm});
            skLineSegment(sketch, "E1317", {"start": v(9.22, 26.15) * mm, "end": v(-9.23, 26.15) * mm});
            skLineSegment(sketch, "E1318", {"start": v(-9.23, 27.38) * mm, "end": v(9.22, 27.38) * mm});
            skLineSegment(sketch, "E1319", {"start": v(9.22, 28.6) * mm, "end": v(-9.23, 28.6) * mm});
            skArc(sketch, "E1320", {"start": v(9.22, 10.16) * mm, "mid": v(9.84, 10.78) * mm, "end": v(9.22, 11.4) * mm});
            skArc(sketch, "E1321", {"start": v(-9.23, 12.62) * mm, "mid": v(-9.84, 12) * mm, "end": v(-9.23, 11.4) * mm});
            skArc(sketch, "E1322", {"start": v(9.22, 12.62) * mm, "mid": v(9.84, 13.24) * mm, "end": v(9.22, 13.85) * mm});
            skArc(sketch, "E1323", {"start": v(-9.23, 15.08) * mm, "mid": v(-9.84, 14.47) * mm, "end": v(-9.23, 13.85) * mm});
            skArc(sketch, "E1324", {"start": v(9.22, 15.08) * mm, "mid": v(9.84, 15.7) * mm, "end": v(9.22, 16.31) * mm});
            skArc(sketch, "E1325", {"start": v(9.22, 17.54) * mm, "mid": v(9.84, 18.16) * mm, "end": v(9.22, 18.77) * mm});
            skArc(sketch, "E1326", {"start": v(-9.23, 17.54) * mm, "mid": v(-9.84, 16.93) * mm, "end": v(-9.23, 16.31) * mm});
            skArc(sketch, "E1327", {"start": v(9.22, 20) * mm, "mid": v(9.84, 20.62) * mm, "end": v(9.22, 21.23) * mm});
            skArc(sketch, "E1328", {"start": v(9.22, 22.46) * mm, "mid": v(9.84, 23.07) * mm, "end": v(9.22, 23.69) * mm});
            skArc(sketch, "E1329", {"start": v(9.22, 24.92) * mm, "mid": v(9.84, 25.53) * mm, "end": v(9.22, 26.15) * mm});
            skArc(sketch, "E1330", {"start": v(-9.23, 22.46) * mm, "mid": v(-9.84, 21.84) * mm, "end": v(-9.23, 21.23) * mm});
            skArc(sketch, "E1331", {"start": v(-9.23, 24.92) * mm, "mid": v(-9.84, 24.3) * mm, "end": v(-9.23, 23.69) * mm});
            skArc(sketch, "E1332", {"start": v(-9.23, 29.84) * mm, "mid": v(-9.84, 29.23) * mm, "end": v(-9.23, 28.61) * mm});
            skArc(sketch, "E1333", {"start": v(-9.23, 20) * mm, "mid": v(-9.84, 19.39) * mm, "end": v(-9.23, 18.77) * mm});
            skArc(sketch, "E1334", {"start": v(-9.23, 27.38) * mm, "mid": v(-9.84, 26.76) * mm, "end": v(-9.23, 26.15) * mm});
            skLineSegment(sketch, "E1335", {"start": v(-9.23, 29.84) * mm, "end": v(10, 29.84) * mm});
            skArc(sketch, "E1336", {"start": v(9.22, 27.38) * mm, "mid": v(9.84, 28) * mm, "end": v(9.22, 28.6) * mm});
            skLineSegment(sketch, "E1337.MirrorCS", {"start": v(10, 9.84) * mm, "end": v(10, 10) * mm});
            skLineSegment(sketch, "E1338.MirrorCS", {"start": v(-10, 10) * mm, "end": v(-10, 9.84) * mm});
            skLineSegment(sketch, "E1339.MirrorCS", {"start": v(9.84, 9.84) * mm, "end": v(9.84, 10) * mm});
            skLineSegment(sketch, "E1340.MirrorCS", {"start": v(-9.84, 9.84) * mm, "end": v(-9.84, 10) * mm});
            skLineSegment(sketch, "E1341.MirrorCS", {"start": v(-9.84, -10) * mm, "end": v(-9.22, -10) * mm});
            skLineSegment(sketch, "E1342.MirrorCS", {"start": v(-10, -9.84) * mm, "end": v(-10, -10) * mm});
            skLineSegment(sketch, "E1343.MirrorCS", {"start": v(9.84, -10) * mm, "end": v(9.84, -9.84) * mm});
            skLineSegment(sketch, "E1344.MirrorCS", {"start": v(-9.84, -10) * mm, "end": v(-9.84, -9.84) * mm});
            skLineSegment(sketch, "E1345.MirrorCS", {"start": v(10, -10) * mm, "end": v(9.84, -10) * mm});
            skLineSegment(sketch, "E1346.MirrorCS", {"start": v(-9.84, -10) * mm, "end": v(-10, -10) * mm});
            skLineSegment(sketch, "E1347.MirrorCS", {"start": v(10, -10) * mm, "end": v(10, -9.84) * mm});
            skLineSegment(sketch, "E1348.MirrorCS", {"start": v(-9.23, -10) * mm, "end": v(-9.23, -9.84) * mm});
            skLineSegment(sketch, "E1349.MirrorCS", {"start": v(9.22, 9.84) * mm, "end": v(9.22, 10) * mm});
            skLineSegment(sketch, "E1350.MirrorCS", {"start": v(9.84, -10) * mm, "end": v(9.22, -10) * mm});
            skLineSegment(sketch, "E1351.MirrorCS", {"start": v(-9.23, 9.84) * mm, "end": v(-9.23, 10) * mm});
            skLineSegment(sketch, "E1352.MirrorCS", {"start": v(9.22, -10) * mm, "end": v(9.22, -9.84) * mm});
            skLineSegment(sketch, "E1353.MirrorCS", {"start": v(9.84, 3.7) * mm, "end": v(9.84, 4.92) * mm});
            skLineSegment(sketch, "E1354.MirrorCS", {"start": v(-10, 8.61) * mm, "end": v(-10, 7.38) * mm});
            skLineSegment(sketch, "E1355.MirrorCS", {"start": v(-10, -1.23) * mm, "end": v(-10, -2.46) * mm});
            skLineSegment(sketch, "E1356.MirrorCS", {"start": v(-9.23, -4.92) * mm, "end": v(9.22, -4.92) * mm});
            skLineSegment(sketch, "E1357.MirrorCS", {"start": v(-9.23, 7.38) * mm, "end": v(-9.23, 8.61) * mm});
            skLineSegment(sketch, "E1358.MirrorCS", {"start": v(10, -9.84) * mm, "end": v(-10, -9.84) * mm});
            skLineSegment(sketch, "E1359.MirrorCS", {"start": v(-9.84, 2.46) * mm, "end": v(-9.84, 3.69) * mm});
            skLineSegment(sketch, "E1360.MirrorCS", {"start": v(10, 9.84) * mm, "end": v(-10, 9.84) * mm});
            skLineSegment(sketch, "E1361.MirrorCS", {"start": v(10, 0) * mm, "end": v(-10, 0) * mm});
            skLineSegment(sketch, "E1362.MirrorCS", {"start": v(9.22, -6.15) * mm, "end": v(-9.23, -6.15) * mm});
            skLineSegment(sketch, "E1363.MirrorCS", {"start": v(9.22, -6.15) * mm, "end": v(9.22, -4.92) * mm});
            skLineSegment(sketch, "E1364.MirrorCS", {"start": v(-10, 9.84) * mm, "end": v(-10, 8.61) * mm});
            skLineSegment(sketch, "E1365.MirrorCS", {"start": v(-10, 0) * mm, "end": v(-10, -1.23) * mm});
            skLineSegment(sketch, "E1366.MirrorCS", {"start": v(-9.23, -9.84) * mm, "end": v(-9.23, -8.6) * mm});
            skLineSegment(sketch, "E1367.MirrorCS", {"start": v(9.84, 6.15) * mm, "end": v(9.84, 7.38) * mm});
            skLineSegment(sketch, "E1368.MirrorCS", {"start": v(-9.23, -7.38) * mm, "end": v(9.22, -7.38) * mm});
            skLineSegment(sketch, "E1369.MirrorCS", {"start": v(10, 1.23) * mm, "end": v(-10, 1.23) * mm});
            skLineSegment(sketch, "E1370.MirrorCS", {"start": v(10, -8.6) * mm, "end": v(-10, -8.6) * mm});
            skLineSegment(sketch, "E1371.MirrorCS", {"start": v(9.22, -3.69) * mm, "end": v(9.22, -2.46) * mm});
            skLineSegment(sketch, "E1372.MirrorCS", {"start": v(-9.84, 4.92) * mm, "end": v(-9.84, 6.15) * mm});
            skLineSegment(sketch, "E1373.MirrorCS", {"start": v(-10, 1.23) * mm, "end": v(-10, 0) * mm});
            skLineSegment(sketch, "E1374.MirrorCS", {"start": v(-10, -8.6) * mm, "end": v(-10, -9.84) * mm});
            skLineSegment(sketch, "E1375.MirrorCS", {"start": v(-9.23, -7.38) * mm, "end": v(-9.23, -6.15) * mm});
            skLineSegment(sketch, "E1376.MirrorCS", {"start": v(9.84, 8.61) * mm, "end": v(9.84, 9.84) * mm});
            skLineSegment(sketch, "E1377.MirrorCS", {"start": v(10, 2.46) * mm, "end": v(-10, 2.46) * mm});
            skLineSegment(sketch, "E1378.MirrorCS", {"start": v(9.22, -1.23) * mm, "end": v(9.22, 0) * mm});
            skLineSegment(sketch, "E1379.MirrorCS", {"start": v(-9.84, 7.38) * mm, "end": v(-9.84, 8.61) * mm});
            skLineSegment(sketch, "E1380.MirrorCS", {"start": v(9.22, 8.61) * mm, "end": v(-9.23, 8.61) * mm});
            skLineSegment(sketch, "E1381.MirrorCS", {"start": v(9.84, -8.6) * mm, "end": v(9.84, -7.38) * mm});
            skLineSegment(sketch, "E1382.MirrorCS", {"start": v(-10, 2.46) * mm, "end": v(-10, 1.23) * mm});
            skLineSegment(sketch, "E1383.MirrorCS", {"start": v(-10, -7.38) * mm, "end": v(-10, -8.6) * mm});
            skLineSegment(sketch, "E1384.MirrorCS", {"start": v(-9.23, -4.92) * mm, "end": v(-9.23, -3.69) * mm});
            skLineSegment(sketch, "E1385.MirrorCS", {"start": v(-9.23, 7.38) * mm, "end": v(9.22, 7.38) * mm});
            skLineSegment(sketch, "E1386.MirrorCS", {"start": v(9.84, -6.15) * mm, "end": v(9.84, -4.92) * mm});
            skLineSegment(sketch, "E1387.MirrorCS", {"start": v(-10, 3.69) * mm, "end": v(-10, 2.46) * mm});
            skLineSegment(sketch, "E1388.MirrorCS", {"start": v(-10, -6.15) * mm, "end": v(-10, -7.38) * mm});
            skLineSegment(sketch, "E1389.MirrorCS", {"start": v(-9.23, 4.92) * mm, "end": v(9.22, 4.92) * mm});
            skLineSegment(sketch, "E1390.MirrorCS", {"start": v(-9.23, -2.46) * mm, "end": v(-9.23, -1.23) * mm});
            skLineSegment(sketch, "E1391.MirrorCS", {"start": v(10, 3.7) * mm, "end": v(-10, 3.69) * mm});
            skLineSegment(sketch, "E1392.MirrorCS", {"start": v(9.22, 1.23) * mm, "end": v(9.22, 2.46) * mm});
            skLineSegment(sketch, "E1393.MirrorCS", {"start": v(-9.84, -9.84) * mm, "end": v(-9.84, -8.6) * mm});
            skLineSegment(sketch, "E1394.MirrorCS", {"start": v(9.22, 6.15) * mm, "end": v(-9.23, 6.15) * mm});
            skLineSegment(sketch, "E1395.MirrorCS", {"start": v(-9.84, -7.38) * mm, "end": v(-9.84, -6.15) * mm});
            skLineSegment(sketch, "E1396.MirrorCS", {"start": v(9.22, 3.7) * mm, "end": v(9.22, 4.92) * mm});
            skLineSegment(sketch, "E1397.MirrorCS", {"start": v(9.84, -3.69) * mm, "end": v(9.84, -2.46) * mm});
            skLineSegment(sketch, "E1398.MirrorCS", {"start": v(-10, 4.92) * mm, "end": v(-10, 3.69) * mm});
            skLineSegment(sketch, "E1399.MirrorCS", {"start": v(-10, -4.92) * mm, "end": v(-10, -6.15) * mm});
            skLineSegment(sketch, "E1400.MirrorCS", {"start": v(-9.23, 0) * mm, "end": v(-9.23, 1.23) * mm});
            skLineSegment(sketch, "E1401.MirrorCS", {"start": v(-9.84, -4.92) * mm, "end": v(-9.84, -3.69) * mm});
            skLineSegment(sketch, "E1402.MirrorCS", {"start": v(10, -3.69) * mm, "end": v(-10, -3.69) * mm});
            skLineSegment(sketch, "E1403.MirrorCS", {"start": v(9.22, 6.15) * mm, "end": v(9.22, 7.38) * mm});
            skLineSegment(sketch, "E1404.MirrorCS", {"start": v(10, 3.7) * mm, "end": v(10, 4.92) * mm});
            skLineSegment(sketch, "E1405.MirrorCS", {"start": v(-9.23, 2.46) * mm, "end": v(-9.23, 3.69) * mm});
            skLineSegment(sketch, "E1406.MirrorCS", {"start": v(9.84, -1.23) * mm, "end": v(9.84, 14.5) * mm});
            skLineSegment(sketch, "E1407.MirrorCS", {"start": v(9.22, 8.61) * mm, "end": v(9.22, 9.84) * mm});
            skLineSegment(sketch, "E1408.MirrorCS", {"start": v(-9.84, -2.46) * mm, "end": v(-9.84, -1.23) * mm});
            skLineSegment(sketch, "E1409.MirrorCS", {"start": v(10, 6.15) * mm, "end": v(10, 7.38) * mm});
            skLineSegment(sketch, "E1410.MirrorCS", {"start": v(10, 0) * mm, "end": v(10, 1.23) * mm});
            skLineSegment(sketch, "E1411.MirrorCS", {"start": v(-10, 6.15) * mm, "end": v(-10, 4.92) * mm});
            skLineSegment(sketch, "E1412.MirrorCS", {"start": v(10, 1.23) * mm, "end": v(10, 2.46) * mm});
            skLineSegment(sketch, "E1413.MirrorCS", {"start": v(10, -2.46) * mm, "end": v(-10, -2.46) * mm});
            skLineSegment(sketch, "E1414.MirrorCS", {"start": v(10, 4.92) * mm, "end": v(10, 6.15) * mm});
            skLineSegment(sketch, "E1415.MirrorCS", {"start": v(-10, -3.69) * mm, "end": v(-10, -4.92) * mm});
            skLineSegment(sketch, "E1416.MirrorCS", {"start": v(9.22, -1.23) * mm, "end": v(-9.23, -1.23) * mm});
            skLineSegment(sketch, "E1417.MirrorCS", {"start": v(10, 2.46) * mm, "end": v(10, 3.7) * mm});
            skLineSegment(sketch, "E1418.MirrorCS", {"start": v(-9.23, 4.92) * mm, "end": v(-9.23, 6.15) * mm});
            skLineSegment(sketch, "E1419.MirrorCS", {"start": v(9.22, -8.6) * mm, "end": v(9.22, -7.38) * mm});
            skLineSegment(sketch, "E1420.MirrorCS", {"start": v(-9.84, 1.23) * mm, "end": v(-9.84, 2.46) * mm});
            skLineSegment(sketch, "E1421.MirrorCS", {"start": v(9.22, -7.38) * mm, "end": v(9.22, -6.15) * mm});
            skArc(sketch, "E1422.MirrorCS", {"start": v(-9.23, -9.84) * mm, "mid": v(-9.84, -9.22) * mm, "end": v(-9.23, -8.6) * mm});
            skLineSegment(sketch, "E1423.MirrorCS", {"start": v(9.84, 4.92) * mm, "end": v(9.84, 6.15) * mm});
            skLineSegment(sketch, "E1424.MirrorCS", {"start": v(-9.23, 8.61) * mm, "end": v(-9.23, 9.84) * mm});
            skArc(sketch, "E1425.MirrorCS", {"start": v(-9.23, 0) * mm, "mid": v(-9.84, 0.62) * mm, "end": v(-9.23, 1.23) * mm});
            skLineSegment(sketch, "E1426.MirrorCS", {"start": v(9.22, -4.92) * mm, "end": v(9.22, -3.69) * mm});
            skLineSegment(sketch, "E1427.MirrorCS", {"start": v(-9.84, 3.69) * mm, "end": v(-9.84, 4.92) * mm});
            skArc(sketch, "E1428.MirrorCS", {"start": v(-9.23, -7.38) * mm, "mid": v(-9.84, -6.76) * mm, "end": v(-9.23, -6.15) * mm});
            skLineSegment(sketch, "E1429.MirrorCS", {"start": v(-9.23, -8.6) * mm, "end": v(-9.23, -7.38) * mm});
            skLineSegment(sketch, "E1430.MirrorCS", {"start": v(9.84, 7.38) * mm, "end": v(9.84, 8.61) * mm});
            skLineSegment(sketch, "E1431.MirrorCS", {"start": v(-9.23, -9.84) * mm, "end": v(10, -9.84) * mm});
            skLineSegment(sketch, "E1432.MirrorCS", {"start": v(9.23, -8.6) * mm, "end": v(-9.23, -8.6) * mm});
            skLineSegment(sketch, "E1433.MirrorCS", {"start": v(-10, 9.84) * mm, "end": v(9.22, 9.84) * mm});
            skLineSegment(sketch, "E1434.MirrorCS", {"start": v(9.22, -2.46) * mm, "end": v(9.22, -1.23) * mm});
            skLineSegment(sketch, "E1435.MirrorCS", {"start": v(-9.84, 6.15) * mm, "end": v(-9.84, 7.38) * mm});
            skArc(sketch, "E1436.MirrorCS", {"start": v(9.22, -7.38) * mm, "mid": v(9.84, -8) * mm, "end": v(9.23, -8.6) * mm});
            skArc(sketch, "E1437.MirrorCS", {"start": v(9.22, 9.84) * mm, "mid": v(9.84, 9.23) * mm, "end": v(9.22, 8.61) * mm});
            skLineSegment(sketch, "E1438.MirrorCS", {"start": v(9.84, -9.84) * mm, "end": v(9.84, -8.6) * mm});
            skLineSegment(sketch, "E1439.MirrorCS", {"start": v(10, -7.38) * mm, "end": v(-10, -7.38) * mm});
            skLineSegment(sketch, "E1440.MirrorCS", {"start": v(-9.23, -6.15) * mm, "end": v(-9.23, -4.92) * mm});
            skArc(sketch, "E1441.MirrorCS", {"start": v(-9.23, 7.38) * mm, "mid": v(-9.84, 8) * mm, "end": v(-9.23, 8.61) * mm});
            skLineSegment(sketch, "E1442.MirrorCS", {"start": v(9.22, 0) * mm, "end": v(9.22, 1.23) * mm});
            skLineSegment(sketch, "E1443.MirrorCS", {"start": v(-9.84, 8.61) * mm, "end": v(-9.84, 9.84) * mm});
            skArc(sketch, "E1444.MirrorCS", {"start": v(9.22, 7.38) * mm, "mid": v(9.84, 6.77) * mm, "end": v(9.22, 6.15) * mm});
            skLineSegment(sketch, "E1445.MirrorCS", {"start": v(-9.84, -8.6) * mm, "end": v(-9.84, -7.38) * mm});
            skLineSegment(sketch, "E1446.MirrorCS", {"start": v(9.22, 2.46) * mm, "end": v(9.22, 3.7) * mm});
            skArc(sketch, "E1447.MirrorCS", {"start": v(9.22, 4.92) * mm, "mid": v(9.84, 4.3) * mm, "end": v(9.22, 3.7) * mm});
            skLineSegment(sketch, "E1448.MirrorCS", {"start": v(9.84, -7.38) * mm, "end": v(9.84, -6.15) * mm});
            skLineSegment(sketch, "E1449.MirrorCS", {"start": v(10, -6.15) * mm, "end": v(-10, -6.15) * mm});
            skLineSegment(sketch, "E1450.MirrorCS", {"start": v(-9.23, -3.69) * mm, "end": v(-9.23, -2.46) * mm});
            skArc(sketch, "E1451.MirrorCS", {"start": v(-9.23, 4.92) * mm, "mid": v(-9.84, 5.54) * mm, "end": v(-9.23, 6.15) * mm});
            skLineSegment(sketch, "E1452.MirrorCS", {"start": v(9.84, -4.92) * mm, "end": v(9.84, -3.69) * mm});
            skLineSegment(sketch, "E1453.MirrorCS", {"start": v(10, 4.92) * mm, "end": v(-10, 4.92) * mm});
            skLineSegment(sketch, "E1454.MirrorCS", {"start": v(10, -4.92) * mm, "end": v(-10, -4.92) * mm});
            skLineSegment(sketch, "E1455.MirrorCS", {"start": v(9.22, 3.7) * mm, "end": v(-9.23, 3.69) * mm});
            skLineSegment(sketch, "E1456.MirrorCS", {"start": v(-9.23, -1.23) * mm, "end": v(-9.23, 0) * mm});
            skArc(sketch, "E1457.MirrorCS", {"start": v(9.22, 2.46) * mm, "mid": v(9.84, 1.85) * mm, "end": v(9.22, 1.23) * mm});
            skLineSegment(sketch, "E1458.MirrorCS", {"start": v(-9.84, -6.15) * mm, "end": v(-9.84, -4.92) * mm});
            skLineSegment(sketch, "E1459.MirrorCS", {"start": v(-9.23, 2.46) * mm, "end": v(9.22, 2.46) * mm});
            skLineSegment(sketch, "E1460.MirrorCS", {"start": v(9.22, 4.92) * mm, "end": v(9.22, 6.15) * mm});
            skArc(sketch, "E1461.MirrorCS", {"start": v(-9.23, 2.46) * mm, "mid": v(-9.84, 3.07) * mm, "end": v(-9.23, 3.69) * mm});
            skLineSegment(sketch, "E1462.MirrorCS", {"start": v(9.84, -2.46) * mm, "end": v(9.84, -1.23) * mm});
            skLineSegment(sketch, "E1463.MirrorCS", {"start": v(10, 6.15) * mm, "end": v(-10, 6.15) * mm});
            skLineSegment(sketch, "E1464.MirrorCS", {"start": v(9.22, 1.23) * mm, "end": v(-9.23, 1.23) * mm});
            skLineSegment(sketch, "E1465.MirrorCS", {"start": v(-9.23, 1.23) * mm, "end": v(-9.23, 2.46) * mm});
            skArc(sketch, "E1466.MirrorCS", {"start": v(9.22, 0) * mm, "mid": v(9.84, -0.61) * mm, "end": v(9.22, -1.23) * mm});
            skLineSegment(sketch, "E1467.MirrorCS", {"start": v(-9.23, 0) * mm, "end": v(9.22, 0) * mm});
            skLineSegment(sketch, "E1468.MirrorCS", {"start": v(9.22, 7.38) * mm, "end": v(9.22, 8.61) * mm});
            skArc(sketch, "E1469.MirrorCS", {"start": v(9.22, -2.46) * mm, "mid": v(9.84, -3.07) * mm, "end": v(9.22, -3.69) * mm});
            skLineSegment(sketch, "E1470.MirrorCS", {"start": v(10, 7.38) * mm, "end": v(10, 8.61) * mm});
            skLineSegment(sketch, "E1471.MirrorCS", {"start": v(10, 8.61) * mm, "end": v(10, 9.84) * mm});
            skLineSegment(sketch, "E1472.MirrorCS", {"start": v(-9.23, -2.46) * mm, "end": v(9.22, -2.46) * mm});
            skLineSegment(sketch, "E1473.MirrorCS", {"start": v(10, -2.46) * mm, "end": v(10, -1.23) * mm});
            skLineSegment(sketch, "E1474.MirrorCS", {"start": v(-10, -2.46) * mm, "end": v(-10, -3.69) * mm});
            skLineSegment(sketch, "E1475.MirrorCS", {"start": v(10, 8.61) * mm, "end": v(-10, 8.61) * mm});
            skLineSegment(sketch, "E1476.MirrorCS", {"start": v(-9.23, 6.15) * mm, "end": v(-9.23, 7.38) * mm});
            skLineSegment(sketch, "E1477.MirrorCS", {"start": v(10, -4.92) * mm, "end": v(10, -3.69) * mm});
            skLineSegment(sketch, "E1478.MirrorCS", {"start": v(10, -3.69) * mm, "end": v(10, -2.46) * mm});
            skLineSegment(sketch, "E1479.MirrorCS", {"start": v(10, -6.15) * mm, "end": v(10, -4.92) * mm});
            skLineSegment(sketch, "E1480.MirrorCS", {"start": v(10, 10) * mm, "end": v(10, -10) * mm});
            skLineSegment(sketch, "E1481.MirrorCS", {"start": v(10, -7.38) * mm, "end": v(10, -6.15) * mm});
            skArc(sketch, "E1482.MirrorCS", {"start": v(-9.23, -2.46) * mm, "mid": v(-9.84, -1.84) * mm, "end": v(-9.23, -1.23) * mm});
            skLineSegment(sketch, "E1483.MirrorCS", {"start": v(-9.23, 3.69) * mm, "end": v(-9.23, 4.92) * mm});
            skLineSegment(sketch, "E1484.MirrorCS", {"start": v(10, -8.6) * mm, "end": v(10, -7.38) * mm});
            skLineSegment(sketch, "E1485.MirrorCS", {"start": v(10, -9.84) * mm, "end": v(10, -8.6) * mm});
            skLineSegment(sketch, "E1486.MirrorCS", {"start": v(-10, 10) * mm, "end": v(-10, -10) * mm});
            skPoint(sketch, "E1487.MirrorP", {"position": v(0, 0) * mm});
            skLineSegment(sketch, "E1488.MirrorCS", {"start": v(9.84, 2.46) * mm, "end": v(9.84, 3.7) * mm});
            skLineSegment(sketch, "E1489.MirrorCS", {"start": v(10, -1.23) * mm, "end": v(10, 0) * mm});
            skArc(sketch, "E1490.MirrorCS", {"start": v(9.22, -4.92) * mm, "mid": v(9.84, -5.53) * mm, "end": v(9.22, -6.15) * mm});
            skLineSegment(sketch, "E1491.MirrorCS", {"start": v(10, 7.38) * mm, "end": v(-10, 7.38) * mm});
            skLineSegment(sketch, "E1492.MirrorCS", {"start": v(-9.84, -3.69) * mm, "end": v(-9.84, -2.46) * mm});
            skLineSegment(sketch, "E1493.MirrorCS", {"start": v(10, -1.23) * mm, "end": v(-10, -1.23) * mm});
            skLineSegment(sketch, "E1494.MirrorCS", {"start": v(9.84, 1.23) * mm, "end": v(9.84, 14.5) * mm});
            skLineSegment(sketch, "E1495.MirrorCS", {"start": v(10, -10) * mm, "end": v(-10, -10) * mm});
            skLineSegment(sketch, "E1496.MirrorCS", {"start": v(-10, 7.38) * mm, "end": v(-10, 6.15) * mm});
            skArc(sketch, "E1497.MirrorCS", {"start": v(-9.23, -4.92) * mm, "mid": v(-9.84, -4.3) * mm, "end": v(-9.23, -3.69) * mm});
            skLineSegment(sketch, "E1498.MirrorCS", {"start": v(9.22, -9.84) * mm, "end": v(9.22, -8.6) * mm});
            skLineSegment(sketch, "E1499.MirrorCS", {"start": v(9.84, 1.23) * mm, "end": v(9.84, 2.46) * mm});
            skLineSegment(sketch, "E1500.MirrorCS", {"start": v(9.22, -3.69) * mm, "end": v(-9.23, -3.69) * mm});
            skSolve(sketch);
        }
        {
            var Q0;
            Q0=qCreatedBy(id+"F7.planeOp",FACE);
            var sketch = newSketch(context, id + "F24", { "sketchPlane" : qUnion([Q0])});
            skCircle(sketch, "E1501", {"center": v(-9.84, 2.25) * mm, "radius": 0.2 * mm});
            skSolve(sketch);
        }
        {
            var Q0;
            Q0=qCreatedBy(id+"F22.planeOp",FACE);
            cPlane(context, id + "F25", {"entities" : qUnion([Q0]), "cplaneType" : CPlaneType.OFFSET, "offset" : getVariable(context, 'd'), "width" : 150 * mm, "height" : 150 * mm});
        }
        {
            var Q0;
            Q0=qCreatedBy(id+"F25.planeOp",FACE);
            var sketch = newSketch(context, id + "F26", { "sketchPlane" : qUnion([Q0])});
            skLineSegment(sketch, "E1502.bottom", {"start": v(10, 10) * mm, "end": v(-10, 10) * mm});
            skLineSegment(sketch, "E1502.top", {"start": v(10, -10) * mm, "end": v(-10, -10) * mm});
            skLineSegment(sketch, "E1502.left", {"start": v(10, 10) * mm, "end": v(10, -10) * mm});
            skLineSegment(sketch, "E1502.right", {"start": v(-10, 10) * mm, "end": v(-10, -10) * mm});
            skPoint(sketch, "E1502.middle", {"position": v(0, 0) * mm});
            skLineSegment(sketch, "E1503", {"start": v(-10, 10) * mm, "end": v(-9.84, 10) * mm});
            skLineSegment(sketch, "E1504", {"start": v(-9.84, 10) * mm, "end": v(-8.61, 10) * mm});
            skLineSegment(sketch, "E1505", {"start": v(-8.61, 10) * mm, "end": v(-7.38, 10) * mm});
            skLineSegment(sketch, "E1506", {"start": v(-7.38, 10) * mm, "end": v(-6.15, 10) * mm});
            skLineSegment(sketch, "E1507", {"start": v(-6.15, 10) * mm, "end": v(-4.92, 10) * mm});
            skLineSegment(sketch, "E1508", {"start": v(-4.92, 10) * mm, "end": v(-3.7, 10) * mm});
            skLineSegment(sketch, "E1509", {"start": v(-3.7, 10) * mm, "end": v(-2.46, 10) * mm});
            skLineSegment(sketch, "E1510", {"start": v(-2.46, 10) * mm, "end": v(-1.23, 10) * mm});
            skLineSegment(sketch, "E1511", {"start": v(-1.23, 10) * mm, "end": v(0, 10) * mm});
            skLineSegment(sketch, "E1512", {"start": v(0, 10) * mm, "end": v(1.23, 10) * mm});
            skLineSegment(sketch, "E1513", {"start": v(1.23, 10) * mm, "end": v(2.46, 10) * mm});
            skLineSegment(sketch, "E1514", {"start": v(2.46, 10) * mm, "end": v(3.69, 10) * mm});
            skLineSegment(sketch, "E1515", {"start": v(3.69, 10) * mm, "end": v(4.92, 10) * mm});
            skLineSegment(sketch, "E1516", {"start": v(4.92, 10) * mm, "end": v(6.15, 10) * mm});
            skLineSegment(sketch, "E1517", {"start": v(6.15, 10) * mm, "end": v(7.38, 10) * mm});
            skLineSegment(sketch, "E1518", {"start": v(7.38, 10) * mm, "end": v(8.6, 10) * mm});
            skLineSegment(sketch, "E1519", {"start": v(8.6, 10) * mm, "end": v(9.84, 10) * mm});
            skLineSegment(sketch, "E1520", {"start": v(9.84, 10) * mm, "end": v(10, 10) * mm});
            skLineSegment(sketch, "E1521", {"start": v(-9.84, 10) * mm, "end": v(-9.84, -10) * mm});
            skLineSegment(sketch, "E1522", {"start": v(-9.84, -10) * mm, "end": v(-10, -10) * mm});
            skLineSegment(sketch, "E1523", {"start": v(-8.61, 10) * mm, "end": v(-8.61, -10) * mm});
            skLineSegment(sketch, "E1524", {"start": v(-8.61, -10) * mm, "end": v(-9.84, -10) * mm});
            skLineSegment(sketch, "E1525", {"start": v(-7.38, 10) * mm, "end": v(-7.38, -10) * mm});
            skLineSegment(sketch, "E1526", {"start": v(-7.38, -10) * mm, "end": v(-8.61, -10) * mm});
            skLineSegment(sketch, "E1527", {"start": v(-6.15, 10) * mm, "end": v(-6.15, -10) * mm});
            skLineSegment(sketch, "E1528", {"start": v(-6.15, -10) * mm, "end": v(-7.38, -10) * mm});
            skLineSegment(sketch, "E1529", {"start": v(-4.92, 10) * mm, "end": v(-4.92, -10) * mm});
            skLineSegment(sketch, "E1530", {"start": v(-4.92, -10) * mm, "end": v(-6.15, -10) * mm});
            skLineSegment(sketch, "E1531", {"start": v(-3.7, 10) * mm, "end": v(-3.7, -10) * mm});
            skLineSegment(sketch, "E1532", {"start": v(-3.7, -10) * mm, "end": v(-4.92, -10) * mm});
            skLineSegment(sketch, "E1533", {"start": v(-2.46, 10) * mm, "end": v(-2.46, -10) * mm});
            skLineSegment(sketch, "E1534", {"start": v(-2.46, -10) * mm, "end": v(-3.7, -10) * mm});
            skLineSegment(sketch, "E1535", {"start": v(-1.23, 10) * mm, "end": v(-1.23, -10) * mm});
            skLineSegment(sketch, "E1536", {"start": v(-1.23, -10) * mm, "end": v(-2.46, -10) * mm});
            skLineSegment(sketch, "E1537", {"start": v(0, 10) * mm, "end": v(0, -10) * mm});
            skLineSegment(sketch, "E1538", {"start": v(0, -10) * mm, "end": v(-1.23, -10) * mm});
            skLineSegment(sketch, "E1539", {"start": v(1.23, 10) * mm, "end": v(1.23, -10) * mm});
            skLineSegment(sketch, "E1540", {"start": v(1.23, -10) * mm, "end": v(0, -10) * mm});
            skLineSegment(sketch, "E1541", {"start": v(2.46, 10) * mm, "end": v(2.46, -10) * mm});
            skLineSegment(sketch, "E1542", {"start": v(2.46, -10) * mm, "end": v(1.23, -10) * mm});
            skLineSegment(sketch, "E1543", {"start": v(3.69, 10) * mm, "end": v(3.69, -10) * mm});
            skLineSegment(sketch, "E1544", {"start": v(3.69, -10) * mm, "end": v(2.46, -10) * mm});
            skLineSegment(sketch, "E1545", {"start": v(4.92, 10) * mm, "end": v(4.92, -10) * mm});
            skLineSegment(sketch, "E1546", {"start": v(4.92, -10) * mm, "end": v(3.69, -10) * mm});
            skLineSegment(sketch, "E1547", {"start": v(6.15, 10) * mm, "end": v(6.15, -10) * mm});
            skLineSegment(sketch, "E1548", {"start": v(6.15, -10) * mm, "end": v(4.92, -10) * mm});
            skLineSegment(sketch, "E1549", {"start": v(7.38, 10) * mm, "end": v(7.38, -10) * mm});
            skLineSegment(sketch, "E1550", {"start": v(7.38, -10) * mm, "end": v(6.15, -10) * mm});
            skLineSegment(sketch, "E1551", {"start": v(8.6, 10) * mm, "end": v(8.6, -10) * mm});
            skLineSegment(sketch, "E1552", {"start": v(8.6, -10) * mm, "end": v(7.38, -10) * mm});
            skLineSegment(sketch, "E1553", {"start": v(9.84, 10) * mm, "end": v(9.84, -10) * mm});
            skLineSegment(sketch, "E1554", {"start": v(9.84, -10) * mm, "end": v(8.6, -10) * mm});
            skLineSegment(sketch, "E1555", {"start": v(10, -10) * mm, "end": v(9.84, -10) * mm});
            skLineSegment(sketch, "E1556", {"start": v(-10, 9.84) * mm, "end": v(-9.84, 9.84) * mm});
            skLineSegment(sketch, "E1557", {"start": v(-9.84, 9.84) * mm, "end": v(-8.61, 9.84) * mm});
            skLineSegment(sketch, "E1558", {"start": v(-8.61, 9.84) * mm, "end": v(-7.38, 9.84) * mm});
            skLineSegment(sketch, "E1559", {"start": v(-7.38, 9.84) * mm, "end": v(-6.15, 9.84) * mm});
            skLineSegment(sketch, "E1560", {"start": v(-6.15, 9.84) * mm, "end": v(-4.92, 9.84) * mm});
            skLineSegment(sketch, "E1561", {"start": v(-4.92, 9.84) * mm, "end": v(-3.7, 9.84) * mm});
            skLineSegment(sketch, "E1562", {"start": v(-3.7, 9.84) * mm, "end": v(-2.46, 9.84) * mm});
            skLineSegment(sketch, "E1563", {"start": v(-2.46, 9.84) * mm, "end": v(-1.23, 9.84) * mm});
            skLineSegment(sketch, "E1564", {"start": v(-1.23, 9.84) * mm, "end": v(0, 9.84) * mm});
            skLineSegment(sketch, "E1565", {"start": v(0, 9.84) * mm, "end": v(1.23, 9.84) * mm});
            skLineSegment(sketch, "E1566", {"start": v(1.23, 9.84) * mm, "end": v(2.46, 9.84) * mm});
            skLineSegment(sketch, "E1567", {"start": v(2.46, 9.84) * mm, "end": v(3.69, 9.84) * mm});
            skLineSegment(sketch, "E1568", {"start": v(3.69, 9.84) * mm, "end": v(4.92, 9.84) * mm});
            skLineSegment(sketch, "E1569", {"start": v(4.92, 9.84) * mm, "end": v(6.15, 9.84) * mm});
            skLineSegment(sketch, "E1570", {"start": v(6.15, 9.84) * mm, "end": v(7.38, 9.84) * mm});
            skLineSegment(sketch, "E1571", {"start": v(7.38, 9.84) * mm, "end": v(8.6, 9.84) * mm});
            skLineSegment(sketch, "E1572", {"start": v(8.6, 9.84) * mm, "end": v(9.84, 9.84) * mm});
            skLineSegment(sketch, "E1573", {"start": v(9.84, 9.84) * mm, "end": v(10, 9.84) * mm});
            skLineSegment(sketch, "E1574", {"start": v(-10, -9.84) * mm, "end": v(-9.84, -9.84) * mm});
            skLineSegment(sketch, "E1575", {"start": v(-9.84, -9.84) * mm, "end": v(-8.61, -9.84) * mm});
            skLineSegment(sketch, "E1576", {"start": v(-8.61, -9.84) * mm, "end": v(-7.38, -9.84) * mm});
            skLineSegment(sketch, "E1577", {"start": v(-7.38, -9.84) * mm, "end": v(-6.15, -9.84) * mm});
            skLineSegment(sketch, "E1578", {"start": v(-6.15, -9.84) * mm, "end": v(-4.92, -9.84) * mm});
            skLineSegment(sketch, "E1579", {"start": v(-4.92, -9.84) * mm, "end": v(-3.7, -9.84) * mm});
            skLineSegment(sketch, "E1580", {"start": v(-3.7, -9.84) * mm, "end": v(-2.46, -9.84) * mm});
            skLineSegment(sketch, "E1581", {"start": v(-2.46, -9.84) * mm, "end": v(-1.23, -9.84) * mm});
            skLineSegment(sketch, "E1582", {"start": v(-1.23, -9.84) * mm, "end": v(0, -9.84) * mm});
            skLineSegment(sketch, "E1583", {"start": v(0, -9.84) * mm, "end": v(1.23, -9.84) * mm});
            skLineSegment(sketch, "E1584", {"start": v(1.23, -9.84) * mm, "end": v(2.46, -9.84) * mm});
            skLineSegment(sketch, "E1585", {"start": v(2.46, -9.84) * mm, "end": v(3.69, -9.84) * mm});
            skLineSegment(sketch, "E1586", {"start": v(3.69, -9.84) * mm, "end": v(4.92, -9.84) * mm});
            skLineSegment(sketch, "E1587", {"start": v(4.92, -9.84) * mm, "end": v(6.15, -9.84) * mm});
            skLineSegment(sketch, "E1588", {"start": v(6.15, -9.84) * mm, "end": v(7.38, -9.84) * mm});
            skLineSegment(sketch, "E1589", {"start": v(7.38, -9.84) * mm, "end": v(8.6, -9.84) * mm});
            skLineSegment(sketch, "E1590", {"start": v(8.6, -9.84) * mm, "end": v(9.84, -9.84) * mm});
            skLineSegment(sketch, "E1591", {"start": v(9.84, -9.84) * mm, "end": v(10, -9.84) * mm});
            skLineSegment(sketch, "E1592", {"start": v(-10, 10) * mm, "end": v(-10, 9.84) * mm});
            skLineSegment(sketch, "E1593", {"start": v(-10, -9.84) * mm, "end": v(-10, -10) * mm});
            skLineSegment(sketch, "E1594", {"start": v(10, -9.84) * mm, "end": v(10, -10) * mm});
            skLineSegment(sketch, "E1595", {"start": v(10, 9.84) * mm, "end": v(10, 10) * mm});
            skLineSegment(sketch, "E1596", {"start": v(-10, 9.84) * mm, "end": v(-10, 9.23) * mm});
            skLineSegment(sketch, "E1597", {"start": v(-10, 9.23) * mm, "end": v(-9.84, 9.23) * mm});
            skLineSegment(sketch, "E1598", {"start": v(-9.84, 9.23) * mm, "end": v(-8.61, 9.23) * mm});
            skLineSegment(sketch, "E1599", {"start": v(-8.61, 9.23) * mm, "end": v(-7.38, 9.23) * mm});
            skLineSegment(sketch, "E1600", {"start": v(-7.38, 9.23) * mm, "end": v(-6.15, 9.23) * mm});
            skLineSegment(sketch, "E1601", {"start": v(-6.15, 9.23) * mm, "end": v(-4.92, 9.23) * mm});
            skLineSegment(sketch, "E1602", {"start": v(-4.92, 9.23) * mm, "end": v(-3.7, 9.23) * mm});
            skLineSegment(sketch, "E1603", {"start": v(-3.7, 9.23) * mm, "end": v(-2.46, 9.23) * mm});
            skLineSegment(sketch, "E1604", {"start": v(-2.46, 9.23) * mm, "end": v(-1.23, 9.23) * mm});
            skLineSegment(sketch, "E1605", {"start": v(-1.23, 9.23) * mm, "end": v(0, 9.23) * mm});
            skLineSegment(sketch, "E1606", {"start": v(0, 9.23) * mm, "end": v(1.23, 9.23) * mm});
            skLineSegment(sketch, "E1607", {"start": v(1.23, 9.23) * mm, "end": v(2.46, 9.23) * mm});
            skLineSegment(sketch, "E1608", {"start": v(2.46, 9.23) * mm, "end": v(3.69, 9.23) * mm});
            skLineSegment(sketch, "E1609", {"start": v(3.69, 9.23) * mm, "end": v(4.92, 9.23) * mm});
            skLineSegment(sketch, "E1610", {"start": v(4.92, 9.23) * mm, "end": v(6.15, 9.23) * mm});
            skLineSegment(sketch, "E1611", {"start": v(6.15, 9.23) * mm, "end": v(7.38, 9.23) * mm});
            skLineSegment(sketch, "E1612", {"start": v(7.38, 9.23) * mm, "end": v(8.6, 9.23) * mm});
            skLineSegment(sketch, "E1613", {"start": v(8.6, 9.23) * mm, "end": v(9.84, 9.23) * mm});
            skLineSegment(sketch, "E1614", {"start": v(9.84, 9.23) * mm, "end": v(10, 9.23) * mm});
            skLineSegment(sketch, "E1615", {"start": v(10, 9.23) * mm, "end": v(10, 9.84) * mm});
            skLineSegment(sketch, "E1616", {"start": v(-10, -9.84) * mm, "end": v(-10, -9.22) * mm});
            skLineSegment(sketch, "E1617", {"start": v(-10, -9.22) * mm, "end": v(-9.84, -9.22) * mm});
            skLineSegment(sketch, "E1618", {"start": v(-9.84, -9.22) * mm, "end": v(-8.61, -9.22) * mm});
            skLineSegment(sketch, "E1619", {"start": v(-8.61, -9.22) * mm, "end": v(-7.38, -9.22) * mm});
            skLineSegment(sketch, "E1620", {"start": v(-7.38, -9.22) * mm, "end": v(-6.15, -9.22) * mm});
            skLineSegment(sketch, "E1621", {"start": v(-6.15, -9.22) * mm, "end": v(-4.92, -9.22) * mm});
            skLineSegment(sketch, "E1622", {"start": v(-4.92, -9.22) * mm, "end": v(-3.7, -9.22) * mm});
            skLineSegment(sketch, "E1623", {"start": v(-3.7, -9.22) * mm, "end": v(-2.46, -9.22) * mm});
            skLineSegment(sketch, "E1624", {"start": v(-2.46, -9.22) * mm, "end": v(-1.23, -9.22) * mm});
            skLineSegment(sketch, "E1625", {"start": v(-1.23, -9.22) * mm, "end": v(0, -9.22) * mm});
            skLineSegment(sketch, "E1626", {"start": v(0, -9.22) * mm, "end": v(1.23, -9.22) * mm});
            skLineSegment(sketch, "E1627", {"start": v(1.23, -9.22) * mm, "end": v(2.46, -9.22) * mm});
            skLineSegment(sketch, "E1628", {"start": v(2.46, -9.22) * mm, "end": v(3.69, -9.22) * mm});
            skLineSegment(sketch, "E1629", {"start": v(3.69, -9.22) * mm, "end": v(4.92, -9.22) * mm});
            skLineSegment(sketch, "E1630", {"start": v(4.92, -9.22) * mm, "end": v(6.15, -9.22) * mm});
            skLineSegment(sketch, "E1631", {"start": v(6.15, -9.22) * mm, "end": v(7.38, -9.22) * mm});
            skLineSegment(sketch, "E1632", {"start": v(7.38, -9.22) * mm, "end": v(8.6, -9.22) * mm});
            skLineSegment(sketch, "E1633", {"start": v(8.6, -9.22) * mm, "end": v(9.84, -9.22) * mm});
            skLineSegment(sketch, "E1634", {"start": v(9.84, -9.22) * mm, "end": v(10, -9.22) * mm});
            skLineSegment(sketch, "E1635", {"start": v(9.84, -10) * mm, "end": v(9.84, 9.23) * mm});
            skLineSegment(sketch, "E1636", {"start": v(10, -9.22) * mm, "end": v(10, -9.84) * mm});
            skLineSegment(sketch, "E1637", {"start": v(8.6, 9.23) * mm, "end": v(8.6, -9.22) * mm});
            skLineSegment(sketch, "E1638", {"start": v(7.38, -9.22) * mm, "end": v(7.38, 9.23) * mm});
            skLineSegment(sketch, "E1639", {"start": v(6.15, 9.23) * mm, "end": v(6.15, -9.22) * mm});
            skLineSegment(sketch, "E1640", {"start": v(4.92, -9.22) * mm, "end": v(4.92, 9.23) * mm});
            skLineSegment(sketch, "E1641", {"start": v(3.69, 9.23) * mm, "end": v(3.69, -9.22) * mm});
            skLineSegment(sketch, "E1642", {"start": v(2.46, -9.22) * mm, "end": v(2.46, 9.23) * mm});
            skLineSegment(sketch, "E1643", {"start": v(1.23, 9.23) * mm, "end": v(1.23, -9.22) * mm});
            skLineSegment(sketch, "E1644", {"start": v(0, -9.22) * mm, "end": v(0, 9.23) * mm});
            skLineSegment(sketch, "E1645", {"start": v(-1.23, 9.23) * mm, "end": v(-1.23, -9.22) * mm});
            skLineSegment(sketch, "E1646", {"start": v(-2.46, -9.22) * mm, "end": v(-2.46, 9.23) * mm});
            skLineSegment(sketch, "E1647", {"start": v(-3.7, 9.23) * mm, "end": v(-3.7, -9.22) * mm});
            skLineSegment(sketch, "E1648", {"start": v(-4.92, -9.22) * mm, "end": v(-4.92, 9.23) * mm});
            skLineSegment(sketch, "E1649", {"start": v(-6.15, 9.23) * mm, "end": v(-6.15, -9.22) * mm});
            skLineSegment(sketch, "E1650", {"start": v(-7.38, -9.22) * mm, "end": v(-7.38, 9.23) * mm});
            skLineSegment(sketch, "E1651", {"start": v(-8.61, 9.23) * mm, "end": v(-8.61, -9.22) * mm});
            skArc(sketch, "E1652", {"start": v(9.84, 9.23) * mm, "mid": v(9.22, 9.84) * mm, "end": v(8.6, 9.23) * mm});
            skArc(sketch, "E1653", {"start": v(7.38, -9.22) * mm, "mid": v(8, -9.84) * mm, "end": v(8.6, -9.22) * mm});
            skArc(sketch, "E1654", {"start": v(7.38, 9.23) * mm, "mid": v(6.76, 9.84) * mm, "end": v(6.15, 9.23) * mm});
            skArc(sketch, "E1655", {"start": v(4.92, -9.22) * mm, "mid": v(5.53, -9.84) * mm, "end": v(6.15, -9.22) * mm});
            skArc(sketch, "E1656", {"start": v(4.92, 9.23) * mm, "mid": v(4.3, 9.84) * mm, "end": v(3.69, 9.23) * mm});
            skArc(sketch, "E1657", {"start": v(2.46, 9.23) * mm, "mid": v(1.84, 9.84) * mm, "end": v(1.23, 9.23) * mm});
            skArc(sketch, "E1658", {"start": v(2.46, -9.22) * mm, "mid": v(3.07, -9.84) * mm, "end": v(3.69, -9.22) * mm});
            skArc(sketch, "E1659", {"start": v(0, 9.23) * mm, "mid": v(-0.62, 9.84) * mm, "end": v(-1.23, 9.23) * mm});
            skArc(sketch, "E1660", {"start": v(-2.46, 9.23) * mm, "mid": v(-3.08, 9.84) * mm, "end": v(-3.7, 9.23) * mm});
            skArc(sketch, "E1661", {"start": v(-4.92, 9.23) * mm, "mid": v(-5.54, 9.84) * mm, "end": v(-6.15, 9.23) * mm});
            skArc(sketch, "E1662", {"start": v(-2.46, -9.22) * mm, "mid": v(-1.85, -9.84) * mm, "end": v(-1.23, -9.22) * mm});
            skArc(sketch, "E1663", {"start": v(-4.92, -9.22) * mm, "mid": v(-4.3, -9.84) * mm, "end": v(-3.7, -9.22) * mm});
            skArc(sketch, "E1664", {"start": v(-9.84, -9.22) * mm, "mid": v(-9.23, -9.84) * mm, "end": v(-8.61, -9.22) * mm});
            skArc(sketch, "E1665", {"start": v(0, -9.22) * mm, "mid": v(0.61, -9.84) * mm, "end": v(1.23, -9.22) * mm});
            skArc(sketch, "E1666", {"start": v(-7.38, -9.22) * mm, "mid": v(-6.77, -9.84) * mm, "end": v(-6.15, -9.22) * mm});
            skLineSegment(sketch, "E1667", {"start": v(-9.84, -9.22) * mm, "end": v(-9.84, 10) * mm});
            skArc(sketch, "E1668", {"start": v(-7.38, 9.23) * mm, "mid": v(-8, 9.84) * mm, "end": v(-8.61, 9.23) * mm});
            skSolve(sketch);
        }
        {
            var Q0;
            Q0=qCreatedBy(id+"F3.planeOp",FACE);
            var sketch = newSketch(context, id + "F27", { "sketchPlane" : qUnion([Q0])});
            skCircle(sketch, "E1669", {"center": v(-9.84, 2.67) * mm, "radius": 0.2 * mm});
            skSolve(sketch);
        }
        {
            var Q0;
            Q0=makeQuery(id+"F27.imprint","IMPRINT",FACE,{"disambiguationData":[TD([[makeQuery(id+"F27.imprint","IMPRINT",EDGE,{"derivedFrom":sQuery(id+"F27.wireOp",EDGE,"E1669")}),1.0]])]});
            var Q1;
            Q1=sQuery(id+"F26.wireOp",EDGE,"E1635");
            var Q2;
            Q2=sQuery(id+"F26.wireOp",EDGE,"E1652");
            var Q3;
            Q3=sQuery(id+"F26.wireOp",EDGE,"E1637");
            var Q4;
            Q4=sQuery(id+"F26.wireOp",EDGE,"E1653");
            var Q5;
            Q5=sQuery(id+"F26.wireOp",EDGE,"E1638");
            var Q6;
            Q6=sQuery(id+"F26.wireOp",EDGE,"E1654");
            var Q7;
            Q7=sQuery(id+"F26.wireOp",EDGE,"E1639");
            var Q8;
            Q8=sQuery(id+"F26.wireOp",EDGE,"E1655");
            var Q9;
            Q9=sQuery(id+"F26.wireOp",EDGE,"E1640");
            var Q10;
            Q10=sQuery(id+"F26.wireOp",EDGE,"E1656");
            var Q11;
            Q11=sQuery(id+"F26.wireOp",EDGE,"E1641");
            var Q12;
            Q12=sQuery(id+"F26.wireOp",EDGE,"E1658");
            var Q13;
            Q13=sQuery(id+"F26.wireOp",EDGE,"E1642");
            var Q14;
            Q14=sQuery(id+"F26.wireOp",EDGE,"E1657");
            var Q15;
            Q15=sQuery(id+"F26.wireOp",EDGE,"E1643");
            var Q16;
            Q16=sQuery(id+"F26.wireOp",EDGE,"E1665");
            var Q17;
            Q17=sQuery(id+"F26.wireOp",EDGE,"E1644");
            var Q18;
            Q18=sQuery(id+"F26.wireOp",EDGE,"E1659");
            var Q19;
            Q19=sQuery(id+"F26.wireOp",EDGE,"E1645");
            var Q20;
            Q20=sQuery(id+"F26.wireOp",EDGE,"E1662");
            var Q21;
            Q21=sQuery(id+"F26.wireOp",EDGE,"E1646");
            var Q22;
            Q22=sQuery(id+"F26.wireOp",EDGE,"E1660");
            var Q23;
            Q23=sQuery(id+"F26.wireOp",EDGE,"E1647");
            var Q24;
            Q24=sQuery(id+"F26.wireOp",EDGE,"E1663");
            var Q25;
            Q25=sQuery(id+"F26.wireOp",EDGE,"E1648");
            var Q26;
            Q26=sQuery(id+"F26.wireOp",EDGE,"E1661");
            var Q27;
            Q27=sQuery(id+"F26.wireOp",EDGE,"E1649");
            var Q28;
            Q28=sQuery(id+"F26.wireOp",EDGE,"E1666");
            var Q29;
            Q29=sQuery(id+"F26.wireOp",EDGE,"E1650");
            var Q30;
            Q30=sQuery(id+"F26.wireOp",EDGE,"E1668");
            var Q31;
            Q31=sQuery(id+"F26.wireOp",EDGE,"E1651");
            var Q32;
            Q32=sQuery(id+"F26.wireOp",EDGE,"E1664");
            var Q33;
            Q33=sQuery(id+"F26.wireOp",EDGE,"E1667");
            sweep(context, id + "F28", {"profiles" : qUnion([Q0]), "path" : qUnion([Q1, Q2, Q3, Q4, Q5, Q6, Q7, Q8, Q9, Q10, Q11, Q12, Q13, Q14, Q15, Q16, Q17, Q18, Q19, Q20, Q21, Q22, Q23, Q24, Q25, Q26, Q27, Q28, Q29, Q30, Q31, Q32, Q33])});
        }
        {
            var Q0;
            Q0=qCreatedBy(id+"F25.planeOp",FACE);
            cPlane(context, id + "F29", {"entities" : qUnion([Q0]), "cplaneType" : CPlaneType.OFFSET, "offset" : getVariable(context, 'd'), "width" : 150 * mm, "height" : 150 * mm});
        }
        {
            var Q0;
            Q0=qCreatedBy(id+"F29.planeOp",FACE);
            var sketch = newSketch(context, id + "F30", { "sketchPlane" : qUnion([Q0])});
            skLineSegment(sketch, "E1670.bottom", {"start": v(10, 10) * mm, "end": v(10, 30) * mm});
            skLineSegment(sketch, "E1670.top", {"start": v(-10, 10) * mm, "end": v(-10, 30) * mm});
            skLineSegment(sketch, "E1670.left", {"start": v(10, 10) * mm, "end": v(-10, 10) * mm});
            skLineSegment(sketch, "E1670.right", {"start": v(10, 30) * mm, "end": v(-10, 30) * mm});
            skPoint(sketch, "E1670.middle", {"position": v(0, 20) * mm});
            skLineSegment(sketch, "E1671", {"start": v(10, 30) * mm, "end": v(10, 29.84) * mm});
            skLineSegment(sketch, "E1672", {"start": v(10, 29.84) * mm, "end": v(10, 28.61) * mm});
            skLineSegment(sketch, "E1673", {"start": v(10, 28.61) * mm, "end": v(10, 27.38) * mm});
            skLineSegment(sketch, "E1674", {"start": v(10, 27.38) * mm, "end": v(10, 26.15) * mm});
            skLineSegment(sketch, "E1675", {"start": v(10, 26.15) * mm, "end": v(10, 24.92) * mm});
            skLineSegment(sketch, "E1676", {"start": v(10, 24.92) * mm, "end": v(10, 23.7) * mm});
            skLineSegment(sketch, "E1677", {"start": v(10, 23.7) * mm, "end": v(10, 22.46) * mm});
            skLineSegment(sketch, "E1678", {"start": v(10, 22.46) * mm, "end": v(10, 21.23) * mm});
            skLineSegment(sketch, "E1679", {"start": v(10, 21.23) * mm, "end": v(10, 20) * mm});
            skLineSegment(sketch, "E1680", {"start": v(10, 20) * mm, "end": v(10, 18.77) * mm});
            skLineSegment(sketch, "E1681", {"start": v(10, 18.77) * mm, "end": v(10, 17.54) * mm});
            skLineSegment(sketch, "E1682", {"start": v(10, 17.54) * mm, "end": v(10, 16.31) * mm});
            skLineSegment(sketch, "E1683", {"start": v(10, 16.31) * mm, "end": v(10, 15.08) * mm});
            skLineSegment(sketch, "E1684", {"start": v(10, 15.08) * mm, "end": v(10, 13.85) * mm});
            skLineSegment(sketch, "E1685", {"start": v(10, 13.85) * mm, "end": v(10, 12.62) * mm});
            skLineSegment(sketch, "E1686", {"start": v(10, 12.62) * mm, "end": v(10, 11.4) * mm});
            skLineSegment(sketch, "E1687", {"start": v(10, 11.4) * mm, "end": v(10, 10.16) * mm});
            skLineSegment(sketch, "E1688", {"start": v(10, 10.16) * mm, "end": v(10, 10) * mm});
            skLineSegment(sketch, "E1689", {"start": v(10, 29.84) * mm, "end": v(-10, 29.84) * mm});
            skLineSegment(sketch, "E1690", {"start": v(-10, 29.84) * mm, "end": v(-10, 30) * mm});
            skLineSegment(sketch, "E1691", {"start": v(10, 28.61) * mm, "end": v(-10, 28.61) * mm});
            skLineSegment(sketch, "E1692", {"start": v(-10, 28.61) * mm, "end": v(-10, 29.84) * mm});
            skLineSegment(sketch, "E1693", {"start": v(10, 27.38) * mm, "end": v(-10, 27.38) * mm});
            skLineSegment(sketch, "E1694", {"start": v(-10, 27.38) * mm, "end": v(-10, 28.61) * mm});
            skLineSegment(sketch, "E1695", {"start": v(10, 26.15) * mm, "end": v(-10, 26.15) * mm});
            skLineSegment(sketch, "E1696", {"start": v(-10, 26.15) * mm, "end": v(-10, 27.38) * mm});
            skLineSegment(sketch, "E1697", {"start": v(10, 24.92) * mm, "end": v(-10, 24.92) * mm});
            skLineSegment(sketch, "E1698", {"start": v(-10, 24.92) * mm, "end": v(-10, 26.15) * mm});
            skLineSegment(sketch, "E1699", {"start": v(10, 23.7) * mm, "end": v(-10, 23.7) * mm});
            skLineSegment(sketch, "E1700", {"start": v(-10, 23.7) * mm, "end": v(-10, 24.92) * mm});
            skLineSegment(sketch, "E1701", {"start": v(10, 22.46) * mm, "end": v(-10, 22.46) * mm});
            skLineSegment(sketch, "E1702", {"start": v(-10, 22.46) * mm, "end": v(-10, 23.7) * mm});
            skLineSegment(sketch, "E1703", {"start": v(10, 21.23) * mm, "end": v(-10, 21.23) * mm});
            skLineSegment(sketch, "E1704", {"start": v(-10, 21.23) * mm, "end": v(-10, 22.46) * mm});
            skLineSegment(sketch, "E1705", {"start": v(10, 20) * mm, "end": v(-10, 20) * mm});
            skLineSegment(sketch, "E1706", {"start": v(-10, 20) * mm, "end": v(-10, 21.23) * mm});
            skLineSegment(sketch, "E1707", {"start": v(10, 18.77) * mm, "end": v(-10, 18.77) * mm});
            skLineSegment(sketch, "E1708", {"start": v(-10, 18.77) * mm, "end": v(-10, 20) * mm});
            skLineSegment(sketch, "E1709", {"start": v(10, 17.54) * mm, "end": v(-10, 17.54) * mm});
            skLineSegment(sketch, "E1710", {"start": v(-10, 17.54) * mm, "end": v(-10, 18.77) * mm});
            skLineSegment(sketch, "E1711", {"start": v(10, 16.31) * mm, "end": v(-10, 16.31) * mm});
            skLineSegment(sketch, "E1712", {"start": v(-10, 16.31) * mm, "end": v(-10, 17.54) * mm});
            skLineSegment(sketch, "E1713", {"start": v(10, 15.08) * mm, "end": v(-10, 15.08) * mm});
            skLineSegment(sketch, "E1714", {"start": v(-10, 15.08) * mm, "end": v(-10, 16.31) * mm});
            skLineSegment(sketch, "E1715", {"start": v(10, 13.85) * mm, "end": v(-10, 13.85) * mm});
            skLineSegment(sketch, "E1716", {"start": v(-10, 13.85) * mm, "end": v(-10, 15.08) * mm});
            skLineSegment(sketch, "E1717", {"start": v(10, 12.62) * mm, "end": v(-10, 12.62) * mm});
            skLineSegment(sketch, "E1718", {"start": v(-10, 12.62) * mm, "end": v(-10, 13.85) * mm});
            skLineSegment(sketch, "E1719", {"start": v(10, 11.4) * mm, "end": v(-10, 11.4) * mm});
            skLineSegment(sketch, "E1720", {"start": v(-10, 11.4) * mm, "end": v(-10, 12.62) * mm});
            skLineSegment(sketch, "E1721", {"start": v(10, 10.16) * mm, "end": v(-10, 10.16) * mm});
            skLineSegment(sketch, "E1722", {"start": v(-10, 10.16) * mm, "end": v(-10, 11.4) * mm});
            skLineSegment(sketch, "E1723", {"start": v(-10, 10) * mm, "end": v(-10, 10.16) * mm});
            skLineSegment(sketch, "E1724", {"start": v(9.84, 30) * mm, "end": v(9.84, 29.84) * mm});
            skLineSegment(sketch, "E1725", {"start": v(9.84, 29.84) * mm, "end": v(9.84, 28.61) * mm});
            skLineSegment(sketch, "E1726", {"start": v(9.84, 28.61) * mm, "end": v(9.84, 27.38) * mm});
            skLineSegment(sketch, "E1727", {"start": v(9.84, 27.38) * mm, "end": v(9.84, 26.15) * mm});
            skLineSegment(sketch, "E1728", {"start": v(9.84, 26.15) * mm, "end": v(9.84, 24.92) * mm});
            skLineSegment(sketch, "E1729", {"start": v(9.84, 24.92) * mm, "end": v(9.84, 23.7) * mm});
            skLineSegment(sketch, "E1730", {"start": v(9.84, 23.7) * mm, "end": v(9.84, 22.46) * mm});
            skLineSegment(sketch, "E1731", {"start": v(9.84, 22.46) * mm, "end": v(9.84, 21.23) * mm});
            skLineSegment(sketch, "E1732", {"start": v(9.84, 18.77) * mm, "end": v(9.84, 17.54) * mm});
            skLineSegment(sketch, "E1733", {"start": v(9.84, 17.54) * mm, "end": v(9.84, 16.31) * mm});
            skLineSegment(sketch, "E1734", {"start": v(9.84, 16.31) * mm, "end": v(9.84, 15.08) * mm});
            skLineSegment(sketch, "E1735", {"start": v(9.84, 15.08) * mm, "end": v(9.84, 13.85) * mm});
            skLineSegment(sketch, "E1736", {"start": v(9.84, 13.85) * mm, "end": v(9.84, 12.62) * mm});
            skLineSegment(sketch, "E1737", {"start": v(9.84, 12.62) * mm, "end": v(9.84, 11.4) * mm});
            skLineSegment(sketch, "E1738", {"start": v(9.84, 11.4) * mm, "end": v(9.84, 10.16) * mm});
            skLineSegment(sketch, "E1739", {"start": v(9.84, 10.16) * mm, "end": v(9.84, 10) * mm});
            skLineSegment(sketch, "E1740", {"start": v(-9.84, 30) * mm, "end": v(-9.84, 29.84) * mm});
            skLineSegment(sketch, "E1741", {"start": v(-9.84, 29.84) * mm, "end": v(-9.84, 28.61) * mm});
            skLineSegment(sketch, "E1742", {"start": v(-9.84, 28.61) * mm, "end": v(-9.84, 27.38) * mm});
            skLineSegment(sketch, "E1743", {"start": v(-9.84, 27.38) * mm, "end": v(-9.84, 26.15) * mm});
            skLineSegment(sketch, "E1744", {"start": v(-9.84, 26.15) * mm, "end": v(-9.84, 24.92) * mm});
            skLineSegment(sketch, "E1745", {"start": v(-9.84, 24.92) * mm, "end": v(-9.84, 23.7) * mm});
            skLineSegment(sketch, "E1746", {"start": v(-9.84, 23.7) * mm, "end": v(-9.84, 22.46) * mm});
            skLineSegment(sketch, "E1747", {"start": v(-9.84, 22.46) * mm, "end": v(-9.84, 21.23) * mm});
            skLineSegment(sketch, "E1748", {"start": v(-9.84, 18.77) * mm, "end": v(-9.84, 17.54) * mm});
            skLineSegment(sketch, "E1749", {"start": v(-9.84, 17.54) * mm, "end": v(-9.84, 16.31) * mm});
            skLineSegment(sketch, "E1750", {"start": v(-9.84, 16.31) * mm, "end": v(-9.84, 15.08) * mm});
            skLineSegment(sketch, "E1751", {"start": v(-9.84, 15.08) * mm, "end": v(-9.84, 13.85) * mm});
            skLineSegment(sketch, "E1752", {"start": v(-9.84, 13.85) * mm, "end": v(-9.84, 12.62) * mm});
            skLineSegment(sketch, "E1753", {"start": v(-9.84, 12.62) * mm, "end": v(-9.84, 11.4) * mm});
            skLineSegment(sketch, "E1754", {"start": v(-9.84, 11.4) * mm, "end": v(-9.84, 10.16) * mm});
            skLineSegment(sketch, "E1755", {"start": v(-9.84, 10.16) * mm, "end": v(-9.84, 10) * mm});
            skLineSegment(sketch, "E1756", {"start": v(10, 30) * mm, "end": v(9.84, 30) * mm});
            skLineSegment(sketch, "E1757", {"start": v(-9.84, 30) * mm, "end": v(-10, 30) * mm});
            skLineSegment(sketch, "E1758", {"start": v(-9.84, 10) * mm, "end": v(-10, 10) * mm});
            skLineSegment(sketch, "E1759", {"start": v(9.84, 10) * mm, "end": v(10, 10) * mm});
            skLineSegment(sketch, "E1760", {"start": v(9.84, 30) * mm, "end": v(9.22, 30) * mm});
            skLineSegment(sketch, "E1761", {"start": v(9.22, 30) * mm, "end": v(9.22, 29.84) * mm});
            skLineSegment(sketch, "E1762", {"start": v(9.22, 29.84) * mm, "end": v(9.22, 28.61) * mm});
            skLineSegment(sketch, "E1763", {"start": v(9.22, 28.61) * mm, "end": v(9.22, 27.38) * mm});
            skLineSegment(sketch, "E1764", {"start": v(9.22, 27.38) * mm, "end": v(9.22, 26.15) * mm});
            skLineSegment(sketch, "E1765", {"start": v(9.22, 26.15) * mm, "end": v(9.22, 24.92) * mm});
            skLineSegment(sketch, "E1766", {"start": v(9.22, 24.92) * mm, "end": v(9.22, 23.7) * mm});
            skLineSegment(sketch, "E1767", {"start": v(9.22, 23.7) * mm, "end": v(9.22, 22.46) * mm});
            skLineSegment(sketch, "E1768", {"start": v(9.22, 22.46) * mm, "end": v(9.22, 21.23) * mm});
            skLineSegment(sketch, "E1769", {"start": v(9.22, 21.23) * mm, "end": v(9.22, 20) * mm});
            skLineSegment(sketch, "E1770", {"start": v(9.22, 20) * mm, "end": v(9.22, 18.77) * mm});
            skLineSegment(sketch, "E1771", {"start": v(9.22, 18.77) * mm, "end": v(9.22, 17.54) * mm});
            skLineSegment(sketch, "E1772", {"start": v(9.22, 17.54) * mm, "end": v(9.22, 16.31) * mm});
            skLineSegment(sketch, "E1773", {"start": v(9.22, 16.31) * mm, "end": v(9.22, 15.08) * mm});
            skLineSegment(sketch, "E1774", {"start": v(9.22, 15.08) * mm, "end": v(9.22, 13.85) * mm});
            skLineSegment(sketch, "E1775", {"start": v(9.22, 13.85) * mm, "end": v(9.22, 12.62) * mm});
            skLineSegment(sketch, "E1776", {"start": v(9.22, 12.62) * mm, "end": v(9.22, 11.4) * mm});
            skLineSegment(sketch, "E1777", {"start": v(9.22, 11.4) * mm, "end": v(9.22, 10.16) * mm});
            skLineSegment(sketch, "E1778", {"start": v(9.22, 10.16) * mm, "end": v(9.22, 10) * mm});
            skLineSegment(sketch, "E1779", {"start": v(9.22, 10) * mm, "end": v(9.84, 10) * mm});
            skLineSegment(sketch, "E1780", {"start": v(-9.84, 30) * mm, "end": v(-9.23, 30) * mm});
            skLineSegment(sketch, "E1781", {"start": v(-9.23, 30) * mm, "end": v(-9.23, 29.84) * mm});
            skLineSegment(sketch, "E1782", {"start": v(-9.23, 29.84) * mm, "end": v(-9.23, 28.61) * mm});
            skLineSegment(sketch, "E1783", {"start": v(-9.23, 28.61) * mm, "end": v(-9.23, 27.38) * mm});
            skLineSegment(sketch, "E1784", {"start": v(-9.23, 27.38) * mm, "end": v(-9.23, 26.15) * mm});
            skLineSegment(sketch, "E1785", {"start": v(-9.23, 26.15) * mm, "end": v(-9.23, 24.92) * mm});
            skLineSegment(sketch, "E1786", {"start": v(-9.23, 24.92) * mm, "end": v(-9.23, 23.7) * mm});
            skLineSegment(sketch, "E1787", {"start": v(-9.23, 23.7) * mm, "end": v(-9.23, 22.46) * mm});
            skLineSegment(sketch, "E1788", {"start": v(-9.23, 22.46) * mm, "end": v(-9.23, 21.23) * mm});
            skLineSegment(sketch, "E1789", {"start": v(-9.23, 21.23) * mm, "end": v(-9.23, 20) * mm});
            skLineSegment(sketch, "E1790", {"start": v(-9.23, 20) * mm, "end": v(-9.23, 18.77) * mm});
            skLineSegment(sketch, "E1791", {"start": v(-9.23, 18.77) * mm, "end": v(-9.23, 17.54) * mm});
            skLineSegment(sketch, "E1792", {"start": v(-9.23, 17.54) * mm, "end": v(-9.23, 16.31) * mm});
            skLineSegment(sketch, "E1793", {"start": v(-9.23, 16.31) * mm, "end": v(-9.23, 15.08) * mm});
            skLineSegment(sketch, "E1794", {"start": v(-9.23, 15.08) * mm, "end": v(-9.23, 13.85) * mm});
            skLineSegment(sketch, "E1795", {"start": v(-9.23, 13.85) * mm, "end": v(-9.23, 12.62) * mm});
            skLineSegment(sketch, "E1796", {"start": v(-9.23, 12.62) * mm, "end": v(-9.23, 11.4) * mm});
            skLineSegment(sketch, "E1797", {"start": v(-9.23, 11.4) * mm, "end": v(-9.23, 10.16) * mm});
            skLineSegment(sketch, "E1798", {"start": v(-9.23, 10.16) * mm, "end": v(-9.23, 10) * mm});
            skLineSegment(sketch, "E1799", {"start": v(-10, 10.16) * mm, "end": v(9.22, 10.16) * mm});
            skLineSegment(sketch, "E1800", {"start": v(-9.23, 10) * mm, "end": v(-9.84, 10) * mm});
            skLineSegment(sketch, "E1801", {"start": v(9.22, 11.4) * mm, "end": v(-9.23, 11.4) * mm});
            skLineSegment(sketch, "E1802", {"start": v(-9.23, 12.62) * mm, "end": v(9.22, 12.62) * mm});
            skLineSegment(sketch, "E1803", {"start": v(9.22, 13.85) * mm, "end": v(-9.23, 13.85) * mm});
            skLineSegment(sketch, "E1804", {"start": v(-9.23, 15.08) * mm, "end": v(9.22, 15.08) * mm});
            skLineSegment(sketch, "E1805", {"start": v(9.22, 16.31) * mm, "end": v(-9.23, 16.31) * mm});
            skLineSegment(sketch, "E1806", {"start": v(-9.23, 17.54) * mm, "end": v(9.22, 17.54) * mm});
            skLineSegment(sketch, "E1807", {"start": v(9.22, 18.77) * mm, "end": v(-9.23, 18.77) * mm});
            skLineSegment(sketch, "E1808", {"start": v(-9.23, 20) * mm, "end": v(9.22, 20) * mm});
            skLineSegment(sketch, "E1809", {"start": v(9.22, 21.23) * mm, "end": v(-9.23, 21.23) * mm});
            skLineSegment(sketch, "E1810", {"start": v(-9.23, 22.46) * mm, "end": v(9.22, 22.46) * mm});
            skLineSegment(sketch, "E1811", {"start": v(9.22, 23.7) * mm, "end": v(-9.23, 23.7) * mm});
            skLineSegment(sketch, "E1812", {"start": v(-9.23, 24.92) * mm, "end": v(9.22, 24.92) * mm});
            skLineSegment(sketch, "E1813", {"start": v(9.22, 26.15) * mm, "end": v(-9.23, 26.15) * mm});
            skLineSegment(sketch, "E1814", {"start": v(-9.23, 27.38) * mm, "end": v(9.22, 27.38) * mm});
            skLineSegment(sketch, "E1815", {"start": v(9.22, 28.61) * mm, "end": v(-9.23, 28.61) * mm});
            skArc(sketch, "E1816", {"start": v(9.22, 10.16) * mm, "mid": v(9.84, 10.78) * mm, "end": v(9.22, 11.4) * mm});
            skArc(sketch, "E1817", {"start": v(-9.23, 12.62) * mm, "mid": v(-9.84, 12) * mm, "end": v(-9.23, 11.4) * mm});
            skArc(sketch, "E1818", {"start": v(9.22, 12.62) * mm, "mid": v(9.84, 13.24) * mm, "end": v(9.22, 13.85) * mm});
            skArc(sketch, "E1819", {"start": v(-9.23, 15.08) * mm, "mid": v(-9.84, 14.47) * mm, "end": v(-9.23, 13.85) * mm});
            skArc(sketch, "E1820", {"start": v(9.22, 15.08) * mm, "mid": v(9.84, 15.7) * mm, "end": v(9.22, 16.31) * mm});
            skArc(sketch, "E1821", {"start": v(9.22, 17.54) * mm, "mid": v(9.84, 18.16) * mm, "end": v(9.22, 18.77) * mm});
            skArc(sketch, "E1822", {"start": v(-9.23, 17.54) * mm, "mid": v(-9.84, 16.93) * mm, "end": v(-9.23, 16.31) * mm});
            skArc(sketch, "E1823", {"start": v(9.22, 20) * mm, "mid": v(9.84, 20.62) * mm, "end": v(9.22, 21.23) * mm});
            skArc(sketch, "E1824", {"start": v(9.22, 22.46) * mm, "mid": v(9.84, 23.08) * mm, "end": v(9.22, 23.7) * mm});
            skArc(sketch, "E1825", {"start": v(9.22, 24.92) * mm, "mid": v(9.84, 25.54) * mm, "end": v(9.22, 26.15) * mm});
            skArc(sketch, "E1826", {"start": v(-9.23, 22.46) * mm, "mid": v(-9.84, 21.85) * mm, "end": v(-9.23, 21.23) * mm});
            skArc(sketch, "E1827", {"start": v(-9.23, 24.92) * mm, "mid": v(-9.84, 24.3) * mm, "end": v(-9.23, 23.7) * mm});
            skArc(sketch, "E1828", {"start": v(-9.23, 29.84) * mm, "mid": v(-9.84, 29.23) * mm, "end": v(-9.23, 28.61) * mm});
            skArc(sketch, "E1829", {"start": v(-9.23, 20) * mm, "mid": v(-9.84, 19.39) * mm, "end": v(-9.23, 18.77) * mm});
            skArc(sketch, "E1830", {"start": v(-9.23, 27.38) * mm, "mid": v(-9.84, 26.77) * mm, "end": v(-9.23, 26.15) * mm});
            skLineSegment(sketch, "E1831", {"start": v(-9.23, 29.84) * mm, "end": v(10, 29.84) * mm});
            skArc(sketch, "E1832", {"start": v(9.22, 27.38) * mm, "mid": v(9.84, 28) * mm, "end": v(9.22, 28.61) * mm});
            skLineSegment(sketch, "E1833.MirrorCS", {"start": v(10, 9.84) * mm, "end": v(10, 10) * mm});
            skLineSegment(sketch, "E1834.MirrorCS", {"start": v(-10, 10) * mm, "end": v(-10, 9.84) * mm});
            skLineSegment(sketch, "E1835.MirrorCS", {"start": v(9.84, 9.84) * mm, "end": v(9.84, 10) * mm});
            skLineSegment(sketch, "E1836.MirrorCS", {"start": v(-9.84, 9.84) * mm, "end": v(-9.84, 10) * mm});
            skLineSegment(sketch, "E1837.MirrorCS", {"start": v(-9.84, -10) * mm, "end": v(-9.23, -10) * mm});
            skLineSegment(sketch, "E1838.MirrorCS", {"start": v(-10, -9.84) * mm, "end": v(-10, -10) * mm});
            skLineSegment(sketch, "E1839.MirrorCS", {"start": v(9.84, -10) * mm, "end": v(9.84, -9.84) * mm});
            skLineSegment(sketch, "E1840.MirrorCS", {"start": v(-9.84, -10) * mm, "end": v(-9.84, -9.84) * mm});
            skLineSegment(sketch, "E1841.MirrorCS", {"start": v(10, -10) * mm, "end": v(9.84, -10) * mm});
            skLineSegment(sketch, "E1842.MirrorCS", {"start": v(-9.84, -10) * mm, "end": v(-10, -10) * mm});
            skLineSegment(sketch, "E1843.MirrorCS", {"start": v(10, -10) * mm, "end": v(10, -9.84) * mm});
            skLineSegment(sketch, "E1844.MirrorCS", {"start": v(-9.23, -10) * mm, "end": v(-9.23, -9.84) * mm});
            skLineSegment(sketch, "E1845.MirrorCS", {"start": v(9.22, 9.84) * mm, "end": v(9.22, 10) * mm});
            skLineSegment(sketch, "E1846.MirrorCS", {"start": v(9.84, -10) * mm, "end": v(9.22, -10) * mm});
            skLineSegment(sketch, "E1847.MirrorCS", {"start": v(-9.23, 9.84) * mm, "end": v(-9.23, 10) * mm});
            skLineSegment(sketch, "E1848.MirrorCS", {"start": v(9.22, -10) * mm, "end": v(9.22, -9.84) * mm});
            skLineSegment(sketch, "E1849.MirrorCS", {"start": v(9.84, 3.7) * mm, "end": v(9.84, 4.92) * mm});
            skLineSegment(sketch, "E1850.MirrorCS", {"start": v(-10, 8.61) * mm, "end": v(-10, 7.38) * mm});
            skLineSegment(sketch, "E1851.MirrorCS", {"start": v(-10, -1.23) * mm, "end": v(-10, -2.46) * mm});
            skLineSegment(sketch, "E1852.MirrorCS", {"start": v(-9.23, -4.92) * mm, "end": v(9.22, -4.92) * mm});
            skLineSegment(sketch, "E1853.MirrorCS", {"start": v(-9.23, 7.38) * mm, "end": v(-9.23, 8.61) * mm});
            skLineSegment(sketch, "E1854.MirrorCS", {"start": v(10, -9.84) * mm, "end": v(-10, -9.84) * mm});
            skLineSegment(sketch, "E1855.MirrorCS", {"start": v(-9.84, 2.46) * mm, "end": v(-9.84, 3.7) * mm});
            skLineSegment(sketch, "E1856.MirrorCS", {"start": v(10, 9.84) * mm, "end": v(-10, 9.84) * mm});
            skLineSegment(sketch, "E1857.MirrorCS", {"start": v(10, 0) * mm, "end": v(-10, 0) * mm});
            skLineSegment(sketch, "E1858.MirrorCS", {"start": v(9.22, -6.15) * mm, "end": v(-9.23, -6.15) * mm});
            skLineSegment(sketch, "E1859.MirrorCS", {"start": v(9.22, -6.15) * mm, "end": v(9.22, -4.92) * mm});
            skLineSegment(sketch, "E1860.MirrorCS", {"start": v(-10, 9.84) * mm, "end": v(-10, 8.61) * mm});
            skLineSegment(sketch, "E1861.MirrorCS", {"start": v(-10, 0) * mm, "end": v(-10, -1.23) * mm});
            skLineSegment(sketch, "E1862.MirrorCS", {"start": v(-9.23, -9.84) * mm, "end": v(-9.23, -8.6) * mm});
            skLineSegment(sketch, "E1863.MirrorCS", {"start": v(9.84, 6.15) * mm, "end": v(9.84, 7.38) * mm});
            skLineSegment(sketch, "E1864.MirrorCS", {"start": v(-9.23, -7.38) * mm, "end": v(9.22, -7.38) * mm});
            skLineSegment(sketch, "E1865.MirrorCS", {"start": v(10, 1.23) * mm, "end": v(-10, 1.23) * mm});
            skLineSegment(sketch, "E1866.MirrorCS", {"start": v(10, -8.6) * mm, "end": v(-10, -8.6) * mm});
            skLineSegment(sketch, "E1867.MirrorCS", {"start": v(9.22, -3.69) * mm, "end": v(9.22, -2.46) * mm});
            skLineSegment(sketch, "E1868.MirrorCS", {"start": v(-9.84, 4.92) * mm, "end": v(-9.84, 6.15) * mm});
            skLineSegment(sketch, "E1869.MirrorCS", {"start": v(-10, 1.23) * mm, "end": v(-10, 0) * mm});
            skLineSegment(sketch, "E1870.MirrorCS", {"start": v(-10, -8.6) * mm, "end": v(-10, -9.84) * mm});
            skLineSegment(sketch, "E1871.MirrorCS", {"start": v(-9.23, -7.38) * mm, "end": v(-9.23, -6.15) * mm});
            skLineSegment(sketch, "E1872.MirrorCS", {"start": v(9.84, 8.61) * mm, "end": v(9.84, 9.84) * mm});
            skLineSegment(sketch, "E1873.MirrorCS", {"start": v(10, 2.46) * mm, "end": v(-10, 2.46) * mm});
            skLineSegment(sketch, "E1874.MirrorCS", {"start": v(9.22, -1.23) * mm, "end": v(9.22, 0) * mm});
            skLineSegment(sketch, "E1875.MirrorCS", {"start": v(-9.84, 7.38) * mm, "end": v(-9.84, 8.61) * mm});
            skLineSegment(sketch, "E1876.MirrorCS", {"start": v(9.22, 8.61) * mm, "end": v(-9.23, 8.61) * mm});
            skLineSegment(sketch, "E1877.MirrorCS", {"start": v(9.84, -8.6) * mm, "end": v(9.84, -7.38) * mm});
            skLineSegment(sketch, "E1878.MirrorCS", {"start": v(-10, 2.46) * mm, "end": v(-10, 1.23) * mm});
            skLineSegment(sketch, "E1879.MirrorCS", {"start": v(-10, -7.38) * mm, "end": v(-10, -8.6) * mm});
            skLineSegment(sketch, "E1880.MirrorCS", {"start": v(-9.23, -4.92) * mm, "end": v(-9.23, -3.69) * mm});
            skLineSegment(sketch, "E1881.MirrorCS", {"start": v(-9.23, 7.38) * mm, "end": v(9.22, 7.38) * mm});
            skLineSegment(sketch, "E1882.MirrorCS", {"start": v(9.84, -6.15) * mm, "end": v(9.84, -4.92) * mm});
            skLineSegment(sketch, "E1883.MirrorCS", {"start": v(-10, 3.7) * mm, "end": v(-10, 2.46) * mm});
            skLineSegment(sketch, "E1884.MirrorCS", {"start": v(-10, -6.15) * mm, "end": v(-10, -7.38) * mm});
            skLineSegment(sketch, "E1885.MirrorCS", {"start": v(-9.23, 4.92) * mm, "end": v(9.22, 4.92) * mm});
            skLineSegment(sketch, "E1886.MirrorCS", {"start": v(-9.23, -2.46) * mm, "end": v(-9.23, -1.23) * mm});
            skLineSegment(sketch, "E1887.MirrorCS", {"start": v(10, 3.7) * mm, "end": v(-10, 3.7) * mm});
            skLineSegment(sketch, "E1888.MirrorCS", {"start": v(9.22, 1.23) * mm, "end": v(9.22, 2.46) * mm});
            skLineSegment(sketch, "E1889.MirrorCS", {"start": v(-9.84, -9.84) * mm, "end": v(-9.84, -8.6) * mm});
            skLineSegment(sketch, "E1890.MirrorCS", {"start": v(9.22, 6.15) * mm, "end": v(-9.23, 6.15) * mm});
            skLineSegment(sketch, "E1891.MirrorCS", {"start": v(-9.84, -7.38) * mm, "end": v(-9.84, -6.15) * mm});
            skLineSegment(sketch, "E1892.MirrorCS", {"start": v(9.22, 3.7) * mm, "end": v(9.22, 4.92) * mm});
            skLineSegment(sketch, "E1893.MirrorCS", {"start": v(9.84, -3.69) * mm, "end": v(9.84, -2.46) * mm});
            skLineSegment(sketch, "E1894.MirrorCS", {"start": v(-10, 4.92) * mm, "end": v(-10, 3.7) * mm});
            skLineSegment(sketch, "E1895.MirrorCS", {"start": v(-10, -4.92) * mm, "end": v(-10, -6.15) * mm});
            skLineSegment(sketch, "E1896.MirrorCS", {"start": v(-9.23, 0) * mm, "end": v(-9.23, 1.23) * mm});
            skLineSegment(sketch, "E1897.MirrorCS", {"start": v(-9.84, -4.92) * mm, "end": v(-9.84, -3.69) * mm});
            skLineSegment(sketch, "E1898.MirrorCS", {"start": v(10, -3.69) * mm, "end": v(-10, -3.69) * mm});
            skLineSegment(sketch, "E1899.MirrorCS", {"start": v(9.22, 6.15) * mm, "end": v(9.22, 7.38) * mm});
            skLineSegment(sketch, "E1900.MirrorCS", {"start": v(10, 3.7) * mm, "end": v(10, 4.92) * mm});
            skLineSegment(sketch, "E1901.MirrorCS", {"start": v(-9.23, 2.46) * mm, "end": v(-9.23, 3.7) * mm});
            skLineSegment(sketch, "E1902.MirrorCS", {"start": v(9.22, 8.61) * mm, "end": v(9.22, 9.84) * mm});
            skLineSegment(sketch, "E1903.MirrorCS", {"start": v(-9.84, -2.46) * mm, "end": v(-9.84, -1.23) * mm});
            skLineSegment(sketch, "E1904.MirrorCS", {"start": v(10, 6.15) * mm, "end": v(10, 7.38) * mm});
            skLineSegment(sketch, "E1905.MirrorCS", {"start": v(10, 0) * mm, "end": v(10, 1.23) * mm});
            skLineSegment(sketch, "E1906.MirrorCS", {"start": v(-10, 6.15) * mm, "end": v(-10, 4.92) * mm});
            skLineSegment(sketch, "E1907.MirrorCS", {"start": v(10, 1.23) * mm, "end": v(10, 2.46) * mm});
            skLineSegment(sketch, "E1908.MirrorCS", {"start": v(10, -2.46) * mm, "end": v(-10, -2.46) * mm});
            skLineSegment(sketch, "E1909.MirrorCS", {"start": v(10, 4.92) * mm, "end": v(10, 6.15) * mm});
            skLineSegment(sketch, "E1910.MirrorCS", {"start": v(-10, -3.69) * mm, "end": v(-10, -4.92) * mm});
            skLineSegment(sketch, "E1911.MirrorCS", {"start": v(9.22, -1.23) * mm, "end": v(-9.23, -1.23) * mm});
            skLineSegment(sketch, "E1912.MirrorCS", {"start": v(10, 2.46) * mm, "end": v(10, 3.7) * mm});
            skLineSegment(sketch, "E1913.MirrorCS", {"start": v(-9.23, 4.92) * mm, "end": v(-9.23, 6.15) * mm});
            skLineSegment(sketch, "E1914.MirrorCS", {"start": v(9.22, -8.6) * mm, "end": v(9.22, -7.38) * mm});
            skLineSegment(sketch, "E1915.MirrorCS", {"start": v(-9.84, 1.23) * mm, "end": v(-9.84, 2.46) * mm});
            skLineSegment(sketch, "E1916.MirrorCS", {"start": v(9.22, -7.38) * mm, "end": v(9.22, -6.15) * mm});
            skArc(sketch, "E1917.MirrorCS", {"start": v(-9.23, -9.84) * mm, "mid": v(-9.84, -9.22) * mm, "end": v(-9.23, -8.6) * mm});
            skLineSegment(sketch, "E1918.MirrorCS", {"start": v(9.84, 4.92) * mm, "end": v(9.84, 6.15) * mm});
            skLineSegment(sketch, "E1919.MirrorCS", {"start": v(-9.23, 8.61) * mm, "end": v(-9.23, 9.84) * mm});
            skArc(sketch, "E1920.MirrorCS", {"start": v(-9.23, 0) * mm, "mid": v(-9.84, 0.62) * mm, "end": v(-9.23, 1.23) * mm});
            skLineSegment(sketch, "E1921.MirrorCS", {"start": v(9.22, -4.92) * mm, "end": v(9.22, -3.69) * mm});
            skLineSegment(sketch, "E1922.MirrorCS", {"start": v(-9.84, 3.7) * mm, "end": v(-9.84, 4.92) * mm});
            skArc(sketch, "E1923.MirrorCS", {"start": v(-9.23, -7.38) * mm, "mid": v(-9.84, -6.76) * mm, "end": v(-9.23, -6.15) * mm});
            skLineSegment(sketch, "E1924.MirrorCS", {"start": v(-9.23, -8.6) * mm, "end": v(-9.23, -7.38) * mm});
            skLineSegment(sketch, "E1925.MirrorCS", {"start": v(9.84, 7.38) * mm, "end": v(9.84, 8.61) * mm});
            skLineSegment(sketch, "E1926.MirrorCS", {"start": v(-9.23, -9.84) * mm, "end": v(10, -9.84) * mm});
            skLineSegment(sketch, "E1927.MirrorCS", {"start": v(9.22, -8.6) * mm, "end": v(-9.23, -8.6) * mm});
            skLineSegment(sketch, "E1928.MirrorCS", {"start": v(-10, 9.84) * mm, "end": v(9.22, 9.84) * mm});
            skLineSegment(sketch, "E1929.MirrorCS", {"start": v(9.22, -2.46) * mm, "end": v(9.22, -1.23) * mm});
            skLineSegment(sketch, "E1930.MirrorCS", {"start": v(-9.84, 6.15) * mm, "end": v(-9.84, 7.38) * mm});
            skArc(sketch, "E1931.MirrorCS", {"start": v(9.22, -7.38) * mm, "mid": v(9.84, -8) * mm, "end": v(9.22, -8.6) * mm});
            skArc(sketch, "E1932.MirrorCS", {"start": v(9.22, 9.84) * mm, "mid": v(9.84, 9.23) * mm, "end": v(9.22, 8.61) * mm});
            skLineSegment(sketch, "E1933.MirrorCS", {"start": v(9.84, -9.84) * mm, "end": v(9.84, -8.6) * mm});
            skLineSegment(sketch, "E1934.MirrorCS", {"start": v(10, -7.38) * mm, "end": v(-10, -7.38) * mm});
            skLineSegment(sketch, "E1935.MirrorCS", {"start": v(-9.23, -6.15) * mm, "end": v(-9.23, -4.92) * mm});
            skArc(sketch, "E1936.MirrorCS", {"start": v(-9.23, 7.38) * mm, "mid": v(-9.84, 8) * mm, "end": v(-9.23, 8.61) * mm});
            skLineSegment(sketch, "E1937.MirrorCS", {"start": v(9.22, 0) * mm, "end": v(9.22, 1.23) * mm});
            skLineSegment(sketch, "E1938.MirrorCS", {"start": v(-9.84, 8.61) * mm, "end": v(-9.84, 9.84) * mm});
            skArc(sketch, "E1939.MirrorCS", {"start": v(9.22, 7.38) * mm, "mid": v(9.84, 6.77) * mm, "end": v(9.22, 6.15) * mm});
            skLineSegment(sketch, "E1940.MirrorCS", {"start": v(-9.84, -8.6) * mm, "end": v(-9.84, -7.38) * mm});
            skLineSegment(sketch, "E1941.MirrorCS", {"start": v(9.22, 2.46) * mm, "end": v(9.22, 3.7) * mm});
            skArc(sketch, "E1942.MirrorCS", {"start": v(9.22, 4.92) * mm, "mid": v(9.84, 4.3) * mm, "end": v(9.22, 3.7) * mm});
            skLineSegment(sketch, "E1943.MirrorCS", {"start": v(9.84, -7.38) * mm, "end": v(9.84, -6.15) * mm});
            skLineSegment(sketch, "E1944.MirrorCS", {"start": v(10, -6.15) * mm, "end": v(-10, -6.15) * mm});
            skLineSegment(sketch, "E1945.MirrorCS", {"start": v(-9.23, -3.69) * mm, "end": v(-9.23, -2.46) * mm});
            skArc(sketch, "E1946.MirrorCS", {"start": v(-9.23, 4.92) * mm, "mid": v(-9.84, 5.54) * mm, "end": v(-9.23, 6.15) * mm});
            skLineSegment(sketch, "E1947.MirrorCS", {"start": v(9.84, -4.92) * mm, "end": v(9.84, -3.69) * mm});
            skLineSegment(sketch, "E1948.MirrorCS", {"start": v(10, 4.92) * mm, "end": v(-10, 4.92) * mm});
            skLineSegment(sketch, "E1949.MirrorCS", {"start": v(10, -4.92) * mm, "end": v(-10, -4.92) * mm});
            skLineSegment(sketch, "E1950.MirrorCS", {"start": v(9.22, 3.7) * mm, "end": v(-9.23, 3.7) * mm});
            skLineSegment(sketch, "E1951.MirrorCS", {"start": v(-9.23, -1.23) * mm, "end": v(-9.23, 0) * mm});
            skArc(sketch, "E1952.MirrorCS", {"start": v(9.22, 2.46) * mm, "mid": v(9.84, 1.85) * mm, "end": v(9.22, 1.23) * mm});
            skLineSegment(sketch, "E1953.MirrorCS", {"start": v(-9.84, -6.15) * mm, "end": v(-9.84, -4.92) * mm});
            skLineSegment(sketch, "E1954.MirrorCS", {"start": v(-9.23, 2.46) * mm, "end": v(9.22, 2.46) * mm});
            skLineSegment(sketch, "E1955.MirrorCS", {"start": v(9.22, 4.92) * mm, "end": v(9.22, 6.15) * mm});
            skArc(sketch, "E1956.MirrorCS", {"start": v(-9.23, 2.46) * mm, "mid": v(-9.84, 3.08) * mm, "end": v(-9.23, 3.7) * mm});
            skLineSegment(sketch, "E1957.MirrorCS", {"start": v(9.84, -2.46) * mm, "end": v(9.84, -1.23) * mm});
            skLineSegment(sketch, "E1958.MirrorCS", {"start": v(10, 6.15) * mm, "end": v(-10, 6.15) * mm});
            skLineSegment(sketch, "E1959.MirrorCS", {"start": v(9.22, 1.23) * mm, "end": v(-9.23, 1.23) * mm});
            skLineSegment(sketch, "E1960.MirrorCS", {"start": v(-9.23, 1.23) * mm, "end": v(-9.23, 2.46) * mm});
            skArc(sketch, "E1961.MirrorCS", {"start": v(9.22, 0) * mm, "mid": v(9.84, -0.61) * mm, "end": v(9.22, -1.23) * mm});
            skLineSegment(sketch, "E1962.MirrorCS", {"start": v(-9.23, 0) * mm, "end": v(9.22, 0) * mm});
            skLineSegment(sketch, "E1963.MirrorCS", {"start": v(9.22, 7.38) * mm, "end": v(9.22, 8.61) * mm});
            skArc(sketch, "E1964.MirrorCS", {"start": v(9.22, -2.46) * mm, "mid": v(9.84, -3.07) * mm, "end": v(9.22, -3.69) * mm});
            skLineSegment(sketch, "E1965.MirrorCS", {"start": v(10, 7.38) * mm, "end": v(10, 8.61) * mm});
            skLineSegment(sketch, "E1966.MirrorCS", {"start": v(10, 8.61) * mm, "end": v(10, 9.84) * mm});
            skLineSegment(sketch, "E1967.MirrorCS", {"start": v(-9.23, -2.46) * mm, "end": v(9.22, -2.46) * mm});
            skLineSegment(sketch, "E1968.MirrorCS", {"start": v(10, -2.46) * mm, "end": v(10, -1.23) * mm});
            skLineSegment(sketch, "E1969.MirrorCS", {"start": v(-10, -2.46) * mm, "end": v(-10, -3.69) * mm});
            skLineSegment(sketch, "E1970.MirrorCS", {"start": v(10, 8.61) * mm, "end": v(-10, 8.61) * mm});
            skLineSegment(sketch, "E1971.MirrorCS", {"start": v(-9.23, 6.15) * mm, "end": v(-9.23, 7.38) * mm});
            skLineSegment(sketch, "E1972.MirrorCS", {"start": v(10, -4.92) * mm, "end": v(10, -3.69) * mm});
            skLineSegment(sketch, "E1973.MirrorCS", {"start": v(10, -3.69) * mm, "end": v(10, -2.46) * mm});
            skLineSegment(sketch, "E1974.MirrorCS", {"start": v(10, -6.15) * mm, "end": v(10, -4.92) * mm});
            skLineSegment(sketch, "E1975.MirrorCS", {"start": v(10, 10) * mm, "end": v(10, -10) * mm});
            skLineSegment(sketch, "E1976.MirrorCS", {"start": v(10, -7.38) * mm, "end": v(10, -6.15) * mm});
            skArc(sketch, "E1977.MirrorCS", {"start": v(-9.23, -2.46) * mm, "mid": v(-9.84, -1.84) * mm, "end": v(-9.23, -1.23) * mm});
            skLineSegment(sketch, "E1978.MirrorCS", {"start": v(-9.23, 3.7) * mm, "end": v(-9.23, 4.92) * mm});
            skLineSegment(sketch, "E1979.MirrorCS", {"start": v(10, -8.6) * mm, "end": v(10, -7.38) * mm});
            skLineSegment(sketch, "E1980.MirrorCS", {"start": v(10, -9.84) * mm, "end": v(10, -8.6) * mm});
            skLineSegment(sketch, "E1981.MirrorCS", {"start": v(-10, 10) * mm, "end": v(-10, -10) * mm});
            skPoint(sketch, "E1982.MirrorP", {"position": v(0, 0) * mm});
            skLineSegment(sketch, "E1983.MirrorCS", {"start": v(9.84, 2.46) * mm, "end": v(9.84, 3.7) * mm});
            skLineSegment(sketch, "E1984.MirrorCS", {"start": v(10, -1.23) * mm, "end": v(10, 0) * mm});
            skArc(sketch, "E1985.MirrorCS", {"start": v(9.22, -4.92) * mm, "mid": v(9.84, -5.53) * mm, "end": v(9.22, -6.15) * mm});
            skLineSegment(sketch, "E1986.MirrorCS", {"start": v(10, 7.38) * mm, "end": v(-10, 7.38) * mm});
            skLineSegment(sketch, "E1987.MirrorCS", {"start": v(-9.84, -3.69) * mm, "end": v(-9.84, -2.46) * mm});
            skLineSegment(sketch, "E1988.MirrorCS", {"start": v(10, -1.23) * mm, "end": v(-10, -1.23) * mm});
            skLineSegment(sketch, "E1989.MirrorCS", {"start": v(10, -10) * mm, "end": v(-10, -10) * mm});
            skLineSegment(sketch, "E1990.MirrorCS", {"start": v(-10, 7.38) * mm, "end": v(-10, 6.15) * mm});
            skArc(sketch, "E1991.MirrorCS", {"start": v(-9.23, -4.92) * mm, "mid": v(-9.84, -4.3) * mm, "end": v(-9.23, -3.69) * mm});
            skLineSegment(sketch, "E1992.MirrorCS", {"start": v(9.22, -9.84) * mm, "end": v(9.22, -8.6) * mm});
            skLineSegment(sketch, "E1993.MirrorCS", {"start": v(9.84, 1.23) * mm, "end": v(9.84, 2.46) * mm});
            skLineSegment(sketch, "E1994.MirrorCS", {"start": v(9.22, -3.69) * mm, "end": v(-9.23, -3.69) * mm});
            skSolve(sketch);
        }
        {
            var Q0;
            Q0=qCreatedBy(id+"F7.planeOp",FACE);
            var sketch = newSketch(context, id + "F31", { "sketchPlane" : qUnion([Q0])});
            skCircle(sketch, "E1995", {"center": v(-9.84, 3.07) * mm, "radius": 0.2 * mm});
            skSolve(sketch);
        }
        {
            var Q0;
            Q0=qCreatedBy(id+"F29.planeOp",FACE);
            cPlane(context, id + "F32", {"entities" : qUnion([Q0]), "cplaneType" : CPlaneType.OFFSET, "offset" : getVariable(context, 'd'), "width" : 150 * mm, "height" : 150 * mm});
        }
        {
            var Q0;
            Q0=qCreatedBy(id+"F32.planeOp",FACE);
            var sketch = newSketch(context, id + "F33", { "sketchPlane" : qUnion([Q0])});
            skLineSegment(sketch, "E1996.bottom", {"start": v(10, 10) * mm, "end": v(-10, 10) * mm});
            skLineSegment(sketch, "E1996.top", {"start": v(10, -10) * mm, "end": v(-10, -10) * mm});
            skLineSegment(sketch, "E1996.left", {"start": v(10, 10) * mm, "end": v(10, -10) * mm});
            skLineSegment(sketch, "E1996.right", {"start": v(-10, 10) * mm, "end": v(-10, -10) * mm});
            skPoint(sketch, "E1996.middle", {"position": v(0, 0) * mm});
            skLineSegment(sketch, "E1997", {"start": v(-10, 10) * mm, "end": v(-9.84, 10) * mm});
            skLineSegment(sketch, "E1998", {"start": v(-9.84, 10) * mm, "end": v(-8.61, 10) * mm});
            skLineSegment(sketch, "E1999", {"start": v(-8.61, 10) * mm, "end": v(-7.38, 10) * mm});
            skLineSegment(sketch, "E2000", {"start": v(-7.38, 10) * mm, "end": v(-6.15, 10) * mm});
            skLineSegment(sketch, "E2001", {"start": v(-6.15, 10) * mm, "end": v(-4.92, 10) * mm});
            skLineSegment(sketch, "E2002", {"start": v(-4.92, 10) * mm, "end": v(-3.7, 10) * mm});
            skLineSegment(sketch, "E2003", {"start": v(-3.7, 10) * mm, "end": v(-2.46, 10) * mm});
            skLineSegment(sketch, "E2004", {"start": v(-2.46, 10) * mm, "end": v(-1.23, 10) * mm});
            skLineSegment(sketch, "E2005", {"start": v(-1.23, 10) * mm, "end": v(0, 10) * mm});
            skLineSegment(sketch, "E2006", {"start": v(0, 10) * mm, "end": v(1.23, 10) * mm});
            skLineSegment(sketch, "E2007", {"start": v(1.23, 10) * mm, "end": v(2.46, 10) * mm});
            skLineSegment(sketch, "E2008", {"start": v(2.46, 10) * mm, "end": v(3.69, 10) * mm});
            skLineSegment(sketch, "E2009", {"start": v(3.69, 10) * mm, "end": v(4.92, 10) * mm});
            skLineSegment(sketch, "E2010", {"start": v(4.92, 10) * mm, "end": v(6.15, 10) * mm});
            skLineSegment(sketch, "E2011", {"start": v(6.15, 10) * mm, "end": v(7.38, 10) * mm});
            skLineSegment(sketch, "E2012", {"start": v(7.38, 10) * mm, "end": v(8.6, 10) * mm});
            skLineSegment(sketch, "E2013", {"start": v(8.6, 10) * mm, "end": v(9.84, 10) * mm});
            skLineSegment(sketch, "E2014", {"start": v(9.84, 10) * mm, "end": v(10, 10) * mm});
            skLineSegment(sketch, "E2015", {"start": v(-9.84, 10) * mm, "end": v(-9.84, -10) * mm});
            skLineSegment(sketch, "E2016", {"start": v(-9.84, -10) * mm, "end": v(-10, -10) * mm});
            skLineSegment(sketch, "E2017", {"start": v(-8.61, 10) * mm, "end": v(-8.61, -10) * mm});
            skLineSegment(sketch, "E2018", {"start": v(-8.61, -10) * mm, "end": v(-9.84, -10) * mm});
            skLineSegment(sketch, "E2019", {"start": v(-7.38, 10) * mm, "end": v(-7.38, -10) * mm});
            skLineSegment(sketch, "E2020", {"start": v(-7.38, -10) * mm, "end": v(-8.61, -10) * mm});
            skLineSegment(sketch, "E2021", {"start": v(-6.15, 10) * mm, "end": v(-6.15, -10) * mm});
            skLineSegment(sketch, "E2022", {"start": v(-6.15, -10) * mm, "end": v(-7.38, -10) * mm});
            skLineSegment(sketch, "E2023", {"start": v(-4.92, 10) * mm, "end": v(-4.92, -10) * mm});
            skLineSegment(sketch, "E2024", {"start": v(-4.92, -10) * mm, "end": v(-6.15, -10) * mm});
            skLineSegment(sketch, "E2025", {"start": v(-3.7, 10) * mm, "end": v(-3.7, -10) * mm});
            skLineSegment(sketch, "E2026", {"start": v(-3.7, -10) * mm, "end": v(-4.92, -10) * mm});
            skLineSegment(sketch, "E2027", {"start": v(-2.46, 10) * mm, "end": v(-2.46, -10) * mm});
            skLineSegment(sketch, "E2028", {"start": v(-2.46, -10) * mm, "end": v(-3.7, -10) * mm});
            skLineSegment(sketch, "E2029", {"start": v(-1.23, 10) * mm, "end": v(-1.23, -10) * mm});
            skLineSegment(sketch, "E2030", {"start": v(-1.23, -10) * mm, "end": v(-2.46, -10) * mm});
            skLineSegment(sketch, "E2031", {"start": v(0, 10) * mm, "end": v(0, -10) * mm});
            skLineSegment(sketch, "E2032", {"start": v(0, -10) * mm, "end": v(-1.23, -10) * mm});
            skLineSegment(sketch, "E2033", {"start": v(1.23, 10) * mm, "end": v(1.23, -10) * mm});
            skLineSegment(sketch, "E2034", {"start": v(1.23, -10) * mm, "end": v(0, -10) * mm});
            skLineSegment(sketch, "E2035", {"start": v(2.46, 10) * mm, "end": v(2.46, -10) * mm});
            skLineSegment(sketch, "E2036", {"start": v(2.46, -10) * mm, "end": v(1.23, -10) * mm});
            skLineSegment(sketch, "E2037", {"start": v(3.69, 10) * mm, "end": v(3.69, -10) * mm});
            skLineSegment(sketch, "E2038", {"start": v(3.69, -10) * mm, "end": v(2.46, -10) * mm});
            skLineSegment(sketch, "E2039", {"start": v(4.92, 10) * mm, "end": v(4.92, -10) * mm});
            skLineSegment(sketch, "E2040", {"start": v(4.92, -10) * mm, "end": v(3.69, -10) * mm});
            skLineSegment(sketch, "E2041", {"start": v(6.15, 10) * mm, "end": v(6.15, -10) * mm});
            skLineSegment(sketch, "E2042", {"start": v(6.15, -10) * mm, "end": v(4.92, -10) * mm});
            skLineSegment(sketch, "E2043", {"start": v(7.38, 10) * mm, "end": v(7.38, -10) * mm});
            skLineSegment(sketch, "E2044", {"start": v(7.38, -10) * mm, "end": v(6.15, -10) * mm});
            skLineSegment(sketch, "E2045", {"start": v(8.6, 10) * mm, "end": v(8.6, -10) * mm});
            skLineSegment(sketch, "E2046", {"start": v(8.6, -10) * mm, "end": v(7.38, -10) * mm});
            skLineSegment(sketch, "E2047", {"start": v(9.84, 10) * mm, "end": v(9.84, -10) * mm});
            skLineSegment(sketch, "E2048", {"start": v(9.84, -10) * mm, "end": v(8.6, -10) * mm});
            skLineSegment(sketch, "E2049", {"start": v(10, -10) * mm, "end": v(9.84, -10) * mm});
            skLineSegment(sketch, "E2050", {"start": v(-10, 9.84) * mm, "end": v(-9.84, 9.84) * mm});
            skLineSegment(sketch, "E2051", {"start": v(-9.84, 9.84) * mm, "end": v(-8.61, 9.84) * mm});
            skLineSegment(sketch, "E2052", {"start": v(-8.61, 9.84) * mm, "end": v(-7.38, 9.84) * mm});
            skLineSegment(sketch, "E2053", {"start": v(-7.38, 9.84) * mm, "end": v(-6.15, 9.84) * mm});
            skLineSegment(sketch, "E2054", {"start": v(-6.15, 9.84) * mm, "end": v(-4.92, 9.84) * mm});
            skLineSegment(sketch, "E2055", {"start": v(-4.92, 9.84) * mm, "end": v(-3.7, 9.84) * mm});
            skLineSegment(sketch, "E2056", {"start": v(-3.7, 9.84) * mm, "end": v(-2.46, 9.84) * mm});
            skLineSegment(sketch, "E2057", {"start": v(-2.46, 9.84) * mm, "end": v(-1.23, 9.84) * mm});
            skLineSegment(sketch, "E2058", {"start": v(-1.23, 9.84) * mm, "end": v(0, 9.84) * mm});
            skLineSegment(sketch, "E2059", {"start": v(0, 9.84) * mm, "end": v(1.23, 9.84) * mm});
            skLineSegment(sketch, "E2060", {"start": v(1.23, 9.84) * mm, "end": v(2.46, 9.84) * mm});
            skLineSegment(sketch, "E2061", {"start": v(2.46, 9.84) * mm, "end": v(3.69, 9.84) * mm});
            skLineSegment(sketch, "E2062", {"start": v(3.69, 9.84) * mm, "end": v(4.92, 9.84) * mm});
            skLineSegment(sketch, "E2063", {"start": v(4.92, 9.84) * mm, "end": v(6.15, 9.84) * mm});
            skLineSegment(sketch, "E2064", {"start": v(6.15, 9.84) * mm, "end": v(7.38, 9.84) * mm});
            skLineSegment(sketch, "E2065", {"start": v(7.38, 9.84) * mm, "end": v(8.6, 9.84) * mm});
            skLineSegment(sketch, "E2066", {"start": v(8.6, 9.84) * mm, "end": v(9.84, 9.84) * mm});
            skLineSegment(sketch, "E2067", {"start": v(9.84, 9.84) * mm, "end": v(10, 9.84) * mm});
            skLineSegment(sketch, "E2068", {"start": v(-10, -9.84) * mm, "end": v(-9.84, -9.84) * mm});
            skLineSegment(sketch, "E2069", {"start": v(-9.84, -9.84) * mm, "end": v(-8.61, -9.84) * mm});
            skLineSegment(sketch, "E2070", {"start": v(-8.61, -9.84) * mm, "end": v(-7.38, -9.84) * mm});
            skLineSegment(sketch, "E2071", {"start": v(-7.38, -9.84) * mm, "end": v(-6.15, -9.84) * mm});
            skLineSegment(sketch, "E2072", {"start": v(-6.15, -9.84) * mm, "end": v(-4.92, -9.84) * mm});
            skLineSegment(sketch, "E2073", {"start": v(-4.92, -9.84) * mm, "end": v(-3.7, -9.84) * mm});
            skLineSegment(sketch, "E2074", {"start": v(-3.7, -9.84) * mm, "end": v(-2.46, -9.84) * mm});
            skLineSegment(sketch, "E2075", {"start": v(-2.46, -9.84) * mm, "end": v(-1.23, -9.84) * mm});
            skLineSegment(sketch, "E2076", {"start": v(-1.23, -9.84) * mm, "end": v(0, -9.84) * mm});
            skLineSegment(sketch, "E2077", {"start": v(0, -9.84) * mm, "end": v(1.23, -9.84) * mm});
            skLineSegment(sketch, "E2078", {"start": v(1.23, -9.84) * mm, "end": v(2.46, -9.84) * mm});
            skLineSegment(sketch, "E2079", {"start": v(2.46, -9.84) * mm, "end": v(3.69, -9.84) * mm});
            skLineSegment(sketch, "E2080", {"start": v(3.69, -9.84) * mm, "end": v(4.92, -9.84) * mm});
            skLineSegment(sketch, "E2081", {"start": v(4.92, -9.84) * mm, "end": v(6.15, -9.84) * mm});
            skLineSegment(sketch, "E2082", {"start": v(6.15, -9.84) * mm, "end": v(7.38, -9.84) * mm});
            skLineSegment(sketch, "E2083", {"start": v(7.38, -9.84) * mm, "end": v(8.6, -9.84) * mm});
            skLineSegment(sketch, "E2084", {"start": v(8.6, -9.84) * mm, "end": v(9.84, -9.84) * mm});
            skLineSegment(sketch, "E2085", {"start": v(9.84, -9.84) * mm, "end": v(10, -9.84) * mm});
            skLineSegment(sketch, "E2086", {"start": v(-10, 10) * mm, "end": v(-10, 9.84) * mm});
            skLineSegment(sketch, "E2087", {"start": v(-10, -9.84) * mm, "end": v(-10, -10) * mm});
            skLineSegment(sketch, "E2088", {"start": v(10, -9.84) * mm, "end": v(10, -10) * mm});
            skLineSegment(sketch, "E2089", {"start": v(10, 9.84) * mm, "end": v(10, 10) * mm});
            skLineSegment(sketch, "E2090", {"start": v(-10, 9.84) * mm, "end": v(-10, 9.23) * mm});
            skLineSegment(sketch, "E2091", {"start": v(-10, 9.23) * mm, "end": v(-9.84, 9.23) * mm});
            skLineSegment(sketch, "E2092", {"start": v(-9.84, 9.23) * mm, "end": v(-8.61, 9.23) * mm});
            skLineSegment(sketch, "E2093", {"start": v(-8.61, 9.23) * mm, "end": v(-7.38, 9.23) * mm});
            skLineSegment(sketch, "E2094", {"start": v(-7.38, 9.23) * mm, "end": v(-6.15, 9.23) * mm});
            skLineSegment(sketch, "E2095", {"start": v(-6.15, 9.23) * mm, "end": v(-4.92, 9.23) * mm});
            skLineSegment(sketch, "E2096", {"start": v(-4.92, 9.23) * mm, "end": v(-3.7, 9.23) * mm});
            skLineSegment(sketch, "E2097", {"start": v(-3.7, 9.23) * mm, "end": v(-2.46, 9.23) * mm});
            skLineSegment(sketch, "E2098", {"start": v(-2.46, 9.23) * mm, "end": v(-1.23, 9.23) * mm});
            skLineSegment(sketch, "E2099", {"start": v(-1.23, 9.23) * mm, "end": v(0, 9.23) * mm});
            skLineSegment(sketch, "E2100", {"start": v(0, 9.23) * mm, "end": v(1.23, 9.23) * mm});
            skLineSegment(sketch, "E2101", {"start": v(1.23, 9.23) * mm, "end": v(2.46, 9.23) * mm});
            skLineSegment(sketch, "E2102", {"start": v(2.46, 9.23) * mm, "end": v(3.69, 9.23) * mm});
            skLineSegment(sketch, "E2103", {"start": v(3.69, 9.23) * mm, "end": v(4.92, 9.23) * mm});
            skLineSegment(sketch, "E2104", {"start": v(4.92, 9.23) * mm, "end": v(6.15, 9.23) * mm});
            skLineSegment(sketch, "E2105", {"start": v(6.15, 9.23) * mm, "end": v(7.38, 9.23) * mm});
            skLineSegment(sketch, "E2106", {"start": v(7.38, 9.23) * mm, "end": v(8.6, 9.23) * mm});
            skLineSegment(sketch, "E2107", {"start": v(8.6, 9.23) * mm, "end": v(9.84, 9.23) * mm});
            skLineSegment(sketch, "E2108", {"start": v(9.84, 9.23) * mm, "end": v(10, 9.23) * mm});
            skLineSegment(sketch, "E2109", {"start": v(10, 9.23) * mm, "end": v(10, 9.84) * mm});
            skLineSegment(sketch, "E2110", {"start": v(-10, -9.84) * mm, "end": v(-10, -9.22) * mm});
            skLineSegment(sketch, "E2111", {"start": v(-10, -9.22) * mm, "end": v(-9.84, -9.22) * mm});
            skLineSegment(sketch, "E2112", {"start": v(-9.84, -9.22) * mm, "end": v(-8.61, -9.22) * mm});
            skLineSegment(sketch, "E2113", {"start": v(-8.61, -9.22) * mm, "end": v(-7.38, -9.22) * mm});
            skLineSegment(sketch, "E2114", {"start": v(-7.38, -9.22) * mm, "end": v(-6.15, -9.22) * mm});
            skLineSegment(sketch, "E2115", {"start": v(-6.15, -9.22) * mm, "end": v(-4.92, -9.22) * mm});
            skLineSegment(sketch, "E2116", {"start": v(-4.92, -9.22) * mm, "end": v(-3.7, -9.22) * mm});
            skLineSegment(sketch, "E2117", {"start": v(-3.7, -9.22) * mm, "end": v(-2.46, -9.22) * mm});
            skLineSegment(sketch, "E2118", {"start": v(-2.46, -9.22) * mm, "end": v(-1.23, -9.22) * mm});
            skLineSegment(sketch, "E2119", {"start": v(-1.23, -9.22) * mm, "end": v(0, -9.22) * mm});
            skLineSegment(sketch, "E2120", {"start": v(0, -9.22) * mm, "end": v(1.23, -9.22) * mm});
            skLineSegment(sketch, "E2121", {"start": v(1.23, -9.22) * mm, "end": v(2.46, -9.22) * mm});
            skLineSegment(sketch, "E2122", {"start": v(2.46, -9.22) * mm, "end": v(3.69, -9.22) * mm});
            skLineSegment(sketch, "E2123", {"start": v(3.69, -9.22) * mm, "end": v(4.92, -9.22) * mm});
            skLineSegment(sketch, "E2124", {"start": v(4.92, -9.22) * mm, "end": v(6.15, -9.22) * mm});
            skLineSegment(sketch, "E2125", {"start": v(6.15, -9.22) * mm, "end": v(7.38, -9.22) * mm});
            skLineSegment(sketch, "E2126", {"start": v(7.38, -9.22) * mm, "end": v(8.6, -9.22) * mm});
            skLineSegment(sketch, "E2127", {"start": v(8.6, -9.22) * mm, "end": v(9.84, -9.22) * mm});
            skLineSegment(sketch, "E2128", {"start": v(9.84, -9.22) * mm, "end": v(10, -9.22) * mm});
            skLineSegment(sketch, "E2129", {"start": v(9.84, -10) * mm, "end": v(9.84, 9.23) * mm});
            skLineSegment(sketch, "E2130", {"start": v(10, -9.22) * mm, "end": v(10, -9.84) * mm});
            skLineSegment(sketch, "E2131", {"start": v(8.6, 9.23) * mm, "end": v(8.6, -9.22) * mm});
            skLineSegment(sketch, "E2132", {"start": v(7.38, -9.22) * mm, "end": v(7.38, 9.23) * mm});
            skLineSegment(sketch, "E2133", {"start": v(6.15, 9.23) * mm, "end": v(6.15, -9.22) * mm});
            skLineSegment(sketch, "E2134", {"start": v(4.92, -9.22) * mm, "end": v(4.92, 9.23) * mm});
            skLineSegment(sketch, "E2135", {"start": v(3.69, 9.23) * mm, "end": v(3.69, -9.22) * mm});
            skLineSegment(sketch, "E2136", {"start": v(2.46, -9.22) * mm, "end": v(2.46, 9.23) * mm});
            skLineSegment(sketch, "E2137", {"start": v(1.23, 9.23) * mm, "end": v(1.23, -9.22) * mm});
            skLineSegment(sketch, "E2138", {"start": v(0, -9.22) * mm, "end": v(0, 9.23) * mm});
            skLineSegment(sketch, "E2139", {"start": v(-1.23, 9.23) * mm, "end": v(-1.23, -9.22) * mm});
            skLineSegment(sketch, "E2140", {"start": v(-2.46, -9.22) * mm, "end": v(-2.46, 9.23) * mm});
            skLineSegment(sketch, "E2141", {"start": v(-3.7, 9.23) * mm, "end": v(-3.7, -9.22) * mm});
            skLineSegment(sketch, "E2142", {"start": v(-4.92, -9.22) * mm, "end": v(-4.92, 9.23) * mm});
            skLineSegment(sketch, "E2143", {"start": v(-6.15, 9.23) * mm, "end": v(-6.15, -9.22) * mm});
            skLineSegment(sketch, "E2144", {"start": v(-7.38, -9.22) * mm, "end": v(-7.38, 9.23) * mm});
            skLineSegment(sketch, "E2145", {"start": v(-8.61, 9.23) * mm, "end": v(-8.61, -9.22) * mm});
            skArc(sketch, "E2146", {"start": v(9.84, 9.23) * mm, "mid": v(9.22, 9.84) * mm, "end": v(8.6, 9.23) * mm});
            skArc(sketch, "E2147", {"start": v(7.38, -9.22) * mm, "mid": v(8, -9.84) * mm, "end": v(8.6, -9.22) * mm});
            skArc(sketch, "E2148", {"start": v(7.38, 9.23) * mm, "mid": v(6.76, 9.84) * mm, "end": v(6.15, 9.23) * mm});
            skArc(sketch, "E2149", {"start": v(4.92, -9.22) * mm, "mid": v(5.53, -9.84) * mm, "end": v(6.15, -9.22) * mm});
            skArc(sketch, "E2150", {"start": v(4.92, 9.23) * mm, "mid": v(4.3, 9.84) * mm, "end": v(3.69, 9.23) * mm});
            skArc(sketch, "E2151", {"start": v(2.46, 9.23) * mm, "mid": v(1.84, 9.84) * mm, "end": v(1.23, 9.23) * mm});
            skArc(sketch, "E2152", {"start": v(2.46, -9.22) * mm, "mid": v(3.07, -9.84) * mm, "end": v(3.69, -9.22) * mm});
            skArc(sketch, "E2153", {"start": v(0, 9.23) * mm, "mid": v(-0.62, 9.84) * mm, "end": v(-1.23, 9.23) * mm});
            skArc(sketch, "E2154", {"start": v(-2.46, 9.23) * mm, "mid": v(-3.08, 9.84) * mm, "end": v(-3.7, 9.23) * mm});
            skArc(sketch, "E2155", {"start": v(-4.92, 9.23) * mm, "mid": v(-5.54, 9.84) * mm, "end": v(-6.15, 9.23) * mm});
            skArc(sketch, "E2156", {"start": v(-2.46, -9.22) * mm, "mid": v(-1.85, -9.84) * mm, "end": v(-1.23, -9.22) * mm});
            skArc(sketch, "E2157", {"start": v(-4.92, -9.22) * mm, "mid": v(-4.3, -9.84) * mm, "end": v(-3.7, -9.22) * mm});
            skArc(sketch, "E2158", {"start": v(-9.84, -9.22) * mm, "mid": v(-9.23, -9.84) * mm, "end": v(-8.61, -9.22) * mm});
            skArc(sketch, "E2159", {"start": v(0, -9.22) * mm, "mid": v(0.61, -9.84) * mm, "end": v(1.23, -9.22) * mm});
            skArc(sketch, "E2160", {"start": v(-7.38, -9.22) * mm, "mid": v(-6.77, -9.84) * mm, "end": v(-6.15, -9.22) * mm});
            skLineSegment(sketch, "E2161", {"start": v(-9.84, -9.22) * mm, "end": v(-9.84, 10) * mm});
            skArc(sketch, "E2162", {"start": v(-7.38, 9.23) * mm, "mid": v(-8, 9.84) * mm, "end": v(-8.61, 9.23) * mm});
            skSolve(sketch);
        }
        {
            var Q0;
            Q0=qCreatedBy(id+"F3.planeOp",FACE);
            var sketch = newSketch(context, id + "F34", { "sketchPlane" : qUnion([Q0])});
            skCircle(sketch, "E2163", {"center": v(-9.84, 3.48) * mm, "radius": 0.2 * mm});
            skSolve(sketch);
        }
        {
            var Q0;
            Q0=qCreatedBy(id+"F32.planeOp",FACE);
            cPlane(context, id + "F35", {"entities" : qUnion([Q0]), "cplaneType" : CPlaneType.OFFSET, "offset" : getVariable(context, 'd'), "width" : 150 * mm, "height" : 150 * mm});
        }
        {
            var Q0;
            Q0=qCreatedBy(id+"F35.planeOp",FACE);
            var sketch = newSketch(context, id + "F36", { "sketchPlane" : qUnion([Q0])});
            skLineSegment(sketch, "E2164.bottom", {"start": v(10, 10) * mm, "end": v(10, 30) * mm});
            skLineSegment(sketch, "E2164.top", {"start": v(-10, 10) * mm, "end": v(-10, 30) * mm});
            skLineSegment(sketch, "E2164.left", {"start": v(10, 10) * mm, "end": v(-10, 10) * mm});
            skLineSegment(sketch, "E2164.right", {"start": v(10, 30) * mm, "end": v(-10, 30) * mm});
            skPoint(sketch, "E2164.middle", {"position": v(0, 20) * mm});
            skLineSegment(sketch, "E2165", {"start": v(10, 30) * mm, "end": v(10, 29.84) * mm});
            skLineSegment(sketch, "E2166", {"start": v(10, 29.84) * mm, "end": v(10, 28.61) * mm});
            skLineSegment(sketch, "E2167", {"start": v(10, 28.61) * mm, "end": v(10, 27.38) * mm});
            skLineSegment(sketch, "E2168", {"start": v(10, 27.38) * mm, "end": v(10, 26.15) * mm});
            skLineSegment(sketch, "E2169", {"start": v(10, 26.15) * mm, "end": v(10, 24.92) * mm});
            skLineSegment(sketch, "E2170", {"start": v(10, 24.92) * mm, "end": v(10, 23.69) * mm});
            skLineSegment(sketch, "E2171", {"start": v(10, 23.69) * mm, "end": v(10, 22.46) * mm});
            skLineSegment(sketch, "E2172", {"start": v(10, 22.46) * mm, "end": v(10, 21.23) * mm});
            skLineSegment(sketch, "E2173", {"start": v(10, 21.23) * mm, "end": v(10, 20) * mm});
            skLineSegment(sketch, "E2174", {"start": v(10, 20) * mm, "end": v(10, 18.77) * mm});
            skLineSegment(sketch, "E2175", {"start": v(10, 18.77) * mm, "end": v(10, 17.54) * mm});
            skLineSegment(sketch, "E2176", {"start": v(10, 17.54) * mm, "end": v(10, 16.31) * mm});
            skLineSegment(sketch, "E2177", {"start": v(10, 16.31) * mm, "end": v(10, 15.08) * mm});
            skLineSegment(sketch, "E2178", {"start": v(10, 15.08) * mm, "end": v(10, 13.85) * mm});
            skLineSegment(sketch, "E2179", {"start": v(10, 13.85) * mm, "end": v(10, 12.62) * mm});
            skLineSegment(sketch, "E2180", {"start": v(10, 12.62) * mm, "end": v(10, 11.4) * mm});
            skLineSegment(sketch, "E2181", {"start": v(10, 11.4) * mm, "end": v(10, 10.16) * mm});
            skLineSegment(sketch, "E2182", {"start": v(10, 10.16) * mm, "end": v(10, 10) * mm});
            skLineSegment(sketch, "E2183", {"start": v(10, 29.84) * mm, "end": v(-10, 29.84) * mm});
            skLineSegment(sketch, "E2184", {"start": v(-10, 29.84) * mm, "end": v(-10, 30) * mm});
            skLineSegment(sketch, "E2185", {"start": v(10, 28.61) * mm, "end": v(-10, 28.61) * mm});
            skLineSegment(sketch, "E2186", {"start": v(-10, 28.61) * mm, "end": v(-10, 29.84) * mm});
            skLineSegment(sketch, "E2187", {"start": v(10, 27.38) * mm, "end": v(-10, 27.38) * mm});
            skLineSegment(sketch, "E2188", {"start": v(-10, 27.38) * mm, "end": v(-10, 28.61) * mm});
            skLineSegment(sketch, "E2189", {"start": v(10, 26.15) * mm, "end": v(-10, 26.15) * mm});
            skLineSegment(sketch, "E2190", {"start": v(-10, 26.15) * mm, "end": v(-10, 27.38) * mm});
            skLineSegment(sketch, "E2191", {"start": v(10, 24.92) * mm, "end": v(-10, 24.92) * mm});
            skLineSegment(sketch, "E2192", {"start": v(-10, 24.92) * mm, "end": v(-10, 26.15) * mm});
            skLineSegment(sketch, "E2193", {"start": v(10, 23.7) * mm, "end": v(-10, 23.69) * mm});
            skLineSegment(sketch, "E2194", {"start": v(-10, 23.69) * mm, "end": v(-10, 24.92) * mm});
            skLineSegment(sketch, "E2195", {"start": v(10, 22.46) * mm, "end": v(-10, 22.46) * mm});
            skLineSegment(sketch, "E2196", {"start": v(-10, 22.46) * mm, "end": v(-10, 23.69) * mm});
            skLineSegment(sketch, "E2197", {"start": v(10, 21.23) * mm, "end": v(-10, 21.23) * mm});
            skLineSegment(sketch, "E2198", {"start": v(-10, 21.23) * mm, "end": v(-10, 22.46) * mm});
            skLineSegment(sketch, "E2199", {"start": v(10, 20) * mm, "end": v(-10, 20) * mm});
            skLineSegment(sketch, "E2200", {"start": v(-10, 20) * mm, "end": v(-10, 21.23) * mm});
            skLineSegment(sketch, "E2201", {"start": v(10, 18.77) * mm, "end": v(-10, 18.77) * mm});
            skLineSegment(sketch, "E2202", {"start": v(-10, 18.77) * mm, "end": v(-10, 20) * mm});
            skLineSegment(sketch, "E2203", {"start": v(10, 17.54) * mm, "end": v(-10, 17.54) * mm});
            skLineSegment(sketch, "E2204", {"start": v(-10, 17.54) * mm, "end": v(-10, 18.77) * mm});
            skLineSegment(sketch, "E2205", {"start": v(10, 16.31) * mm, "end": v(-10, 16.31) * mm});
            skLineSegment(sketch, "E2206", {"start": v(-10, 16.31) * mm, "end": v(-10, 17.54) * mm});
            skLineSegment(sketch, "E2207", {"start": v(10, 15.08) * mm, "end": v(-10, 15.08) * mm});
            skLineSegment(sketch, "E2208", {"start": v(-10, 15.08) * mm, "end": v(-10, 16.31) * mm});
            skLineSegment(sketch, "E2209", {"start": v(10, 13.85) * mm, "end": v(-10, 13.85) * mm});
            skLineSegment(sketch, "E2210", {"start": v(-10, 13.85) * mm, "end": v(-10, 15.08) * mm});
            skLineSegment(sketch, "E2211", {"start": v(10, 12.62) * mm, "end": v(-10, 12.62) * mm});
            skLineSegment(sketch, "E2212", {"start": v(-10, 12.62) * mm, "end": v(-10, 13.85) * mm});
            skLineSegment(sketch, "E2213", {"start": v(10, 11.4) * mm, "end": v(-10, 11.4) * mm});
            skLineSegment(sketch, "E2214", {"start": v(-10, 11.4) * mm, "end": v(-10, 12.62) * mm});
            skLineSegment(sketch, "E2215", {"start": v(10, 10.16) * mm, "end": v(-10, 10.16) * mm});
            skLineSegment(sketch, "E2216", {"start": v(-10, 10.16) * mm, "end": v(-10, 11.4) * mm});
            skLineSegment(sketch, "E2217", {"start": v(-10, 10) * mm, "end": v(-10, 10.16) * mm});
            skLineSegment(sketch, "E2218", {"start": v(9.84, 30) * mm, "end": v(9.84, 29.84) * mm});
            skLineSegment(sketch, "E2219", {"start": v(9.84, 29.84) * mm, "end": v(9.84, 28.61) * mm});
            skLineSegment(sketch, "E2220", {"start": v(9.84, 28.61) * mm, "end": v(9.84, 27.38) * mm});
            skLineSegment(sketch, "E2221", {"start": v(9.84, 27.38) * mm, "end": v(9.84, 26.15) * mm});
            skLineSegment(sketch, "E2222", {"start": v(9.84, 26.15) * mm, "end": v(9.84, 24.92) * mm});
            skLineSegment(sketch, "E2223", {"start": v(9.84, 24.92) * mm, "end": v(9.84, 23.7) * mm});
            skLineSegment(sketch, "E2224", {"start": v(9.84, 23.7) * mm, "end": v(9.84, 22.46) * mm});
            skLineSegment(sketch, "E2225", {"start": v(9.84, 22.46) * mm, "end": v(9.84, 21.23) * mm});
            skLineSegment(sketch, "E2226", {"start": v(9.84, 18.77) * mm, "end": v(9.84, 17.54) * mm});
            skLineSegment(sketch, "E2227", {"start": v(9.84, 17.54) * mm, "end": v(9.84, 16.31) * mm});
            skLineSegment(sketch, "E2228", {"start": v(9.84, 16.31) * mm, "end": v(9.84, 15.08) * mm});
            skLineSegment(sketch, "E2229", {"start": v(9.84, 15.08) * mm, "end": v(9.84, 13.85) * mm});
            skLineSegment(sketch, "E2230", {"start": v(9.84, 13.85) * mm, "end": v(9.84, 12.62) * mm});
            skLineSegment(sketch, "E2231", {"start": v(9.84, 12.62) * mm, "end": v(9.84, 11.4) * mm});
            skLineSegment(sketch, "E2232", {"start": v(9.84, 11.4) * mm, "end": v(9.84, 10.16) * mm});
            skLineSegment(sketch, "E2233", {"start": v(9.84, 10.16) * mm, "end": v(9.84, 10) * mm});
            skLineSegment(sketch, "E2234", {"start": v(-9.84, 30) * mm, "end": v(-9.84, 29.84) * mm});
            skLineSegment(sketch, "E2235", {"start": v(-9.84, 29.84) * mm, "end": v(-9.84, 28.61) * mm});
            skLineSegment(sketch, "E2236", {"start": v(-9.84, 28.61) * mm, "end": v(-9.84, 27.38) * mm});
            skLineSegment(sketch, "E2237", {"start": v(-9.84, 27.38) * mm, "end": v(-9.84, 26.15) * mm});
            skLineSegment(sketch, "E2238", {"start": v(-9.84, 26.15) * mm, "end": v(-9.84, 24.92) * mm});
            skLineSegment(sketch, "E2239", {"start": v(-9.84, 24.92) * mm, "end": v(-9.84, 23.69) * mm});
            skLineSegment(sketch, "E2240", {"start": v(-9.84, 23.69) * mm, "end": v(-9.84, 22.46) * mm});
            skLineSegment(sketch, "E2241", {"start": v(-9.84, 22.46) * mm, "end": v(-9.84, 21.23) * mm});
            skLineSegment(sketch, "E2242", {"start": v(-9.84, 18.77) * mm, "end": v(-9.84, 17.54) * mm});
            skLineSegment(sketch, "E2243", {"start": v(-9.84, 17.54) * mm, "end": v(-9.84, 16.31) * mm});
            skLineSegment(sketch, "E2244", {"start": v(-9.84, 16.31) * mm, "end": v(-9.84, 15.08) * mm});
            skLineSegment(sketch, "E2245", {"start": v(-9.84, 15.08) * mm, "end": v(-9.84, 13.85) * mm});
            skLineSegment(sketch, "E2246", {"start": v(-9.84, 13.85) * mm, "end": v(-9.84, 12.62) * mm});
            skLineSegment(sketch, "E2247", {"start": v(-9.84, 12.62) * mm, "end": v(-9.84, 11.4) * mm});
            skLineSegment(sketch, "E2248", {"start": v(-9.84, 11.4) * mm, "end": v(-9.84, 10.16) * mm});
            skLineSegment(sketch, "E2249", {"start": v(-9.84, 10.16) * mm, "end": v(-9.84, 10) * mm});
            skLineSegment(sketch, "E2250", {"start": v(10, 30) * mm, "end": v(9.84, 30) * mm});
            skLineSegment(sketch, "E2251", {"start": v(-9.84, 30) * mm, "end": v(-10, 30) * mm});
            skLineSegment(sketch, "E2252", {"start": v(-9.84, 10) * mm, "end": v(-10, 10) * mm});
            skLineSegment(sketch, "E2253", {"start": v(9.84, 10) * mm, "end": v(10, 10) * mm});
            skLineSegment(sketch, "E2254", {"start": v(9.84, 30) * mm, "end": v(9.22, 30) * mm});
            skLineSegment(sketch, "E2255", {"start": v(9.22, 30) * mm, "end": v(9.22, 29.84) * mm});
            skLineSegment(sketch, "E2256", {"start": v(9.22, 29.84) * mm, "end": v(9.22, 28.61) * mm});
            skLineSegment(sketch, "E2257", {"start": v(9.22, 28.61) * mm, "end": v(9.22, 27.38) * mm});
            skLineSegment(sketch, "E2258", {"start": v(9.22, 27.38) * mm, "end": v(9.22, 26.15) * mm});
            skLineSegment(sketch, "E2259", {"start": v(9.22, 26.15) * mm, "end": v(9.22, 24.92) * mm});
            skLineSegment(sketch, "E2260", {"start": v(9.22, 24.92) * mm, "end": v(9.22, 23.7) * mm});
            skLineSegment(sketch, "E2261", {"start": v(9.22, 23.7) * mm, "end": v(9.22, 22.46) * mm});
            skLineSegment(sketch, "E2262", {"start": v(9.22, 22.46) * mm, "end": v(9.22, 21.23) * mm});
            skLineSegment(sketch, "E2263", {"start": v(9.22, 21.23) * mm, "end": v(9.22, 20) * mm});
            skLineSegment(sketch, "E2264", {"start": v(9.22, 20) * mm, "end": v(9.22, 18.77) * mm});
            skLineSegment(sketch, "E2265", {"start": v(9.22, 18.77) * mm, "end": v(9.22, 17.54) * mm});
            skLineSegment(sketch, "E2266", {"start": v(9.22, 17.54) * mm, "end": v(9.22, 16.31) * mm});
            skLineSegment(sketch, "E2267", {"start": v(9.22, 16.31) * mm, "end": v(9.22, 15.08) * mm});
            skLineSegment(sketch, "E2268", {"start": v(9.22, 15.08) * mm, "end": v(9.22, 13.85) * mm});
            skLineSegment(sketch, "E2269", {"start": v(9.22, 13.85) * mm, "end": v(9.22, 12.62) * mm});
            skLineSegment(sketch, "E2270", {"start": v(9.22, 12.62) * mm, "end": v(9.22, 11.4) * mm});
            skLineSegment(sketch, "E2271", {"start": v(9.22, 11.4) * mm, "end": v(9.22, 10.16) * mm});
            skLineSegment(sketch, "E2272", {"start": v(9.22, 10.16) * mm, "end": v(9.22, 10) * mm});
            skLineSegment(sketch, "E2273", {"start": v(9.22, 10) * mm, "end": v(9.84, 10) * mm});
            skLineSegment(sketch, "E2274", {"start": v(-9.84, 30) * mm, "end": v(-9.23, 30) * mm});
            skLineSegment(sketch, "E2275", {"start": v(-9.23, 30) * mm, "end": v(-9.23, 29.84) * mm});
            skLineSegment(sketch, "E2276", {"start": v(-9.23, 29.84) * mm, "end": v(-9.23, 28.61) * mm});
            skLineSegment(sketch, "E2277", {"start": v(-9.23, 28.61) * mm, "end": v(-9.23, 27.38) * mm});
            skLineSegment(sketch, "E2278", {"start": v(-9.23, 27.38) * mm, "end": v(-9.23, 26.15) * mm});
            skLineSegment(sketch, "E2279", {"start": v(-9.23, 26.15) * mm, "end": v(-9.23, 24.92) * mm});
            skLineSegment(sketch, "E2280", {"start": v(-9.23, 24.92) * mm, "end": v(-9.23, 23.69) * mm});
            skLineSegment(sketch, "E2281", {"start": v(-9.23, 23.69) * mm, "end": v(-9.23, 22.46) * mm});
            skLineSegment(sketch, "E2282", {"start": v(-9.23, 22.46) * mm, "end": v(-9.23, 21.23) * mm});
            skLineSegment(sketch, "E2283", {"start": v(-9.23, 21.23) * mm, "end": v(-9.23, 20) * mm});
            skLineSegment(sketch, "E2284", {"start": v(-9.23, 20) * mm, "end": v(-9.23, 18.77) * mm});
            skLineSegment(sketch, "E2285", {"start": v(-9.23, 18.77) * mm, "end": v(-9.23, 17.54) * mm});
            skLineSegment(sketch, "E2286", {"start": v(-9.23, 17.54) * mm, "end": v(-9.23, 16.31) * mm});
            skLineSegment(sketch, "E2287", {"start": v(-9.23, 16.31) * mm, "end": v(-9.23, 15.08) * mm});
            skLineSegment(sketch, "E2288", {"start": v(-9.23, 15.08) * mm, "end": v(-9.23, 13.85) * mm});
            skLineSegment(sketch, "E2289", {"start": v(-9.23, 13.85) * mm, "end": v(-9.23, 12.62) * mm});
            skLineSegment(sketch, "E2290", {"start": v(-9.23, 12.62) * mm, "end": v(-9.23, 11.4) * mm});
            skLineSegment(sketch, "E2291", {"start": v(-9.23, 11.4) * mm, "end": v(-9.23, 10.16) * mm});
            skLineSegment(sketch, "E2292", {"start": v(-9.23, 10.16) * mm, "end": v(-9.23, 10) * mm});
            skLineSegment(sketch, "E2293", {"start": v(-10, 10.16) * mm, "end": v(9.22, 10.16) * mm});
            skLineSegment(sketch, "E2294", {"start": v(-9.23, 10) * mm, "end": v(-9.84, 10) * mm});
            skLineSegment(sketch, "E2295", {"start": v(9.22, 11.4) * mm, "end": v(-9.23, 11.4) * mm});
            skLineSegment(sketch, "E2296", {"start": v(-9.23, 12.62) * mm, "end": v(9.22, 12.62) * mm});
            skLineSegment(sketch, "E2297", {"start": v(9.22, 13.85) * mm, "end": v(-9.23, 13.85) * mm});
            skLineSegment(sketch, "E2298", {"start": v(-9.23, 15.08) * mm, "end": v(9.22, 15.08) * mm});
            skLineSegment(sketch, "E2299", {"start": v(9.22, 16.31) * mm, "end": v(-9.23, 16.31) * mm});
            skLineSegment(sketch, "E2300", {"start": v(-9.23, 17.54) * mm, "end": v(9.22, 17.54) * mm});
            skLineSegment(sketch, "E2301", {"start": v(9.22, 18.77) * mm, "end": v(-9.23, 18.77) * mm});
            skLineSegment(sketch, "E2302", {"start": v(-9.23, 20) * mm, "end": v(9.22, 20) * mm});
            skLineSegment(sketch, "E2303", {"start": v(9.22, 21.23) * mm, "end": v(-9.23, 21.23) * mm});
            skLineSegment(sketch, "E2304", {"start": v(-9.23, 22.46) * mm, "end": v(9.22, 22.46) * mm});
            skLineSegment(sketch, "E2305", {"start": v(9.22, 23.7) * mm, "end": v(-9.23, 23.69) * mm});
            skLineSegment(sketch, "E2306", {"start": v(-9.23, 24.92) * mm, "end": v(9.22, 24.92) * mm});
            skLineSegment(sketch, "E2307", {"start": v(9.22, 26.15) * mm, "end": v(-9.23, 26.15) * mm});
            skLineSegment(sketch, "E2308", {"start": v(-9.23, 27.38) * mm, "end": v(9.22, 27.38) * mm});
            skLineSegment(sketch, "E2309", {"start": v(9.22, 28.61) * mm, "end": v(-9.23, 28.61) * mm});
            skArc(sketch, "E2310", {"start": v(9.22, 10.16) * mm, "mid": v(9.84, 10.78) * mm, "end": v(9.22, 11.4) * mm});
            skArc(sketch, "E2311", {"start": v(-9.23, 12.62) * mm, "mid": v(-9.84, 12) * mm, "end": v(-9.23, 11.4) * mm});
            skArc(sketch, "E2312", {"start": v(9.22, 12.62) * mm, "mid": v(9.84, 13.24) * mm, "end": v(9.22, 13.85) * mm});
            skArc(sketch, "E2313", {"start": v(-9.23, 15.08) * mm, "mid": v(-9.84, 14.47) * mm, "end": v(-9.23, 13.85) * mm});
            skArc(sketch, "E2314", {"start": v(9.22, 15.08) * mm, "mid": v(9.84, 15.7) * mm, "end": v(9.22, 16.31) * mm});
            skArc(sketch, "E2315", {"start": v(9.22, 17.54) * mm, "mid": v(9.84, 18.16) * mm, "end": v(9.22, 18.77) * mm});
            skArc(sketch, "E2316", {"start": v(-9.23, 17.54) * mm, "mid": v(-9.84, 16.93) * mm, "end": v(-9.23, 16.31) * mm});
            skArc(sketch, "E2317", {"start": v(9.22, 20) * mm, "mid": v(9.84, 20.62) * mm, "end": v(9.22, 21.23) * mm});
            skArc(sketch, "E2318", {"start": v(9.22, 22.46) * mm, "mid": v(9.84, 23.08) * mm, "end": v(9.22, 23.7) * mm});
            skArc(sketch, "E2319", {"start": v(9.22, 24.92) * mm, "mid": v(9.84, 25.54) * mm, "end": v(9.22, 26.15) * mm});
            skArc(sketch, "E2320", {"start": v(-9.23, 22.46) * mm, "mid": v(-9.84, 21.84) * mm, "end": v(-9.23, 21.23) * mm});
            skArc(sketch, "E2321", {"start": v(-9.23, 24.92) * mm, "mid": v(-9.84, 24.3) * mm, "end": v(-9.23, 23.69) * mm});
            skArc(sketch, "E2322", {"start": v(-9.23, 29.84) * mm, "mid": v(-9.84, 29.23) * mm, "end": v(-9.23, 28.61) * mm});
            skArc(sketch, "E2323", {"start": v(-9.23, 20) * mm, "mid": v(-9.84, 19.39) * mm, "end": v(-9.23, 18.77) * mm});
            skArc(sketch, "E2324", {"start": v(-9.23, 27.38) * mm, "mid": v(-9.84, 26.77) * mm, "end": v(-9.23, 26.15) * mm});
            skLineSegment(sketch, "E2325", {"start": v(-9.23, 29.84) * mm, "end": v(10, 29.84) * mm});
            skArc(sketch, "E2326", {"start": v(9.22, 27.38) * mm, "mid": v(9.84, 28) * mm, "end": v(9.22, 28.6) * mm});
            skLineSegment(sketch, "E2327.MirrorCS", {"start": v(10, 9.84) * mm, "end": v(10, 10) * mm});
            skLineSegment(sketch, "E2328.MirrorCS", {"start": v(-10, 10) * mm, "end": v(-10, 9.84) * mm});
            skLineSegment(sketch, "E2329.MirrorCS", {"start": v(9.84, 9.84) * mm, "end": v(9.84, 10) * mm});
            skLineSegment(sketch, "E2330.MirrorCS", {"start": v(-9.84, 9.84) * mm, "end": v(-9.84, 10) * mm});
            skLineSegment(sketch, "E2331.MirrorCS", {"start": v(-9.84, -10) * mm, "end": v(-9.23, -10) * mm});
            skLineSegment(sketch, "E2332.MirrorCS", {"start": v(-10, -9.84) * mm, "end": v(-10, -10) * mm});
            skLineSegment(sketch, "E2333.MirrorCS", {"start": v(9.84, -10) * mm, "end": v(9.84, -9.84) * mm});
            skLineSegment(sketch, "E2334.MirrorCS", {"start": v(-9.84, -10) * mm, "end": v(-9.84, -9.84) * mm});
            skLineSegment(sketch, "E2335.MirrorCS", {"start": v(10, -10) * mm, "end": v(9.84, -10) * mm});
            skLineSegment(sketch, "E2336.MirrorCS", {"start": v(-9.84, -10) * mm, "end": v(-10, -10) * mm});
            skLineSegment(sketch, "E2337.MirrorCS", {"start": v(10, -10) * mm, "end": v(10, -9.84) * mm});
            skLineSegment(sketch, "E2338.MirrorCS", {"start": v(-9.23, -10) * mm, "end": v(-9.23, -9.84) * mm});
            skLineSegment(sketch, "E2339.MirrorCS", {"start": v(9.22, 9.84) * mm, "end": v(9.22, 10) * mm});
            skLineSegment(sketch, "E2340.MirrorCS", {"start": v(9.84, -10) * mm, "end": v(9.22, -10) * mm});
            skLineSegment(sketch, "E2341.MirrorCS", {"start": v(-9.23, 9.84) * mm, "end": v(-9.23, 10) * mm});
            skLineSegment(sketch, "E2342.MirrorCS", {"start": v(9.22, -10) * mm, "end": v(9.22, -9.84) * mm});
            skLineSegment(sketch, "E2343.MirrorCS", {"start": v(9.84, 3.7) * mm, "end": v(9.84, 4.92) * mm});
            skLineSegment(sketch, "E2344.MirrorCS", {"start": v(-10, 8.61) * mm, "end": v(-10, 7.38) * mm});
            skLineSegment(sketch, "E2345.MirrorCS", {"start": v(-10, -1.23) * mm, "end": v(-10, -2.46) * mm});
            skLineSegment(sketch, "E2346.MirrorCS", {"start": v(-9.23, -4.92) * mm, "end": v(9.22, -4.92) * mm});
            skLineSegment(sketch, "E2347.MirrorCS", {"start": v(-9.23, 7.38) * mm, "end": v(-9.23, 8.61) * mm});
            skLineSegment(sketch, "E2348.MirrorCS", {"start": v(10, -9.84) * mm, "end": v(-10, -9.84) * mm});
            skLineSegment(sketch, "E2349.MirrorCS", {"start": v(-9.84, 2.46) * mm, "end": v(-9.84, 3.7) * mm});
            skLineSegment(sketch, "E2350.MirrorCS", {"start": v(10, 9.84) * mm, "end": v(-10, 9.84) * mm});
            skLineSegment(sketch, "E2351.MirrorCS", {"start": v(10, 0) * mm, "end": v(-10, 0) * mm});
            skLineSegment(sketch, "E2352.MirrorCS", {"start": v(9.22, -6.15) * mm, "end": v(-9.23, -6.15) * mm});
            skLineSegment(sketch, "E2353.MirrorCS", {"start": v(9.22, -6.15) * mm, "end": v(9.22, -4.92) * mm});
            skLineSegment(sketch, "E2354.MirrorCS", {"start": v(-10, 9.84) * mm, "end": v(-10, 8.61) * mm});
            skLineSegment(sketch, "E2355.MirrorCS", {"start": v(-10, 0) * mm, "end": v(-10, -1.23) * mm});
            skLineSegment(sketch, "E2356.MirrorCS", {"start": v(-9.23, -9.84) * mm, "end": v(-9.23, -8.6) * mm});
            skLineSegment(sketch, "E2357.MirrorCS", {"start": v(9.84, 6.15) * mm, "end": v(9.84, 7.38) * mm});
            skLineSegment(sketch, "E2358.MirrorCS", {"start": v(-9.23, -7.38) * mm, "end": v(9.22, -7.38) * mm});
            skLineSegment(sketch, "E2359.MirrorCS", {"start": v(10, 1.23) * mm, "end": v(-10, 1.23) * mm});
            skLineSegment(sketch, "E2360.MirrorCS", {"start": v(10, -8.6) * mm, "end": v(-10, -8.6) * mm});
            skLineSegment(sketch, "E2361.MirrorCS", {"start": v(9.22, -3.69) * mm, "end": v(9.22, -2.46) * mm});
            skLineSegment(sketch, "E2362.MirrorCS", {"start": v(-9.84, 4.92) * mm, "end": v(-9.84, 6.15) * mm});
            skLineSegment(sketch, "E2363.MirrorCS", {"start": v(-10, 1.23) * mm, "end": v(-10, 0) * mm});
            skLineSegment(sketch, "E2364.MirrorCS", {"start": v(-10, -8.6) * mm, "end": v(-10, -9.84) * mm});
            skLineSegment(sketch, "E2365.MirrorCS", {"start": v(-9.23, -7.38) * mm, "end": v(-9.23, -6.15) * mm});
            skLineSegment(sketch, "E2366.MirrorCS", {"start": v(9.84, 8.61) * mm, "end": v(9.84, 9.84) * mm});
            skLineSegment(sketch, "E2367.MirrorCS", {"start": v(10, 2.46) * mm, "end": v(-10, 2.46) * mm});
            skLineSegment(sketch, "E2368.MirrorCS", {"start": v(9.22, -1.23) * mm, "end": v(9.22, 0) * mm});
            skLineSegment(sketch, "E2369.MirrorCS", {"start": v(-9.84, 7.38) * mm, "end": v(-9.84, 8.61) * mm});
            skLineSegment(sketch, "E2370.MirrorCS", {"start": v(9.22, 8.61) * mm, "end": v(-9.23, 8.61) * mm});
            skLineSegment(sketch, "E2371.MirrorCS", {"start": v(9.84, -8.6) * mm, "end": v(9.84, -7.38) * mm});
            skLineSegment(sketch, "E2372.MirrorCS", {"start": v(-10, 2.46) * mm, "end": v(-10, 1.23) * mm});
            skLineSegment(sketch, "E2373.MirrorCS", {"start": v(-10, -7.38) * mm, "end": v(-10, -8.6) * mm});
            skLineSegment(sketch, "E2374.MirrorCS", {"start": v(-9.23, -4.92) * mm, "end": v(-9.23, -3.69) * mm});
            skLineSegment(sketch, "E2375.MirrorCS", {"start": v(-9.23, 7.38) * mm, "end": v(9.22, 7.38) * mm});
            skLineSegment(sketch, "E2376.MirrorCS", {"start": v(9.84, -6.15) * mm, "end": v(9.84, -4.92) * mm});
            skLineSegment(sketch, "E2377.MirrorCS", {"start": v(-10, 3.7) * mm, "end": v(-10, 2.46) * mm});
            skLineSegment(sketch, "E2378.MirrorCS", {"start": v(-10, -6.15) * mm, "end": v(-10, -7.38) * mm});
            skLineSegment(sketch, "E2379.MirrorCS", {"start": v(-9.23, 4.92) * mm, "end": v(9.22, 4.92) * mm});
            skLineSegment(sketch, "E2380.MirrorCS", {"start": v(-9.23, -2.46) * mm, "end": v(-9.23, -1.23) * mm});
            skLineSegment(sketch, "E2381.MirrorCS", {"start": v(10, 3.7) * mm, "end": v(-10, 3.7) * mm});
            skLineSegment(sketch, "E2382.MirrorCS", {"start": v(9.22, 1.23) * mm, "end": v(9.22, 2.46) * mm});
            skLineSegment(sketch, "E2383.MirrorCS", {"start": v(-9.84, -9.84) * mm, "end": v(-9.84, -8.6) * mm});
            skLineSegment(sketch, "E2384.MirrorCS", {"start": v(9.22, 6.15) * mm, "end": v(-9.23, 6.15) * mm});
            skLineSegment(sketch, "E2385.MirrorCS", {"start": v(-9.84, -7.38) * mm, "end": v(-9.84, -6.15) * mm});
            skLineSegment(sketch, "E2386.MirrorCS", {"start": v(9.22, 3.7) * mm, "end": v(9.22, 4.92) * mm});
            skLineSegment(sketch, "E2387.MirrorCS", {"start": v(9.84, -3.69) * mm, "end": v(9.84, -2.46) * mm});
            skLineSegment(sketch, "E2388.MirrorCS", {"start": v(-10, 4.92) * mm, "end": v(-10, 3.7) * mm});
            skLineSegment(sketch, "E2389.MirrorCS", {"start": v(-10, -4.92) * mm, "end": v(-10, -6.15) * mm});
            skLineSegment(sketch, "E2390.MirrorCS", {"start": v(-9.23, 0) * mm, "end": v(-9.23, 1.23) * mm});
            skLineSegment(sketch, "E2391.MirrorCS", {"start": v(-9.84, -4.92) * mm, "end": v(-9.84, -3.69) * mm});
            skLineSegment(sketch, "E2392.MirrorCS", {"start": v(10, -3.69) * mm, "end": v(-10, -3.69) * mm});
            skLineSegment(sketch, "E2393.MirrorCS", {"start": v(9.22, 6.15) * mm, "end": v(9.22, 7.38) * mm});
            skLineSegment(sketch, "E2394.MirrorCS", {"start": v(10, 3.7) * mm, "end": v(10, 4.92) * mm});
            skLineSegment(sketch, "E2395.MirrorCS", {"start": v(-9.23, 2.46) * mm, "end": v(-9.23, 3.7) * mm});
            skLineSegment(sketch, "E2396.MirrorCS", {"start": v(-9.84, -2.46) * mm, "end": v(-9.84, -1.23) * mm});
            skLineSegment(sketch, "E2397.MirrorCS", {"start": v(10, 6.15) * mm, "end": v(10, 7.38) * mm});
            skLineSegment(sketch, "E2398.MirrorCS", {"start": v(10, 0) * mm, "end": v(10, 1.23) * mm});
            skLineSegment(sketch, "E2399.MirrorCS", {"start": v(-10, 6.15) * mm, "end": v(-10, 4.92) * mm});
            skLineSegment(sketch, "E2400.MirrorCS", {"start": v(10, 1.23) * mm, "end": v(10, 2.46) * mm});
            skLineSegment(sketch, "E2401.MirrorCS", {"start": v(10, -2.46) * mm, "end": v(-10, -2.46) * mm});
            skLineSegment(sketch, "E2402.MirrorCS", {"start": v(10, 4.92) * mm, "end": v(10, 6.15) * mm});
            skLineSegment(sketch, "E2403.MirrorCS", {"start": v(-10, -3.69) * mm, "end": v(-10, -4.92) * mm});
            skLineSegment(sketch, "E2404.MirrorCS", {"start": v(9.22, -1.23) * mm, "end": v(-9.23, -1.23) * mm});
            skLineSegment(sketch, "E2405.MirrorCS", {"start": v(10, 2.46) * mm, "end": v(10, 3.7) * mm});
            skLineSegment(sketch, "E2406.MirrorCS", {"start": v(-9.23, 4.92) * mm, "end": v(-9.23, 6.15) * mm});
            skLineSegment(sketch, "E2407.MirrorCS", {"start": v(9.22, -8.6) * mm, "end": v(9.22, -7.38) * mm});
            skLineSegment(sketch, "E2408.MirrorCS", {"start": v(-9.84, 1.23) * mm, "end": v(-9.84, 2.46) * mm});
            skLineSegment(sketch, "E2409.MirrorCS", {"start": v(9.22, -7.38) * mm, "end": v(9.22, -6.15) * mm});
            skArc(sketch, "E2410.MirrorCS", {"start": v(-9.23, -9.84) * mm, "mid": v(-9.84, -9.22) * mm, "end": v(-9.23, -8.6) * mm});
            skLineSegment(sketch, "E2411.MirrorCS", {"start": v(9.84, 4.92) * mm, "end": v(9.84, 6.15) * mm});
            skLineSegment(sketch, "E2412.MirrorCS", {"start": v(-9.23, 8.61) * mm, "end": v(-9.23, 9.84) * mm});
            skArc(sketch, "E2413.MirrorCS", {"start": v(-9.23, 0) * mm, "mid": v(-9.84, 0.62) * mm, "end": v(-9.23, 1.23) * mm});
            skLineSegment(sketch, "E2414.MirrorCS", {"start": v(9.22, -4.92) * mm, "end": v(9.22, -3.69) * mm});
            skLineSegment(sketch, "E2415.MirrorCS", {"start": v(-9.84, 3.7) * mm, "end": v(-9.84, 4.92) * mm});
            skArc(sketch, "E2416.MirrorCS", {"start": v(-9.23, -7.38) * mm, "mid": v(-9.84, -6.76) * mm, "end": v(-9.23, -6.15) * mm});
            skLineSegment(sketch, "E2417.MirrorCS", {"start": v(-9.23, -8.6) * mm, "end": v(-9.23, -7.38) * mm});
            skLineSegment(sketch, "E2418.MirrorCS", {"start": v(9.84, 7.38) * mm, "end": v(9.84, 8.61) * mm});
            skLineSegment(sketch, "E2419.MirrorCS", {"start": v(-9.23, -9.84) * mm, "end": v(10, -9.84) * mm});
            skLineSegment(sketch, "E2420.MirrorCS", {"start": v(9.22, -8.6) * mm, "end": v(-9.23, -8.6) * mm});
            skLineSegment(sketch, "E2421.MirrorCS", {"start": v(-10, 9.84) * mm, "end": v(9.22, 9.84) * mm});
            skLineSegment(sketch, "E2422.MirrorCS", {"start": v(9.22, -2.46) * mm, "end": v(9.22, -1.23) * mm});
            skLineSegment(sketch, "E2423.MirrorCS", {"start": v(-9.84, 6.15) * mm, "end": v(-9.84, 7.38) * mm});
            skArc(sketch, "E2424.MirrorCS", {"start": v(9.22, -7.38) * mm, "mid": v(9.84, -8) * mm, "end": v(9.22, -8.6) * mm});
            skArc(sketch, "E2425.MirrorCS", {"start": v(9.22, 9.84) * mm, "mid": v(9.84, 9.23) * mm, "end": v(9.22, 8.61) * mm});
            skLineSegment(sketch, "E2426.MirrorCS", {"start": v(9.84, -9.84) * mm, "end": v(9.84, -8.6) * mm});
            skLineSegment(sketch, "E2427.MirrorCS", {"start": v(10, -7.38) * mm, "end": v(-10, -7.38) * mm});
            skLineSegment(sketch, "E2428.MirrorCS", {"start": v(-9.23, -6.15) * mm, "end": v(-9.23, -4.92) * mm});
            skArc(sketch, "E2429.MirrorCS", {"start": v(-9.23, 7.38) * mm, "mid": v(-9.84, 8) * mm, "end": v(-9.23, 8.61) * mm});
            skLineSegment(sketch, "E2430.MirrorCS", {"start": v(9.22, 0) * mm, "end": v(9.22, 1.23) * mm});
            skLineSegment(sketch, "E2431.MirrorCS", {"start": v(-9.84, 8.61) * mm, "end": v(-9.84, 9.84) * mm});
            skArc(sketch, "E2432.MirrorCS", {"start": v(9.22, 7.38) * mm, "mid": v(9.84, 6.77) * mm, "end": v(9.22, 6.15) * mm});
            skLineSegment(sketch, "E2433.MirrorCS", {"start": v(-9.84, -8.6) * mm, "end": v(-9.84, -7.38) * mm});
            skLineSegment(sketch, "E2434.MirrorCS", {"start": v(9.22, 2.46) * mm, "end": v(9.22, 3.7) * mm});
            skArc(sketch, "E2435.MirrorCS", {"start": v(9.22, 4.92) * mm, "mid": v(9.84, 4.3) * mm, "end": v(9.22, 3.7) * mm});
            skLineSegment(sketch, "E2436.MirrorCS", {"start": v(9.84, -7.38) * mm, "end": v(9.84, -6.15) * mm});
            skLineSegment(sketch, "E2437.MirrorCS", {"start": v(10, -6.15) * mm, "end": v(-10, -6.15) * mm});
            skLineSegment(sketch, "E2438.MirrorCS", {"start": v(-9.23, -3.69) * mm, "end": v(-9.23, -2.46) * mm});
            skArc(sketch, "E2439.MirrorCS", {"start": v(-9.23, 4.92) * mm, "mid": v(-9.84, 5.54) * mm, "end": v(-9.23, 6.15) * mm});
            skLineSegment(sketch, "E2440.MirrorCS", {"start": v(9.84, -4.92) * mm, "end": v(9.84, -3.69) * mm});
            skLineSegment(sketch, "E2441.MirrorCS", {"start": v(10, 4.92) * mm, "end": v(-10, 4.92) * mm});
            skLineSegment(sketch, "E2442.MirrorCS", {"start": v(10, -4.92) * mm, "end": v(-10, -4.92) * mm});
            skLineSegment(sketch, "E2443.MirrorCS", {"start": v(9.22, 3.7) * mm, "end": v(-9.23, 3.7) * mm});
            skLineSegment(sketch, "E2444.MirrorCS", {"start": v(-9.23, -1.23) * mm, "end": v(-9.23, 0) * mm});
            skArc(sketch, "E2445.MirrorCS", {"start": v(9.22, 2.46) * mm, "mid": v(9.84, 1.85) * mm, "end": v(9.22, 1.23) * mm});
            skLineSegment(sketch, "E2446.MirrorCS", {"start": v(-9.84, -6.15) * mm, "end": v(-9.84, -4.92) * mm});
            skLineSegment(sketch, "E2447.MirrorCS", {"start": v(-9.23, 2.46) * mm, "end": v(9.22, 2.46) * mm});
            skLineSegment(sketch, "E2448.MirrorCS", {"start": v(9.22, 4.92) * mm, "end": v(9.22, 6.15) * mm});
            skArc(sketch, "E2449.MirrorCS", {"start": v(-9.23, 2.46) * mm, "mid": v(-9.84, 3.08) * mm, "end": v(-9.23, 3.7) * mm});
            skLineSegment(sketch, "E2450.MirrorCS", {"start": v(9.84, -2.46) * mm, "end": v(9.84, -1.23) * mm});
            skLineSegment(sketch, "E2451.MirrorCS", {"start": v(10, 6.15) * mm, "end": v(-10, 6.15) * mm});
            skLineSegment(sketch, "E2452.MirrorCS", {"start": v(9.22, 1.23) * mm, "end": v(-9.23, 1.23) * mm});
            skLineSegment(sketch, "E2453.MirrorCS", {"start": v(-9.23, 1.23) * mm, "end": v(-9.23, 2.46) * mm});
            skArc(sketch, "E2454.MirrorCS", {"start": v(9.22, 0) * mm, "mid": v(9.84, -0.61) * mm, "end": v(9.22, -1.23) * mm});
            skLineSegment(sketch, "E2455.MirrorCS", {"start": v(-9.23, 0) * mm, "end": v(9.22, 0) * mm});
            skLineSegment(sketch, "E2456.MirrorCS", {"start": v(9.22, 7.38) * mm, "end": v(9.22, 8.61) * mm});
            skArc(sketch, "E2457.MirrorCS", {"start": v(9.22, -2.46) * mm, "mid": v(9.84, -3.07) * mm, "end": v(9.22, -3.69) * mm});
            skLineSegment(sketch, "E2458.MirrorCS", {"start": v(10, 7.38) * mm, "end": v(10, 8.61) * mm});
            skLineSegment(sketch, "E2459.MirrorCS", {"start": v(10, 8.61) * mm, "end": v(10, 9.84) * mm});
            skLineSegment(sketch, "E2460.MirrorCS", {"start": v(-9.23, -2.46) * mm, "end": v(9.22, -2.46) * mm});
            skLineSegment(sketch, "E2461.MirrorCS", {"start": v(10, -2.46) * mm, "end": v(10, -1.23) * mm});
            skLineSegment(sketch, "E2462.MirrorCS", {"start": v(-10, -2.46) * mm, "end": v(-10, -3.69) * mm});
            skLineSegment(sketch, "E2463.MirrorCS", {"start": v(10, 8.61) * mm, "end": v(-10, 8.61) * mm});
            skLineSegment(sketch, "E2464.MirrorCS", {"start": v(-9.23, 6.15) * mm, "end": v(-9.23, 7.38) * mm});
            skLineSegment(sketch, "E2465.MirrorCS", {"start": v(10, -4.92) * mm, "end": v(10, -3.69) * mm});
            skLineSegment(sketch, "E2466.MirrorCS", {"start": v(10, -3.69) * mm, "end": v(10, -2.46) * mm});
            skLineSegment(sketch, "E2467.MirrorCS", {"start": v(10, -6.15) * mm, "end": v(10, -4.92) * mm});
            skLineSegment(sketch, "E2468.MirrorCS", {"start": v(10, 10) * mm, "end": v(10, -10) * mm});
            skLineSegment(sketch, "E2469.MirrorCS", {"start": v(10, -7.38) * mm, "end": v(10, -6.15) * mm});
            skArc(sketch, "E2470.MirrorCS", {"start": v(-9.23, -2.46) * mm, "mid": v(-9.84, -1.84) * mm, "end": v(-9.23, -1.23) * mm});
            skLineSegment(sketch, "E2471.MirrorCS", {"start": v(-9.23, 3.7) * mm, "end": v(-9.23, 4.92) * mm});
            skLineSegment(sketch, "E2472.MirrorCS", {"start": v(10, -8.6) * mm, "end": v(10, -7.38) * mm});
            skLineSegment(sketch, "E2473.MirrorCS", {"start": v(10, -9.84) * mm, "end": v(10, -8.6) * mm});
            skLineSegment(sketch, "E2474.MirrorCS", {"start": v(-10, 10) * mm, "end": v(-10, -10) * mm});
            skPoint(sketch, "E2475.MirrorP", {"position": v(0, 0) * mm});
            skLineSegment(sketch, "E2476.MirrorCS", {"start": v(9.84, 2.46) * mm, "end": v(9.84, 3.7) * mm});
            skLineSegment(sketch, "E2477.MirrorCS", {"start": v(10, -1.23) * mm, "end": v(10, 0) * mm});
            skArc(sketch, "E2478.MirrorCS", {"start": v(9.22, -4.92) * mm, "mid": v(9.84, -5.53) * mm, "end": v(9.22, -6.15) * mm});
            skLineSegment(sketch, "E2479.MirrorCS", {"start": v(10, 7.38) * mm, "end": v(-10, 7.38) * mm});
            skLineSegment(sketch, "E2480.MirrorCS", {"start": v(-9.84, -3.69) * mm, "end": v(-9.84, -2.46) * mm});
            skLineSegment(sketch, "E2481.MirrorCS", {"start": v(10, -1.23) * mm, "end": v(-10, -1.23) * mm});
            skLineSegment(sketch, "E2482.MirrorCS", {"start": v(10, -10) * mm, "end": v(-10, -10) * mm});
            skLineSegment(sketch, "E2483.MirrorCS", {"start": v(-10, 7.38) * mm, "end": v(-10, 6.15) * mm});
            skArc(sketch, "E2484.MirrorCS", {"start": v(-9.23, -4.92) * mm, "mid": v(-9.84, -4.3) * mm, "end": v(-9.23, -3.69) * mm});
            skLineSegment(sketch, "E2485.MirrorCS", {"start": v(9.22, -9.84) * mm, "end": v(9.22, -8.6) * mm});
            skLineSegment(sketch, "E2486.MirrorCS", {"start": v(9.84, 1.23) * mm, "end": v(9.84, 2.46) * mm});
            skLineSegment(sketch, "E2487.MirrorCS", {"start": v(9.22, -3.69) * mm, "end": v(-9.23, -3.69) * mm});
            skSolve(sketch);
        }
        {
            var Q0;
            Q0=qCreatedBy(id+"F7.planeOp",FACE);
            var sketch = newSketch(context, id + "F37", { "sketchPlane" : qUnion([Q0])});
            skCircle(sketch, "E2488", {"center": v(-9.84, 3.9) * mm, "radius": 0.2 * mm});
            skSolve(sketch);
        }
    });
